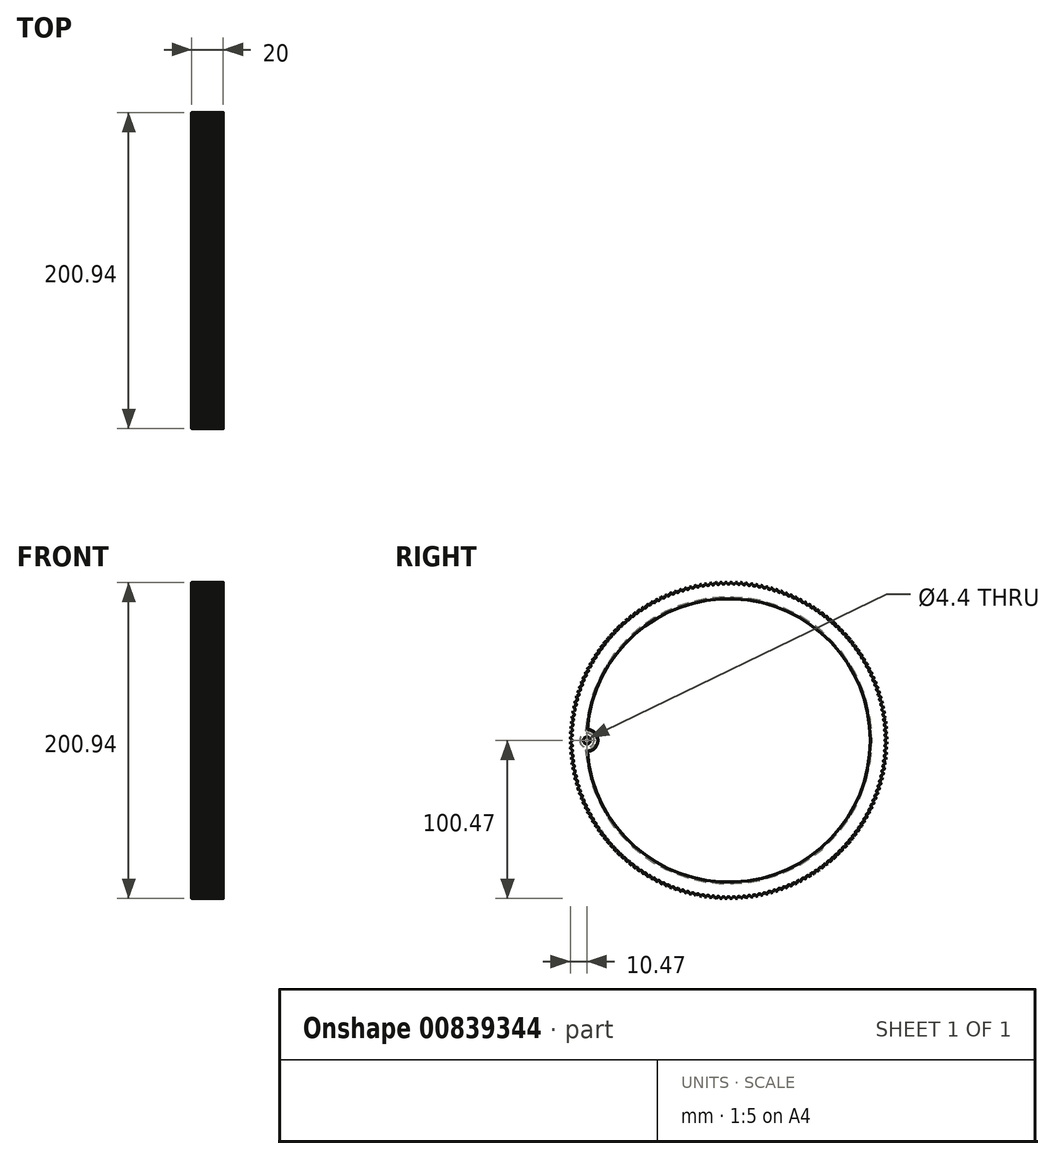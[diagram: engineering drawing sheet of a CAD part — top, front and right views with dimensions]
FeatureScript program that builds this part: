
annotation { "Feature Type Name" : "Feature", "Feature Type Description" : "" }
export const myFeature = defineFeature(function(context is Context, id is Id, definition is map)
    precondition{}
    {
        {
            var Q0;
            Q0=qCreatedBy(makeId("Right.planeOp"),FACE);
            var sketch = newSketch(context, id + "F0", { "sketchPlane" : qUnion([Q0])});
            skCircle(sketch, "E0", {"center": v(0, 0) * mm, "radius": 90 * mm});
            skLineSegment(sketch, "E1", {"start": v(0, 0) * mm, "end": v(0, 100.53) * mm, "construction": true});
            skPoint(sketch, "E2.center", {"position": v(0, 61.04) * mm});
            skLineSegment(sketch, "E2.anchor1", {"start": v(0, 61.04) * mm, "end": v(0, 81.8) * mm, "construction": true});
            skLineSegment(sketch, "E3.trimOffspring", {"start": v(0, 10.5) * mm, "end": v(0, 81.8) * mm, "construction": true});
            skLineSegment(sketch, "E4", {"start": v(-1.05, 100.47) * mm, "end": v(-1, 100.18) * mm});
            skArc(sketch, "E5", {"start": v(0.01, 99.33) * mm, "mid": v(0, 99.33) * mm, "end": v(-0.01, 99.33) * mm});
            skArc(sketch, "E6.filletArc", {"start": v(-1, 100.18) * mm, "mid": v(-0.67, 99.57) * mm, "end": v(-0.01, 99.33) * mm});
            skLineSegment(sketch, "E7.MirrorCS", {"start": v(1.05, 100.47) * mm, "end": v(1, 100.18) * mm});
            skArc(sketch, "E8.MirrorCS", {"start": v(1, 100.18) * mm, "mid": v(0.67, 99.57) * mm, "end": v(0.01, 99.33) * mm});
            skPoint(sketch, "E9.orphan", {"position": v(-12.8, 89.08) * mm});
            skPoint(sketch, "E10.orphan", {"position": v(12.8, 89.08) * mm});
            skLineSegment(sketch, "E11", {"start": v(0.02, 100.33) * mm, "end": v(1, 100.18) * mm, "construction": true});
            skLineSegment(sketch, "E12", {"start": v(-0.02, 100.33) * mm, "end": v(-1, 100.18) * mm, "construction": true});
            skLineSegment(sketch, "E13", {"start": v(-1.05, 100.47) * mm, "end": v(0, 100.53) * mm, "construction": true});
            skLineSegment(sketch, "E14", {"start": v(1.05, 100.47) * mm, "end": v(0, 100.53) * mm, "construction": true});
            skCircle(sketch, "E15", {"center": v(0, 0) * mm, "radius": 100.48 * mm});
            skArc(sketch, "E16.1.0", {"start": v(-4.28, 100.1) * mm, "mid": v(-3.93, 99.5) * mm, "end": v(-3.26, 99.27) * mm});
            skArc(sketch, "E16.1.1", {"start": v(-3.24, 99.27) * mm, "mid": v(-3.25, 99.27) * mm, "end": v(-3.26, 99.27) * mm});
            skArc(sketch, "E16.1.2", {"start": v(-2.27, 100.16) * mm, "mid": v(-2.59, 99.54) * mm, "end": v(-3.24, 99.27) * mm});
            skLineSegment(sketch, "E16.1.3", {"start": v(-2.24, 100.46) * mm, "end": v(-2.27, 100.16) * mm});
            skLineSegment(sketch, "E16.1.4", {"start": v(-4.33, 100.39) * mm, "end": v(-4.28, 100.1) * mm});
            skArc(sketch, "E16.2.0", {"start": v(-7.56, 99.9) * mm, "mid": v(-7.18, 99.31) * mm, "end": v(-6.51, 99.11) * mm});
            skArc(sketch, "E16.2.1", {"start": v(-6.48, 99.12) * mm, "mid": v(-6.5, 99.11) * mm, "end": v(-6.51, 99.11) * mm});
            skArc(sketch, "E16.2.2", {"start": v(-5.55, 100.04) * mm, "mid": v(-5.84, 99.4) * mm, "end": v(-6.48, 99.12) * mm});
            skLineSegment(sketch, "E16.2.3", {"start": v(-5.53, 100.33) * mm, "end": v(-5.55, 100.04) * mm});
            skLineSegment(sketch, "E16.2.4", {"start": v(-7.62, 100.2) * mm, "end": v(-7.56, 99.9) * mm});
            skArc(sketch, "E16.3.0", {"start": v(-10.82, 99.6) * mm, "mid": v(-10.43, 99.03) * mm, "end": v(-9.75, 98.85) * mm});
            skArc(sketch, "E16.3.1", {"start": v(-9.72, 98.85) * mm, "mid": v(-9.74, 98.85) * mm, "end": v(-9.75, 98.85) * mm});
            skArc(sketch, "E16.3.2", {"start": v(-8.82, 99.8) * mm, "mid": v(-9.1, 99.16) * mm, "end": v(-9.72, 98.85) * mm});
            skLineSegment(sketch, "E16.3.3", {"start": v(-8.8, 100.1) * mm, "end": v(-8.82, 99.8) * mm});
            skLineSegment(sketch, "E16.3.4", {"start": v(-10.9, 99.89) * mm, "end": v(-10.82, 99.6) * mm});
            skArc(sketch, "E16.4.0", {"start": v(-14.07, 99.2) * mm, "mid": v(-13.66, 98.63) * mm, "end": v(-12.98, 98.48) * mm});
            skArc(sketch, "E16.4.1", {"start": v(-12.95, 98.48) * mm, "mid": v(-12.96, 98.48) * mm, "end": v(-12.98, 98.48) * mm});
            skArc(sketch, "E16.4.2", {"start": v(-12.08, 99.46) * mm, "mid": v(-12.33, 98.8) * mm, "end": v(-12.95, 98.48) * mm});
            skLineSegment(sketch, "E16.4.3", {"start": v(-12.08, 99.75) * mm, "end": v(-12.08, 99.46) * mm});
            skLineSegment(sketch, "E16.4.4", {"start": v(-14.15, 99.48) * mm, "end": v(-14.07, 99.2) * mm});
            skArc(sketch, "E16.5.0", {"start": v(-17.31, 98.68) * mm, "mid": v(-16.88, 98.13) * mm, "end": v(-16.2, 98) * mm});
            skArc(sketch, "E16.5.1", {"start": v(-16.17, 98) * mm, "mid": v(-16.18, 98) * mm, "end": v(-16.2, 98) * mm});
            skArc(sketch, "E16.5.2", {"start": v(-15.33, 99.01) * mm, "mid": v(-15.56, 98.35) * mm, "end": v(-16.17, 98) * mm});
            skLineSegment(sketch, "E16.5.3", {"start": v(-15.33, 99.3) * mm, "end": v(-15.33, 99.01) * mm});
            skLineSegment(sketch, "E16.5.4", {"start": v(-17.4, 98.96) * mm, "end": v(-17.31, 98.68) * mm});
            skArc(sketch, "E16.6.0", {"start": v(-20.53, 98.06) * mm, "mid": v(-20.08, 97.53) * mm, "end": v(-19.4, 97.42) * mm});
            skArc(sketch, "E16.6.1", {"start": v(-19.36, 97.42) * mm, "mid": v(-19.38, 97.42) * mm, "end": v(-19.4, 97.42) * mm});
            skArc(sketch, "E16.6.2", {"start": v(-18.56, 98.46) * mm, "mid": v(-18.77, 97.79) * mm, "end": v(-19.36, 97.42) * mm});
            skLineSegment(sketch, "E16.6.3", {"start": v(-18.57, 98.75) * mm, "end": v(-18.56, 98.46) * mm});
            skLineSegment(sketch, "E16.6.4", {"start": v(-20.63, 98.34) * mm, "end": v(-20.53, 98.06) * mm});
            skArc(sketch, "E16.7.0", {"start": v(-23.73, 97.34) * mm, "mid": v(-23.26, 96.82) * mm, "end": v(-22.57, 96.73) * mm});
            skArc(sketch, "E16.7.1", {"start": v(-22.54, 96.74) * mm, "mid": v(-22.55, 96.73) * mm, "end": v(-22.57, 96.73) * mm});
            skArc(sketch, "E16.7.2", {"start": v(-21.77, 97.8) * mm, "mid": v(-21.96, 97.12) * mm, "end": v(-22.54, 96.74) * mm});
            skLineSegment(sketch, "E16.7.3", {"start": v(-21.8, 98.09) * mm, "end": v(-21.77, 97.8) * mm});
            skLineSegment(sketch, "E16.7.4", {"start": v(-23.84, 97.61) * mm, "end": v(-23.73, 97.34) * mm});
            skArc(sketch, "E16.8.0", {"start": v(-26.9, 96.51) * mm, "mid": v(-26.42, 96) * mm, "end": v(-25.72, 95.94) * mm});
            skArc(sketch, "E16.8.1", {"start": v(-25.7, 95.95) * mm, "mid": v(-25.7, 95.94) * mm, "end": v(-25.72, 95.94) * mm});
            skArc(sketch, "E16.8.2", {"start": v(-24.96, 97.03) * mm, "mid": v(-25.12, 96.35) * mm, "end": v(-25.7, 95.95) * mm});
            skLineSegment(sketch, "E16.8.3", {"start": v(-25, 97.32) * mm, "end": v(-24.96, 97.03) * mm});
            skLineSegment(sketch, "E16.8.4", {"start": v(-27.02, 96.78) * mm, "end": v(-26.9, 96.51) * mm});
            skArc(sketch, "E16.9.0", {"start": v(-30.04, 95.58) * mm, "mid": v(-29.55, 95.09) * mm, "end": v(-28.85, 95.05) * mm});
            skArc(sketch, "E16.9.1", {"start": v(-28.82, 95.05) * mm, "mid": v(-28.83, 95.05) * mm, "end": v(-28.85, 95.05) * mm});
            skArc(sketch, "E16.9.2", {"start": v(-28.12, 96.16) * mm, "mid": v(-28.26, 95.48) * mm, "end": v(-28.82, 95.05) * mm});
            skLineSegment(sketch, "E16.9.3", {"start": v(-28.16, 96.45) * mm, "end": v(-28.12, 96.16) * mm});
            skLineSegment(sketch, "E16.9.4", {"start": v(-30.17, 95.84) * mm, "end": v(-30.04, 95.58) * mm});
            skArc(sketch, "E16.10.0", {"start": v(-33.16, 94.54) * mm, "mid": v(-32.64, 94.07) * mm, "end": v(-31.94, 94.05) * mm});
            skArc(sketch, "E16.10.1", {"start": v(-31.91, 94.06) * mm, "mid": v(-31.93, 94.06) * mm, "end": v(-31.94, 94.05) * mm});
            skArc(sketch, "E16.10.2", {"start": v(-31.25, 95.2) * mm, "mid": v(-31.37, 94.5) * mm, "end": v(-31.91, 94.06) * mm});
            skLineSegment(sketch, "E16.10.3", {"start": v(-31.3, 95.48) * mm, "end": v(-31.25, 95.2) * mm});
            skLineSegment(sketch, "E16.10.4", {"start": v(-33.29, 94.8) * mm, "end": v(-33.16, 94.54) * mm});
            skArc(sketch, "E16.11.0", {"start": v(-36.23, 93.4) * mm, "mid": v(-35.7, 92.95) * mm, "end": v(-35, 92.96) * mm});
            skArc(sketch, "E16.11.1", {"start": v(-34.97, 92.97) * mm, "mid": v(-34.99, 92.96) * mm, "end": v(-35, 92.96) * mm});
            skArc(sketch, "E16.11.2", {"start": v(-34.35, 94.12) * mm, "mid": v(-34.45, 93.42) * mm, "end": v(-34.97, 92.97) * mm});
            skLineSegment(sketch, "E16.11.3", {"start": v(-34.41, 94.4) * mm, "end": v(-34.35, 94.12) * mm});
            skLineSegment(sketch, "E16.11.4", {"start": v(-36.37, 93.67) * mm, "end": v(-36.23, 93.4) * mm});
            skArc(sketch, "E16.12.0", {"start": v(-39.27, 92.17) * mm, "mid": v(-38.72, 91.73) * mm, "end": v(-38.02, 91.76) * mm});
            skArc(sketch, "E16.12.1", {"start": v(-38, 91.77) * mm, "mid": v(-38.01, 91.77) * mm, "end": v(-38.02, 91.76) * mm});
            skArc(sketch, "E16.12.2", {"start": v(-37.4, 92.94) * mm, "mid": v(-37.48, 92.25) * mm, "end": v(-38, 91.77) * mm});
            skLineSegment(sketch, "E16.12.3", {"start": v(-37.48, 93.23) * mm, "end": v(-37.4, 92.94) * mm});
            skLineSegment(sketch, "E16.12.4", {"start": v(-39.42, 92.43) * mm, "end": v(-39.27, 92.17) * mm});
            skArc(sketch, "E16.13.0", {"start": v(-42.26, 90.84) * mm, "mid": v(-41.7, 90.42) * mm, "end": v(-41, 90.47) * mm});
            skArc(sketch, "E16.13.1", {"start": v(-40.98, 90.48) * mm, "mid": v(-41, 90.47) * mm, "end": v(-41, 90.47) * mm});
            skArc(sketch, "E16.13.2", {"start": v(-40.43, 91.67) * mm, "mid": v(-40.48, 90.97) * mm, "end": v(-40.98, 90.48) * mm});
            skLineSegment(sketch, "E16.13.3", {"start": v(-40.51, 91.95) * mm, "end": v(-40.43, 91.67) * mm});
            skLineSegment(sketch, "E16.13.4", {"start": v(-42.42, 91.09) * mm, "end": v(-42.26, 90.84) * mm});
            skArc(sketch, "E16.14.0", {"start": v(-45.21, 89.4) * mm, "mid": v(-44.64, 89) * mm, "end": v(-43.94, 89.08) * mm});
            skArc(sketch, "E16.14.1", {"start": v(-43.92, 89.09) * mm, "mid": v(-43.93, 89.08) * mm, "end": v(-43.94, 89.08) * mm});
            skArc(sketch, "E16.14.2", {"start": v(-43.4, 90.3) * mm, "mid": v(-43.44, 89.6) * mm, "end": v(-43.92, 89.09) * mm});
            skLineSegment(sketch, "E16.14.3", {"start": v(-43.5, 90.58) * mm, "end": v(-43.4, 90.3) * mm});
            skLineSegment(sketch, "E16.14.4", {"start": v(-45.38, 89.65) * mm, "end": v(-45.21, 89.4) * mm});
            skArc(sketch, "E16.15.0", {"start": v(-48.11, 87.88) * mm, "mid": v(-47.53, 87.5) * mm, "end": v(-46.84, 87.6) * mm});
            skArc(sketch, "E16.15.1", {"start": v(-46.8, 87.6) * mm, "mid": v(-46.82, 87.6) * mm, "end": v(-46.84, 87.6) * mm});
            skArc(sketch, "E16.15.2", {"start": v(-46.34, 88.83) * mm, "mid": v(-46.35, 88.13) * mm, "end": v(-46.8, 87.6) * mm});
            skLineSegment(sketch, "E16.15.3", {"start": v(-46.44, 89.1) * mm, "end": v(-46.34, 88.83) * mm});
            skLineSegment(sketch, "E16.15.4", {"start": v(-48.29, 88.12) * mm, "end": v(-48.11, 87.88) * mm});
            skArc(sketch, "E16.16.0", {"start": v(-50.96, 86.26) * mm, "mid": v(-50.37, 85.9) * mm, "end": v(-49.68, 86.01) * mm});
            skArc(sketch, "E16.16.1", {"start": v(-49.65, 86.03) * mm, "mid": v(-49.66, 86.02) * mm, "end": v(-49.68, 86.01) * mm});
            skArc(sketch, "E16.16.2", {"start": v(-49.22, 87.27) * mm, "mid": v(-49.2, 86.57) * mm, "end": v(-49.65, 86.03) * mm});
            skLineSegment(sketch, "E16.16.3", {"start": v(-49.33, 87.54) * mm, "end": v(-49.22, 87.27) * mm});
            skLineSegment(sketch, "E16.16.4", {"start": v(-51.14, 86.49) * mm, "end": v(-50.96, 86.26) * mm});
            skArc(sketch, "E16.17.0", {"start": v(-53.76, 84.55) * mm, "mid": v(-53.15, 84.2) * mm, "end": v(-52.46, 84.34) * mm});
            skArc(sketch, "E16.17.1", {"start": v(-52.44, 84.36) * mm, "mid": v(-52.45, 84.35) * mm, "end": v(-52.46, 84.34) * mm});
            skArc(sketch, "E16.17.2", {"start": v(-52.05, 85.6) * mm, "mid": v(-52.01, 84.9) * mm, "end": v(-52.44, 84.36) * mm});
            skLineSegment(sketch, "E16.17.3", {"start": v(-52.17, 85.88) * mm, "end": v(-52.05, 85.6) * mm});
            skLineSegment(sketch, "E16.17.4", {"start": v(-53.95, 84.77) * mm, "end": v(-53.76, 84.55) * mm});
            skArc(sketch, "E16.18.0", {"start": v(-56.5, 82.74) * mm, "mid": v(-55.88, 82.42) * mm, "end": v(-55.2, 82.58) * mm});
            skArc(sketch, "E16.18.1", {"start": v(-55.17, 82.6) * mm, "mid": v(-55.18, 82.59) * mm, "end": v(-55.2, 82.58) * mm});
            skArc(sketch, "E16.18.2", {"start": v(-54.82, 83.86) * mm, "mid": v(-54.76, 83.16) * mm, "end": v(-55.17, 82.6) * mm});
            skLineSegment(sketch, "E16.18.3", {"start": v(-54.95, 84.12) * mm, "end": v(-54.82, 83.86) * mm});
            skLineSegment(sketch, "E16.18.4", {"start": v(-56.7, 82.96) * mm, "end": v(-56.5, 82.74) * mm});
            skArc(sketch, "E16.19.0", {"start": v(-59.17, 80.85) * mm, "mid": v(-58.54, 80.55) * mm, "end": v(-57.87, 80.73) * mm});
            skArc(sketch, "E16.19.1", {"start": v(-57.84, 80.75) * mm, "mid": v(-57.86, 80.74) * mm, "end": v(-57.87, 80.73) * mm});
            skArc(sketch, "E16.19.2", {"start": v(-57.54, 82.02) * mm, "mid": v(-57.45, 81.33) * mm, "end": v(-57.84, 80.75) * mm});
            skLineSegment(sketch, "E16.19.3", {"start": v(-57.67, 82.28) * mm, "end": v(-57.54, 82.02) * mm});
            skLineSegment(sketch, "E16.19.4", {"start": v(-59.38, 81.06) * mm, "end": v(-59.17, 80.85) * mm});
            skArc(sketch, "E16.20.0", {"start": v(-61.79, 78.87) * mm, "mid": v(-61.15, 78.59) * mm, "end": v(-60.48, 78.8) * mm});
            skArc(sketch, "E16.20.1", {"start": v(-60.45, 78.81) * mm, "mid": v(-60.47, 78.8) * mm, "end": v(-60.48, 78.8) * mm});
            skArc(sketch, "E16.20.2", {"start": v(-60.2, 80.1) * mm, "mid": v(-60.08, 79.4) * mm, "end": v(-60.45, 78.81) * mm});
            skLineSegment(sketch, "E16.20.3", {"start": v(-60.33, 80.35) * mm, "end": v(-60.2, 80.1) * mm});
            skLineSegment(sketch, "E16.20.4", {"start": v(-62, 79.07) * mm, "end": v(-61.79, 78.87) * mm});
            skArc(sketch, "E16.21.0", {"start": v(-64.33, 76.8) * mm, "mid": v(-63.69, 76.54) * mm, "end": v(-63.02, 76.77) * mm});
            skArc(sketch, "E16.21.1", {"start": v(-63, 76.79) * mm, "mid": v(-63.01, 76.78) * mm, "end": v(-63.02, 76.77) * mm});
            skArc(sketch, "E16.21.2", {"start": v(-62.78, 78.08) * mm, "mid": v(-62.65, 77.4) * mm, "end": v(-63, 76.79) * mm});
            skLineSegment(sketch, "E16.21.3", {"start": v(-62.93, 78.33) * mm, "end": v(-62.78, 78.08) * mm});
            skLineSegment(sketch, "E16.21.4", {"start": v(-64.55, 77) * mm, "end": v(-64.33, 76.8) * mm});
            skArc(sketch, "E16.22.0", {"start": v(-66.81, 74.66) * mm, "mid": v(-66.16, 74.42) * mm, "end": v(-65.5, 74.67) * mm});
            skArc(sketch, "E16.22.1", {"start": v(-65.48, 74.69) * mm, "mid": v(-65.5, 74.68) * mm, "end": v(-65.5, 74.67) * mm});
            skArc(sketch, "E16.22.2", {"start": v(-65.3, 75.99) * mm, "mid": v(-65.15, 75.3) * mm, "end": v(-65.48, 74.69) * mm});
            skLineSegment(sketch, "E16.22.3", {"start": v(-65.46, 76.23) * mm, "end": v(-65.3, 75.99) * mm});
            skLineSegment(sketch, "E16.22.4", {"start": v(-67.04, 74.85) * mm, "end": v(-66.81, 74.66) * mm});
            skArc(sketch, "E16.23.0", {"start": v(-69.22, 72.43) * mm, "mid": v(-68.55, 72.21) * mm, "end": v(-67.9, 72.49) * mm});
            skArc(sketch, "E16.23.1", {"start": v(-67.89, 72.5) * mm, "mid": v(-67.9, 72.5) * mm, "end": v(-67.9, 72.49) * mm});
            skArc(sketch, "E16.23.2", {"start": v(-67.75, 73.8) * mm, "mid": v(-67.58, 73.13) * mm, "end": v(-67.89, 72.5) * mm});
            skLineSegment(sketch, "E16.23.3", {"start": v(-67.92, 74.05) * mm, "end": v(-67.75, 73.8) * mm});
            skLineSegment(sketch, "E16.23.4", {"start": v(-69.45, 72.62) * mm, "end": v(-69.22, 72.43) * mm});
            skArc(sketch, "E16.24.0", {"start": v(-71.55, 70.13) * mm, "mid": v(-70.88, 69.93) * mm, "end": v(-70.24, 70.22) * mm});
            skArc(sketch, "E16.24.1", {"start": v(-70.22, 70.24) * mm, "mid": v(-70.23, 70.23) * mm, "end": v(-70.24, 70.22) * mm});
            skArc(sketch, "E16.24.2", {"start": v(-70.13, 71.55) * mm, "mid": v(-69.93, 70.88) * mm, "end": v(-70.22, 70.24) * mm});
            skLineSegment(sketch, "E16.24.3", {"start": v(-70.3, 71.79) * mm, "end": v(-70.13, 71.55) * mm});
            skLineSegment(sketch, "E16.24.4", {"start": v(-71.79, 70.3) * mm, "end": v(-71.55, 70.13) * mm});
            skArc(sketch, "E16.25.0", {"start": v(-73.8, 67.75) * mm, "mid": v(-73.13, 67.58) * mm, "end": v(-72.5, 67.89) * mm});
            skArc(sketch, "E16.25.1", {"start": v(-72.49, 67.9) * mm, "mid": v(-72.5, 67.9) * mm, "end": v(-72.5, 67.89) * mm});
            skArc(sketch, "E16.25.2", {"start": v(-72.43, 69.22) * mm, "mid": v(-72.21, 68.55) * mm, "end": v(-72.49, 67.9) * mm});
            skLineSegment(sketch, "E16.25.3", {"start": v(-72.62, 69.45) * mm, "end": v(-72.43, 69.22) * mm});
            skLineSegment(sketch, "E16.25.4", {"start": v(-74.05, 67.92) * mm, "end": v(-73.8, 67.75) * mm});
            skArc(sketch, "E16.26.0", {"start": v(-75.99, 65.3) * mm, "mid": v(-75.3, 65.15) * mm, "end": v(-74.69, 65.48) * mm});
            skArc(sketch, "E16.26.1", {"start": v(-74.67, 65.5) * mm, "mid": v(-74.68, 65.5) * mm, "end": v(-74.69, 65.48) * mm});
            skArc(sketch, "E16.26.2", {"start": v(-74.66, 66.81) * mm, "mid": v(-74.42, 66.16) * mm, "end": v(-74.67, 65.5) * mm});
            skLineSegment(sketch, "E16.26.3", {"start": v(-74.85, 67.04) * mm, "end": v(-74.66, 66.81) * mm});
            skLineSegment(sketch, "E16.26.4", {"start": v(-76.23, 65.46) * mm, "end": v(-75.99, 65.3) * mm});
            skArc(sketch, "E16.27.0", {"start": v(-78.08, 62.78) * mm, "mid": v(-77.4, 62.65) * mm, "end": v(-76.79, 63) * mm});
            skArc(sketch, "E16.27.1", {"start": v(-76.77, 63.02) * mm, "mid": v(-76.78, 63.01) * mm, "end": v(-76.79, 63) * mm});
            skArc(sketch, "E16.27.2", {"start": v(-76.8, 64.33) * mm, "mid": v(-76.54, 63.69) * mm, "end": v(-76.77, 63.02) * mm});
            skLineSegment(sketch, "E16.27.3", {"start": v(-77, 64.55) * mm, "end": v(-76.8, 64.33) * mm});
            skLineSegment(sketch, "E16.27.4", {"start": v(-78.33, 62.93) * mm, "end": v(-78.08, 62.78) * mm});
            skArc(sketch, "E16.28.0", {"start": v(-80.1, 60.2) * mm, "mid": v(-79.4, 60.08) * mm, "end": v(-78.81, 60.45) * mm});
            skArc(sketch, "E16.28.1", {"start": v(-78.8, 60.48) * mm, "mid": v(-78.8, 60.47) * mm, "end": v(-78.81, 60.45) * mm});
            skArc(sketch, "E16.28.2", {"start": v(-78.87, 61.79) * mm, "mid": v(-78.59, 61.15) * mm, "end": v(-78.8, 60.48) * mm});
            skLineSegment(sketch, "E16.28.3", {"start": v(-79.07, 62) * mm, "end": v(-78.87, 61.79) * mm});
            skLineSegment(sketch, "E16.28.4", {"start": v(-80.35, 60.33) * mm, "end": v(-80.1, 60.2) * mm});
            skArc(sketch, "E16.29.0", {"start": v(-82.02, 57.54) * mm, "mid": v(-81.33, 57.45) * mm, "end": v(-80.75, 57.84) * mm});
            skArc(sketch, "E16.29.1", {"start": v(-80.73, 57.87) * mm, "mid": v(-80.74, 57.86) * mm, "end": v(-80.75, 57.84) * mm});
            skArc(sketch, "E16.29.2", {"start": v(-80.85, 59.17) * mm, "mid": v(-80.55, 58.54) * mm, "end": v(-80.73, 57.87) * mm});
            skLineSegment(sketch, "E16.29.3", {"start": v(-81.06, 59.38) * mm, "end": v(-80.85, 59.17) * mm});
            skLineSegment(sketch, "E16.29.4", {"start": v(-82.28, 57.67) * mm, "end": v(-82.02, 57.54) * mm});
            skArc(sketch, "E16.30.0", {"start": v(-83.86, 54.82) * mm, "mid": v(-83.16, 54.76) * mm, "end": v(-82.6, 55.17) * mm});
            skArc(sketch, "E16.30.1", {"start": v(-82.58, 55.2) * mm, "mid": v(-82.59, 55.18) * mm, "end": v(-82.6, 55.17) * mm});
            skArc(sketch, "E16.30.2", {"start": v(-82.74, 56.5) * mm, "mid": v(-82.42, 55.88) * mm, "end": v(-82.58, 55.2) * mm});
            skLineSegment(sketch, "E16.30.3", {"start": v(-82.96, 56.7) * mm, "end": v(-82.74, 56.5) * mm});
            skLineSegment(sketch, "E16.30.4", {"start": v(-84.12, 54.95) * mm, "end": v(-83.86, 54.82) * mm});
            skArc(sketch, "E16.31.0", {"start": v(-85.6, 52.05) * mm, "mid": v(-84.9, 52.01) * mm, "end": v(-84.36, 52.44) * mm});
            skArc(sketch, "E16.31.1", {"start": v(-84.34, 52.46) * mm, "mid": v(-84.35, 52.45) * mm, "end": v(-84.36, 52.44) * mm});
            skArc(sketch, "E16.31.2", {"start": v(-84.55, 53.76) * mm, "mid": v(-84.2, 53.15) * mm, "end": v(-84.34, 52.46) * mm});
            skLineSegment(sketch, "E16.31.3", {"start": v(-84.77, 53.95) * mm, "end": v(-84.55, 53.76) * mm});
            skLineSegment(sketch, "E16.31.4", {"start": v(-85.88, 52.17) * mm, "end": v(-85.6, 52.05) * mm});
            skArc(sketch, "E16.32.0", {"start": v(-87.27, 49.22) * mm, "mid": v(-86.57, 49.2) * mm, "end": v(-86.03, 49.65) * mm});
            skArc(sketch, "E16.32.1", {"start": v(-86.01, 49.68) * mm, "mid": v(-86.02, 49.66) * mm, "end": v(-86.03, 49.65) * mm});
            skArc(sketch, "E16.32.2", {"start": v(-86.26, 50.96) * mm, "mid": v(-85.9, 50.37) * mm, "end": v(-86.01, 49.68) * mm});
            skLineSegment(sketch, "E16.32.3", {"start": v(-86.49, 51.14) * mm, "end": v(-86.26, 50.96) * mm});
            skLineSegment(sketch, "E16.32.4", {"start": v(-87.54, 49.33) * mm, "end": v(-87.27, 49.22) * mm});
            skArc(sketch, "E16.33.0", {"start": v(-88.83, 46.34) * mm, "mid": v(-88.13, 46.35) * mm, "end": v(-87.6, 46.8) * mm});
            skArc(sketch, "E16.33.1", {"start": v(-87.6, 46.84) * mm, "mid": v(-87.6, 46.82) * mm, "end": v(-87.6, 46.8) * mm});
            skArc(sketch, "E16.33.2", {"start": v(-87.88, 48.11) * mm, "mid": v(-87.5, 47.53) * mm, "end": v(-87.6, 46.84) * mm});
            skLineSegment(sketch, "E16.33.3", {"start": v(-88.12, 48.29) * mm, "end": v(-87.88, 48.11) * mm});
            skLineSegment(sketch, "E16.33.4", {"start": v(-89.1, 46.44) * mm, "end": v(-88.83, 46.34) * mm});
            skArc(sketch, "E16.34.0", {"start": v(-90.3, 43.4) * mm, "mid": v(-89.6, 43.44) * mm, "end": v(-89.09, 43.92) * mm});
            skArc(sketch, "E16.34.1", {"start": v(-89.08, 43.94) * mm, "mid": v(-89.08, 43.93) * mm, "end": v(-89.09, 43.92) * mm});
            skArc(sketch, "E16.34.2", {"start": v(-89.4, 45.21) * mm, "mid": v(-89, 44.64) * mm, "end": v(-89.08, 43.94) * mm});
            skLineSegment(sketch, "E16.34.3", {"start": v(-89.65, 45.38) * mm, "end": v(-89.4, 45.21) * mm});
            skLineSegment(sketch, "E16.34.4", {"start": v(-90.58, 43.5) * mm, "end": v(-90.3, 43.4) * mm});
            skArc(sketch, "E16.35.0", {"start": v(-91.67, 40.43) * mm, "mid": v(-90.97, 40.48) * mm, "end": v(-90.48, 40.98) * mm});
            skArc(sketch, "E16.35.1", {"start": v(-90.47, 41) * mm, "mid": v(-90.47, 41) * mm, "end": v(-90.48, 40.98) * mm});
            skArc(sketch, "E16.35.2", {"start": v(-90.84, 42.26) * mm, "mid": v(-90.42, 41.7) * mm, "end": v(-90.47, 41) * mm});
            skLineSegment(sketch, "E16.35.3", {"start": v(-91.09, 42.42) * mm, "end": v(-90.84, 42.26) * mm});
            skLineSegment(sketch, "E16.35.4", {"start": v(-91.95, 40.51) * mm, "end": v(-91.67, 40.43) * mm});
            skArc(sketch, "E16.36.0", {"start": v(-92.94, 37.4) * mm, "mid": v(-92.25, 37.48) * mm, "end": v(-91.77, 38) * mm});
            skArc(sketch, "E16.36.1", {"start": v(-91.76, 38.02) * mm, "mid": v(-91.77, 38.01) * mm, "end": v(-91.77, 38) * mm});
            skArc(sketch, "E16.36.2", {"start": v(-92.17, 39.27) * mm, "mid": v(-91.73, 38.72) * mm, "end": v(-91.76, 38.02) * mm});
            skLineSegment(sketch, "E16.36.3", {"start": v(-92.43, 39.42) * mm, "end": v(-92.17, 39.27) * mm});
            skLineSegment(sketch, "E16.36.4", {"start": v(-93.23, 37.48) * mm, "end": v(-92.94, 37.4) * mm});
            skArc(sketch, "E16.37.0", {"start": v(-94.12, 34.35) * mm, "mid": v(-93.42, 34.45) * mm, "end": v(-92.97, 34.97) * mm});
            skArc(sketch, "E16.37.1", {"start": v(-92.96, 35) * mm, "mid": v(-92.96, 34.99) * mm, "end": v(-92.97, 34.97) * mm});
            skArc(sketch, "E16.37.2", {"start": v(-93.4, 36.23) * mm, "mid": v(-92.95, 35.7) * mm, "end": v(-92.96, 35) * mm});
            skLineSegment(sketch, "E16.37.3", {"start": v(-93.67, 36.37) * mm, "end": v(-93.4, 36.23) * mm});
            skLineSegment(sketch, "E16.37.4", {"start": v(-94.4, 34.41) * mm, "end": v(-94.12, 34.35) * mm});
            skArc(sketch, "E16.38.0", {"start": v(-95.2, 31.25) * mm, "mid": v(-94.5, 31.37) * mm, "end": v(-94.06, 31.91) * mm});
            skArc(sketch, "E16.38.1", {"start": v(-94.05, 31.94) * mm, "mid": v(-94.06, 31.93) * mm, "end": v(-94.06, 31.91) * mm});
            skArc(sketch, "E16.38.2", {"start": v(-94.54, 33.16) * mm, "mid": v(-94.07, 32.64) * mm, "end": v(-94.05, 31.94) * mm});
            skLineSegment(sketch, "E16.38.3", {"start": v(-94.8, 33.29) * mm, "end": v(-94.54, 33.16) * mm});
            skLineSegment(sketch, "E16.38.4", {"start": v(-95.48, 31.3) * mm, "end": v(-95.2, 31.25) * mm});
            skArc(sketch, "E16.39.0", {"start": v(-96.16, 28.12) * mm, "mid": v(-95.48, 28.26) * mm, "end": v(-95.05, 28.82) * mm});
            skArc(sketch, "E16.39.1", {"start": v(-95.05, 28.85) * mm, "mid": v(-95.05, 28.83) * mm, "end": v(-95.05, 28.82) * mm});
            skArc(sketch, "E16.39.2", {"start": v(-95.58, 30.04) * mm, "mid": v(-95.09, 29.55) * mm, "end": v(-95.05, 28.85) * mm});
            skLineSegment(sketch, "E16.39.3", {"start": v(-95.84, 30.17) * mm, "end": v(-95.58, 30.04) * mm});
            skLineSegment(sketch, "E16.39.4", {"start": v(-96.45, 28.16) * mm, "end": v(-96.16, 28.12) * mm});
            skArc(sketch, "E16.40.0", {"start": v(-97.03, 24.96) * mm, "mid": v(-96.35, 25.12) * mm, "end": v(-95.95, 25.7) * mm});
            skArc(sketch, "E16.40.1", {"start": v(-95.94, 25.72) * mm, "mid": v(-95.94, 25.7) * mm, "end": v(-95.95, 25.7) * mm});
            skArc(sketch, "E16.40.2", {"start": v(-96.51, 26.9) * mm, "mid": v(-96, 26.42) * mm, "end": v(-95.94, 25.72) * mm});
            skLineSegment(sketch, "E16.40.3", {"start": v(-96.78, 27.02) * mm, "end": v(-96.51, 26.9) * mm});
            skLineSegment(sketch, "E16.40.4", {"start": v(-97.32, 25) * mm, "end": v(-97.03, 24.96) * mm});
            skArc(sketch, "E16.41.0", {"start": v(-97.8, 21.77) * mm, "mid": v(-97.12, 21.96) * mm, "end": v(-96.74, 22.54) * mm});
            skArc(sketch, "E16.41.1", {"start": v(-96.73, 22.57) * mm, "mid": v(-96.73, 22.55) * mm, "end": v(-96.74, 22.54) * mm});
            skArc(sketch, "E16.41.2", {"start": v(-97.34, 23.73) * mm, "mid": v(-96.82, 23.26) * mm, "end": v(-96.73, 22.57) * mm});
            skLineSegment(sketch, "E16.41.3", {"start": v(-97.61, 23.84) * mm, "end": v(-97.34, 23.73) * mm});
            skLineSegment(sketch, "E16.41.4", {"start": v(-98.09, 21.8) * mm, "end": v(-97.8, 21.77) * mm});
            skArc(sketch, "E16.42.0", {"start": v(-98.46, 18.56) * mm, "mid": v(-97.79, 18.77) * mm, "end": v(-97.42, 19.36) * mm});
            skArc(sketch, "E16.42.1", {"start": v(-97.42, 19.4) * mm, "mid": v(-97.42, 19.38) * mm, "end": v(-97.42, 19.36) * mm});
            skArc(sketch, "E16.42.2", {"start": v(-98.06, 20.53) * mm, "mid": v(-97.53, 20.08) * mm, "end": v(-97.42, 19.4) * mm});
            skLineSegment(sketch, "E16.42.3", {"start": v(-98.34, 20.63) * mm, "end": v(-98.06, 20.53) * mm});
            skLineSegment(sketch, "E16.42.4", {"start": v(-98.75, 18.57) * mm, "end": v(-98.46, 18.56) * mm});
            skArc(sketch, "E16.43.0", {"start": v(-99.01, 15.33) * mm, "mid": v(-98.35, 15.56) * mm, "end": v(-98, 16.17) * mm});
            skArc(sketch, "E16.43.1", {"start": v(-98, 16.2) * mm, "mid": v(-98, 16.18) * mm, "end": v(-98, 16.17) * mm});
            skArc(sketch, "E16.43.2", {"start": v(-98.68, 17.31) * mm, "mid": v(-98.13, 16.88) * mm, "end": v(-98, 16.2) * mm});
            skLineSegment(sketch, "E16.43.3", {"start": v(-98.96, 17.4) * mm, "end": v(-98.68, 17.31) * mm});
            skLineSegment(sketch, "E16.43.4", {"start": v(-99.3, 15.33) * mm, "end": v(-99.01, 15.33) * mm});
            skArc(sketch, "E16.44.0", {"start": v(-99.46, 12.08) * mm, "mid": v(-98.8, 12.33) * mm, "end": v(-98.48, 12.95) * mm});
            skArc(sketch, "E16.44.1", {"start": v(-98.48, 12.98) * mm, "mid": v(-98.48, 12.96) * mm, "end": v(-98.48, 12.95) * mm});
            skArc(sketch, "E16.44.2", {"start": v(-99.2, 14.07) * mm, "mid": v(-98.63, 13.66) * mm, "end": v(-98.48, 12.98) * mm});
            skLineSegment(sketch, "E16.44.3", {"start": v(-99.48, 14.15) * mm, "end": v(-99.2, 14.07) * mm});
            skLineSegment(sketch, "E16.44.4", {"start": v(-99.75, 12.08) * mm, "end": v(-99.46, 12.08) * mm});
            skArc(sketch, "E16.45.0", {"start": v(-99.8, 8.82) * mm, "mid": v(-99.16, 9.1) * mm, "end": v(-98.85, 9.72) * mm});
            skArc(sketch, "E16.45.1", {"start": v(-98.85, 9.75) * mm, "mid": v(-98.85, 9.74) * mm, "end": v(-98.85, 9.72) * mm});
            skArc(sketch, "E16.45.2", {"start": v(-99.6, 10.82) * mm, "mid": v(-99.03, 10.43) * mm, "end": v(-98.85, 9.75) * mm});
            skLineSegment(sketch, "E16.45.3", {"start": v(-99.89, 10.9) * mm, "end": v(-99.6, 10.82) * mm});
            skLineSegment(sketch, "E16.45.4", {"start": v(-100.1, 8.8) * mm, "end": v(-99.8, 8.82) * mm});
            skArc(sketch, "E16.46.0", {"start": v(-100.04, 5.55) * mm, "mid": v(-99.4, 5.84) * mm, "end": v(-99.12, 6.48) * mm});
            skArc(sketch, "E16.46.1", {"start": v(-99.11, 6.51) * mm, "mid": v(-99.11, 6.5) * mm, "end": v(-99.12, 6.48) * mm});
            skArc(sketch, "E16.46.2", {"start": v(-99.9, 7.56) * mm, "mid": v(-99.31, 7.18) * mm, "end": v(-99.11, 6.51) * mm});
            skLineSegment(sketch, "E16.46.3", {"start": v(-100.2, 7.62) * mm, "end": v(-99.9, 7.56) * mm});
            skLineSegment(sketch, "E16.46.4", {"start": v(-100.33, 5.53) * mm, "end": v(-100.04, 5.55) * mm});
            skArc(sketch, "E16.47.0", {"start": v(-100.16, 2.27) * mm, "mid": v(-99.54, 2.59) * mm, "end": v(-99.27, 3.24) * mm});
            skArc(sketch, "E16.47.1", {"start": v(-99.27, 3.26) * mm, "mid": v(-99.27, 3.25) * mm, "end": v(-99.27, 3.24) * mm});
            skArc(sketch, "E16.47.2", {"start": v(-100.1, 4.28) * mm, "mid": v(-99.5, 3.93) * mm, "end": v(-99.27, 3.26) * mm});
            skLineSegment(sketch, "E16.47.3", {"start": v(-100.39, 4.33) * mm, "end": v(-100.1, 4.28) * mm});
            skLineSegment(sketch, "E16.47.4", {"start": v(-100.46, 2.24) * mm, "end": v(-100.16, 2.27) * mm});
            skArc(sketch, "E16.48.0", {"start": v(-100.18, -1) * mm, "mid": v(-99.57, -0.67) * mm, "end": v(-99.33, -0.01) * mm});
            skArc(sketch, "E16.48.1", {"start": v(-99.33, 0.01) * mm, "mid": v(-99.33, 0) * mm, "end": v(-99.33, -0.01) * mm});
            skArc(sketch, "E16.48.2", {"start": v(-100.18, 1) * mm, "mid": v(-99.57, 0.67) * mm, "end": v(-99.33, 0.01) * mm});
            skLineSegment(sketch, "E16.48.3", {"start": v(-100.47, 1.05) * mm, "end": v(-100.18, 1) * mm});
            skLineSegment(sketch, "E16.48.4", {"start": v(-100.47, -1.05) * mm, "end": v(-100.18, -1) * mm});
            skArc(sketch, "E16.49.0", {"start": v(-100.1, -4.28) * mm, "mid": v(-99.5, -3.93) * mm, "end": v(-99.27, -3.26) * mm});
            skArc(sketch, "E16.49.1", {"start": v(-99.27, -3.24) * mm, "mid": v(-99.27, -3.25) * mm, "end": v(-99.27, -3.26) * mm});
            skArc(sketch, "E16.49.2", {"start": v(-100.16, -2.27) * mm, "mid": v(-99.54, -2.59) * mm, "end": v(-99.27, -3.24) * mm});
            skLineSegment(sketch, "E16.49.3", {"start": v(-100.46, -2.24) * mm, "end": v(-100.16, -2.27) * mm});
            skLineSegment(sketch, "E16.49.4", {"start": v(-100.39, -4.33) * mm, "end": v(-100.1, -4.28) * mm});
            skArc(sketch, "E16.50.0", {"start": v(-99.9, -7.56) * mm, "mid": v(-99.31, -7.18) * mm, "end": v(-99.11, -6.51) * mm});
            skArc(sketch, "E16.50.1", {"start": v(-99.12, -6.48) * mm, "mid": v(-99.11, -6.5) * mm, "end": v(-99.11, -6.51) * mm});
            skArc(sketch, "E16.50.2", {"start": v(-100.04, -5.55) * mm, "mid": v(-99.4, -5.84) * mm, "end": v(-99.12, -6.48) * mm});
            skLineSegment(sketch, "E16.50.3", {"start": v(-100.33, -5.53) * mm, "end": v(-100.04, -5.55) * mm});
            skLineSegment(sketch, "E16.50.4", {"start": v(-100.2, -7.62) * mm, "end": v(-99.9, -7.56) * mm});
            skArc(sketch, "E16.51.0", {"start": v(-99.6, -10.82) * mm, "mid": v(-99.03, -10.43) * mm, "end": v(-98.85, -9.75) * mm});
            skArc(sketch, "E16.51.1", {"start": v(-98.85, -9.72) * mm, "mid": v(-98.85, -9.74) * mm, "end": v(-98.85, -9.75) * mm});
            skArc(sketch, "E16.51.2", {"start": v(-99.8, -8.82) * mm, "mid": v(-99.16, -9.1) * mm, "end": v(-98.85, -9.72) * mm});
            skLineSegment(sketch, "E16.51.3", {"start": v(-100.1, -8.8) * mm, "end": v(-99.8, -8.82) * mm});
            skLineSegment(sketch, "E16.51.4", {"start": v(-99.89, -10.9) * mm, "end": v(-99.6, -10.82) * mm});
            skArc(sketch, "E16.52.0", {"start": v(-99.2, -14.07) * mm, "mid": v(-98.63, -13.66) * mm, "end": v(-98.48, -12.98) * mm});
            skArc(sketch, "E16.52.1", {"start": v(-98.48, -12.95) * mm, "mid": v(-98.48, -12.96) * mm, "end": v(-98.48, -12.98) * mm});
            skArc(sketch, "E16.52.2", {"start": v(-99.46, -12.08) * mm, "mid": v(-98.8, -12.33) * mm, "end": v(-98.48, -12.95) * mm});
            skLineSegment(sketch, "E16.52.3", {"start": v(-99.75, -12.08) * mm, "end": v(-99.46, -12.08) * mm});
            skLineSegment(sketch, "E16.52.4", {"start": v(-99.48, -14.15) * mm, "end": v(-99.2, -14.07) * mm});
            skArc(sketch, "E16.53.0", {"start": v(-98.68, -17.31) * mm, "mid": v(-98.13, -16.88) * mm, "end": v(-98, -16.2) * mm});
            skArc(sketch, "E16.53.1", {"start": v(-98, -16.17) * mm, "mid": v(-98, -16.18) * mm, "end": v(-98, -16.2) * mm});
            skArc(sketch, "E16.53.2", {"start": v(-99.01, -15.33) * mm, "mid": v(-98.35, -15.56) * mm, "end": v(-98, -16.17) * mm});
            skLineSegment(sketch, "E16.53.3", {"start": v(-99.3, -15.33) * mm, "end": v(-99.01, -15.33) * mm});
            skLineSegment(sketch, "E16.53.4", {"start": v(-98.96, -17.4) * mm, "end": v(-98.68, -17.31) * mm});
            skArc(sketch, "E16.54.0", {"start": v(-98.06, -20.53) * mm, "mid": v(-97.53, -20.08) * mm, "end": v(-97.42, -19.4) * mm});
            skArc(sketch, "E16.54.1", {"start": v(-97.42, -19.36) * mm, "mid": v(-97.42, -19.38) * mm, "end": v(-97.42, -19.4) * mm});
            skArc(sketch, "E16.54.2", {"start": v(-98.46, -18.56) * mm, "mid": v(-97.79, -18.77) * mm, "end": v(-97.42, -19.36) * mm});
            skLineSegment(sketch, "E16.54.3", {"start": v(-98.75, -18.57) * mm, "end": v(-98.46, -18.56) * mm});
            skLineSegment(sketch, "E16.54.4", {"start": v(-98.34, -20.63) * mm, "end": v(-98.06, -20.53) * mm});
            skArc(sketch, "E16.55.0", {"start": v(-97.34, -23.73) * mm, "mid": v(-96.82, -23.26) * mm, "end": v(-96.73, -22.57) * mm});
            skArc(sketch, "E16.55.1", {"start": v(-96.74, -22.54) * mm, "mid": v(-96.73, -22.55) * mm, "end": v(-96.73, -22.57) * mm});
            skArc(sketch, "E16.55.2", {"start": v(-97.8, -21.77) * mm, "mid": v(-97.12, -21.96) * mm, "end": v(-96.74, -22.54) * mm});
            skLineSegment(sketch, "E16.55.3", {"start": v(-98.09, -21.8) * mm, "end": v(-97.8, -21.77) * mm});
            skLineSegment(sketch, "E16.55.4", {"start": v(-97.61, -23.84) * mm, "end": v(-97.34, -23.73) * mm});
            skArc(sketch, "E16.56.0", {"start": v(-96.51, -26.9) * mm, "mid": v(-96, -26.42) * mm, "end": v(-95.94, -25.72) * mm});
            skArc(sketch, "E16.56.1", {"start": v(-95.95, -25.7) * mm, "mid": v(-95.94, -25.7) * mm, "end": v(-95.94, -25.72) * mm});
            skArc(sketch, "E16.56.2", {"start": v(-97.03, -24.96) * mm, "mid": v(-96.35, -25.12) * mm, "end": v(-95.95, -25.7) * mm});
            skLineSegment(sketch, "E16.56.3", {"start": v(-97.32, -25) * mm, "end": v(-97.03, -24.96) * mm});
            skLineSegment(sketch, "E16.56.4", {"start": v(-96.78, -27.02) * mm, "end": v(-96.51, -26.9) * mm});
            skArc(sketch, "E16.57.0", {"start": v(-95.58, -30.04) * mm, "mid": v(-95.09, -29.55) * mm, "end": v(-95.05, -28.85) * mm});
            skArc(sketch, "E16.57.1", {"start": v(-95.05, -28.82) * mm, "mid": v(-95.05, -28.83) * mm, "end": v(-95.05, -28.85) * mm});
            skArc(sketch, "E16.57.2", {"start": v(-96.16, -28.12) * mm, "mid": v(-95.48, -28.26) * mm, "end": v(-95.05, -28.82) * mm});
            skLineSegment(sketch, "E16.57.3", {"start": v(-96.45, -28.16) * mm, "end": v(-96.16, -28.12) * mm});
            skLineSegment(sketch, "E16.57.4", {"start": v(-95.84, -30.17) * mm, "end": v(-95.58, -30.04) * mm});
            skArc(sketch, "E16.58.0", {"start": v(-94.54, -33.16) * mm, "mid": v(-94.07, -32.64) * mm, "end": v(-94.05, -31.94) * mm});
            skArc(sketch, "E16.58.1", {"start": v(-94.06, -31.91) * mm, "mid": v(-94.06, -31.93) * mm, "end": v(-94.05, -31.94) * mm});
            skArc(sketch, "E16.58.2", {"start": v(-95.2, -31.25) * mm, "mid": v(-94.5, -31.37) * mm, "end": v(-94.06, -31.91) * mm});
            skLineSegment(sketch, "E16.58.3", {"start": v(-95.48, -31.3) * mm, "end": v(-95.2, -31.25) * mm});
            skLineSegment(sketch, "E16.58.4", {"start": v(-94.8, -33.29) * mm, "end": v(-94.54, -33.16) * mm});
            skArc(sketch, "E16.59.0", {"start": v(-93.4, -36.23) * mm, "mid": v(-92.95, -35.7) * mm, "end": v(-92.96, -35) * mm});
            skArc(sketch, "E16.59.1", {"start": v(-92.97, -34.97) * mm, "mid": v(-92.96, -34.99) * mm, "end": v(-92.96, -35) * mm});
            skArc(sketch, "E16.59.2", {"start": v(-94.12, -34.35) * mm, "mid": v(-93.42, -34.45) * mm, "end": v(-92.97, -34.97) * mm});
            skLineSegment(sketch, "E16.59.3", {"start": v(-94.4, -34.41) * mm, "end": v(-94.12, -34.35) * mm});
            skLineSegment(sketch, "E16.59.4", {"start": v(-93.67, -36.37) * mm, "end": v(-93.4, -36.23) * mm});
            skArc(sketch, "E16.60.0", {"start": v(-92.17, -39.27) * mm, "mid": v(-91.73, -38.72) * mm, "end": v(-91.76, -38.02) * mm});
            skArc(sketch, "E16.60.1", {"start": v(-91.77, -38) * mm, "mid": v(-91.77, -38.01) * mm, "end": v(-91.76, -38.02) * mm});
            skArc(sketch, "E16.60.2", {"start": v(-92.94, -37.4) * mm, "mid": v(-92.25, -37.48) * mm, "end": v(-91.77, -38) * mm});
            skLineSegment(sketch, "E16.60.3", {"start": v(-93.23, -37.48) * mm, "end": v(-92.94, -37.4) * mm});
            skLineSegment(sketch, "E16.60.4", {"start": v(-92.43, -39.42) * mm, "end": v(-92.17, -39.27) * mm});
            skArc(sketch, "E16.61.0", {"start": v(-90.84, -42.26) * mm, "mid": v(-90.42, -41.7) * mm, "end": v(-90.47, -41) * mm});
            skArc(sketch, "E16.61.1", {"start": v(-90.48, -40.98) * mm, "mid": v(-90.47, -41) * mm, "end": v(-90.47, -41) * mm});
            skArc(sketch, "E16.61.2", {"start": v(-91.67, -40.43) * mm, "mid": v(-90.97, -40.48) * mm, "end": v(-90.48, -40.98) * mm});
            skLineSegment(sketch, "E16.61.3", {"start": v(-91.95, -40.51) * mm, "end": v(-91.67, -40.43) * mm});
            skLineSegment(sketch, "E16.61.4", {"start": v(-91.09, -42.42) * mm, "end": v(-90.84, -42.26) * mm});
            skArc(sketch, "E16.62.0", {"start": v(-89.4, -45.21) * mm, "mid": v(-89, -44.64) * mm, "end": v(-89.08, -43.94) * mm});
            skArc(sketch, "E16.62.1", {"start": v(-89.09, -43.92) * mm, "mid": v(-89.08, -43.93) * mm, "end": v(-89.08, -43.94) * mm});
            skArc(sketch, "E16.62.2", {"start": v(-90.3, -43.4) * mm, "mid": v(-89.6, -43.44) * mm, "end": v(-89.09, -43.92) * mm});
            skLineSegment(sketch, "E16.62.3", {"start": v(-90.58, -43.5) * mm, "end": v(-90.3, -43.4) * mm});
            skLineSegment(sketch, "E16.62.4", {"start": v(-89.65, -45.38) * mm, "end": v(-89.4, -45.21) * mm});
            skArc(sketch, "E16.63.0", {"start": v(-87.88, -48.11) * mm, "mid": v(-87.5, -47.53) * mm, "end": v(-87.6, -46.84) * mm});
            skArc(sketch, "E16.63.1", {"start": v(-87.6, -46.8) * mm, "mid": v(-87.6, -46.82) * mm, "end": v(-87.6, -46.84) * mm});
            skArc(sketch, "E16.63.2", {"start": v(-88.83, -46.34) * mm, "mid": v(-88.13, -46.35) * mm, "end": v(-87.6, -46.8) * mm});
            skLineSegment(sketch, "E16.63.3", {"start": v(-89.1, -46.44) * mm, "end": v(-88.83, -46.34) * mm});
            skLineSegment(sketch, "E16.63.4", {"start": v(-88.12, -48.29) * mm, "end": v(-87.88, -48.11) * mm});
            skArc(sketch, "E16.64.0", {"start": v(-86.26, -50.96) * mm, "mid": v(-85.9, -50.37) * mm, "end": v(-86.01, -49.68) * mm});
            skArc(sketch, "E16.64.1", {"start": v(-86.03, -49.65) * mm, "mid": v(-86.02, -49.66) * mm, "end": v(-86.01, -49.68) * mm});
            skArc(sketch, "E16.64.2", {"start": v(-87.27, -49.22) * mm, "mid": v(-86.57, -49.2) * mm, "end": v(-86.03, -49.65) * mm});
            skLineSegment(sketch, "E16.64.3", {"start": v(-87.54, -49.33) * mm, "end": v(-87.27, -49.22) * mm});
            skLineSegment(sketch, "E16.64.4", {"start": v(-86.49, -51.14) * mm, "end": v(-86.26, -50.96) * mm});
            skArc(sketch, "E16.65.0", {"start": v(-84.55, -53.76) * mm, "mid": v(-84.2, -53.15) * mm, "end": v(-84.34, -52.46) * mm});
            skArc(sketch, "E16.65.1", {"start": v(-84.36, -52.44) * mm, "mid": v(-84.35, -52.45) * mm, "end": v(-84.34, -52.46) * mm});
            skArc(sketch, "E16.65.2", {"start": v(-85.6, -52.05) * mm, "mid": v(-84.9, -52.01) * mm, "end": v(-84.36, -52.44) * mm});
            skLineSegment(sketch, "E16.65.3", {"start": v(-85.88, -52.17) * mm, "end": v(-85.6, -52.05) * mm});
            skLineSegment(sketch, "E16.65.4", {"start": v(-84.77, -53.95) * mm, "end": v(-84.55, -53.76) * mm});
            skArc(sketch, "E16.66.0", {"start": v(-82.74, -56.5) * mm, "mid": v(-82.42, -55.88) * mm, "end": v(-82.58, -55.2) * mm});
            skArc(sketch, "E16.66.1", {"start": v(-82.6, -55.17) * mm, "mid": v(-82.59, -55.18) * mm, "end": v(-82.58, -55.2) * mm});
            skArc(sketch, "E16.66.2", {"start": v(-83.86, -54.82) * mm, "mid": v(-83.16, -54.76) * mm, "end": v(-82.6, -55.17) * mm});
            skLineSegment(sketch, "E16.66.3", {"start": v(-84.12, -54.95) * mm, "end": v(-83.86, -54.82) * mm});
            skLineSegment(sketch, "E16.66.4", {"start": v(-82.96, -56.7) * mm, "end": v(-82.74, -56.5) * mm});
            skArc(sketch, "E16.67.0", {"start": v(-80.85, -59.17) * mm, "mid": v(-80.55, -58.54) * mm, "end": v(-80.73, -57.87) * mm});
            skArc(sketch, "E16.67.1", {"start": v(-80.75, -57.84) * mm, "mid": v(-80.74, -57.86) * mm, "end": v(-80.73, -57.87) * mm});
            skArc(sketch, "E16.67.2", {"start": v(-82.02, -57.54) * mm, "mid": v(-81.33, -57.45) * mm, "end": v(-80.75, -57.84) * mm});
            skLineSegment(sketch, "E16.67.3", {"start": v(-82.28, -57.67) * mm, "end": v(-82.02, -57.54) * mm});
            skLineSegment(sketch, "E16.67.4", {"start": v(-81.06, -59.38) * mm, "end": v(-80.85, -59.17) * mm});
            skArc(sketch, "E16.68.0", {"start": v(-78.87, -61.79) * mm, "mid": v(-78.59, -61.15) * mm, "end": v(-78.8, -60.48) * mm});
            skArc(sketch, "E16.68.1", {"start": v(-78.81, -60.45) * mm, "mid": v(-78.8, -60.47) * mm, "end": v(-78.8, -60.48) * mm});
            skArc(sketch, "E16.68.2", {"start": v(-80.1, -60.2) * mm, "mid": v(-79.4, -60.08) * mm, "end": v(-78.81, -60.45) * mm});
            skLineSegment(sketch, "E16.68.3", {"start": v(-80.35, -60.33) * mm, "end": v(-80.1, -60.2) * mm});
            skLineSegment(sketch, "E16.68.4", {"start": v(-79.07, -62) * mm, "end": v(-78.87, -61.79) * mm});
            skArc(sketch, "E16.69.0", {"start": v(-76.8, -64.33) * mm, "mid": v(-76.54, -63.69) * mm, "end": v(-76.77, -63.02) * mm});
            skArc(sketch, "E16.69.1", {"start": v(-76.79, -63) * mm, "mid": v(-76.78, -63.01) * mm, "end": v(-76.77, -63.02) * mm});
            skArc(sketch, "E16.69.2", {"start": v(-78.08, -62.78) * mm, "mid": v(-77.4, -62.65) * mm, "end": v(-76.79, -63) * mm});
            skLineSegment(sketch, "E16.69.3", {"start": v(-78.33, -62.93) * mm, "end": v(-78.08, -62.78) * mm});
            skLineSegment(sketch, "E16.69.4", {"start": v(-77, -64.55) * mm, "end": v(-76.8, -64.33) * mm});
            skArc(sketch, "E16.70.0", {"start": v(-74.66, -66.81) * mm, "mid": v(-74.42, -66.16) * mm, "end": v(-74.67, -65.5) * mm});
            skArc(sketch, "E16.70.1", {"start": v(-74.69, -65.48) * mm, "mid": v(-74.68, -65.5) * mm, "end": v(-74.67, -65.5) * mm});
            skArc(sketch, "E16.70.2", {"start": v(-75.99, -65.3) * mm, "mid": v(-75.3, -65.15) * mm, "end": v(-74.69, -65.48) * mm});
            skLineSegment(sketch, "E16.70.3", {"start": v(-76.23, -65.46) * mm, "end": v(-75.99, -65.3) * mm});
            skLineSegment(sketch, "E16.70.4", {"start": v(-74.85, -67.04) * mm, "end": v(-74.66, -66.81) * mm});
            skArc(sketch, "E16.71.0", {"start": v(-72.43, -69.22) * mm, "mid": v(-72.21, -68.55) * mm, "end": v(-72.49, -67.9) * mm});
            skArc(sketch, "E16.71.1", {"start": v(-72.5, -67.89) * mm, "mid": v(-72.5, -67.9) * mm, "end": v(-72.49, -67.9) * mm});
            skArc(sketch, "E16.71.2", {"start": v(-73.8, -67.75) * mm, "mid": v(-73.13, -67.58) * mm, "end": v(-72.5, -67.89) * mm});
            skLineSegment(sketch, "E16.71.3", {"start": v(-74.05, -67.92) * mm, "end": v(-73.8, -67.75) * mm});
            skLineSegment(sketch, "E16.71.4", {"start": v(-72.62, -69.45) * mm, "end": v(-72.43, -69.22) * mm});
            skArc(sketch, "E16.72.0", {"start": v(-70.13, -71.55) * mm, "mid": v(-69.93, -70.88) * mm, "end": v(-70.22, -70.24) * mm});
            skArc(sketch, "E16.72.1", {"start": v(-70.24, -70.22) * mm, "mid": v(-70.23, -70.23) * mm, "end": v(-70.22, -70.24) * mm});
            skArc(sketch, "E16.72.2", {"start": v(-71.55, -70.13) * mm, "mid": v(-70.88, -69.93) * mm, "end": v(-70.24, -70.22) * mm});
            skLineSegment(sketch, "E16.72.3", {"start": v(-71.79, -70.3) * mm, "end": v(-71.55, -70.13) * mm});
            skLineSegment(sketch, "E16.72.4", {"start": v(-70.3, -71.79) * mm, "end": v(-70.13, -71.55) * mm});
            skArc(sketch, "E16.73.0", {"start": v(-67.75, -73.8) * mm, "mid": v(-67.58, -73.13) * mm, "end": v(-67.89, -72.5) * mm});
            skArc(sketch, "E16.73.1", {"start": v(-67.9, -72.49) * mm, "mid": v(-67.9, -72.5) * mm, "end": v(-67.89, -72.5) * mm});
            skArc(sketch, "E16.73.2", {"start": v(-69.22, -72.43) * mm, "mid": v(-68.55, -72.21) * mm, "end": v(-67.9, -72.49) * mm});
            skLineSegment(sketch, "E16.73.3", {"start": v(-69.45, -72.62) * mm, "end": v(-69.22, -72.43) * mm});
            skLineSegment(sketch, "E16.73.4", {"start": v(-67.92, -74.05) * mm, "end": v(-67.75, -73.8) * mm});
            skArc(sketch, "E16.74.0", {"start": v(-65.3, -75.99) * mm, "mid": v(-65.15, -75.3) * mm, "end": v(-65.48, -74.69) * mm});
            skArc(sketch, "E16.74.1", {"start": v(-65.5, -74.67) * mm, "mid": v(-65.5, -74.68) * mm, "end": v(-65.48, -74.69) * mm});
            skArc(sketch, "E16.74.2", {"start": v(-66.81, -74.66) * mm, "mid": v(-66.16, -74.42) * mm, "end": v(-65.5, -74.67) * mm});
            skLineSegment(sketch, "E16.74.3", {"start": v(-67.04, -74.85) * mm, "end": v(-66.81, -74.66) * mm});
            skLineSegment(sketch, "E16.74.4", {"start": v(-65.46, -76.23) * mm, "end": v(-65.3, -75.99) * mm});
            skArc(sketch, "E16.75.0", {"start": v(-62.78, -78.08) * mm, "mid": v(-62.65, -77.4) * mm, "end": v(-63, -76.79) * mm});
            skArc(sketch, "E16.75.1", {"start": v(-63.02, -76.77) * mm, "mid": v(-63.01, -76.78) * mm, "end": v(-63, -76.79) * mm});
            skArc(sketch, "E16.75.2", {"start": v(-64.33, -76.8) * mm, "mid": v(-63.69, -76.54) * mm, "end": v(-63.02, -76.77) * mm});
            skLineSegment(sketch, "E16.75.3", {"start": v(-64.55, -77) * mm, "end": v(-64.33, -76.8) * mm});
            skLineSegment(sketch, "E16.75.4", {"start": v(-62.93, -78.33) * mm, "end": v(-62.78, -78.08) * mm});
            skArc(sketch, "E16.76.0", {"start": v(-60.2, -80.1) * mm, "mid": v(-60.08, -79.4) * mm, "end": v(-60.45, -78.81) * mm});
            skArc(sketch, "E16.76.1", {"start": v(-60.48, -78.8) * mm, "mid": v(-60.47, -78.8) * mm, "end": v(-60.45, -78.81) * mm});
            skArc(sketch, "E16.76.2", {"start": v(-61.79, -78.87) * mm, "mid": v(-61.15, -78.59) * mm, "end": v(-60.48, -78.8) * mm});
            skLineSegment(sketch, "E16.76.3", {"start": v(-62, -79.07) * mm, "end": v(-61.79, -78.87) * mm});
            skLineSegment(sketch, "E16.76.4", {"start": v(-60.33, -80.35) * mm, "end": v(-60.2, -80.1) * mm});
            skArc(sketch, "E16.77.0", {"start": v(-57.54, -82.02) * mm, "mid": v(-57.45, -81.33) * mm, "end": v(-57.84, -80.75) * mm});
            skArc(sketch, "E16.77.1", {"start": v(-57.87, -80.73) * mm, "mid": v(-57.86, -80.74) * mm, "end": v(-57.84, -80.75) * mm});
            skArc(sketch, "E16.77.2", {"start": v(-59.17, -80.85) * mm, "mid": v(-58.54, -80.55) * mm, "end": v(-57.87, -80.73) * mm});
            skLineSegment(sketch, "E16.77.3", {"start": v(-59.38, -81.06) * mm, "end": v(-59.17, -80.85) * mm});
            skLineSegment(sketch, "E16.77.4", {"start": v(-57.67, -82.28) * mm, "end": v(-57.54, -82.02) * mm});
            skArc(sketch, "E16.78.0", {"start": v(-54.82, -83.86) * mm, "mid": v(-54.76, -83.16) * mm, "end": v(-55.17, -82.6) * mm});
            skArc(sketch, "E16.78.1", {"start": v(-55.2, -82.58) * mm, "mid": v(-55.18, -82.59) * mm, "end": v(-55.17, -82.6) * mm});
            skArc(sketch, "E16.78.2", {"start": v(-56.5, -82.74) * mm, "mid": v(-55.88, -82.42) * mm, "end": v(-55.2, -82.58) * mm});
            skLineSegment(sketch, "E16.78.3", {"start": v(-56.7, -82.96) * mm, "end": v(-56.5, -82.74) * mm});
            skLineSegment(sketch, "E16.78.4", {"start": v(-54.95, -84.12) * mm, "end": v(-54.82, -83.86) * mm});
            skArc(sketch, "E16.79.0", {"start": v(-52.05, -85.6) * mm, "mid": v(-52.01, -84.9) * mm, "end": v(-52.44, -84.36) * mm});
            skArc(sketch, "E16.79.1", {"start": v(-52.46, -84.34) * mm, "mid": v(-52.45, -84.35) * mm, "end": v(-52.44, -84.36) * mm});
            skArc(sketch, "E16.79.2", {"start": v(-53.76, -84.55) * mm, "mid": v(-53.15, -84.2) * mm, "end": v(-52.46, -84.34) * mm});
            skLineSegment(sketch, "E16.79.3", {"start": v(-53.95, -84.77) * mm, "end": v(-53.76, -84.55) * mm});
            skLineSegment(sketch, "E16.79.4", {"start": v(-52.17, -85.88) * mm, "end": v(-52.05, -85.6) * mm});
            skArc(sketch, "E16.80.0", {"start": v(-49.22, -87.27) * mm, "mid": v(-49.2, -86.57) * mm, "end": v(-49.65, -86.03) * mm});
            skArc(sketch, "E16.80.1", {"start": v(-49.68, -86.01) * mm, "mid": v(-49.66, -86.02) * mm, "end": v(-49.65, -86.03) * mm});
            skArc(sketch, "E16.80.2", {"start": v(-50.96, -86.26) * mm, "mid": v(-50.37, -85.9) * mm, "end": v(-49.68, -86.01) * mm});
            skLineSegment(sketch, "E16.80.3", {"start": v(-51.14, -86.49) * mm, "end": v(-50.96, -86.26) * mm});
            skLineSegment(sketch, "E16.80.4", {"start": v(-49.33, -87.54) * mm, "end": v(-49.22, -87.27) * mm});
            skArc(sketch, "E16.81.0", {"start": v(-46.34, -88.83) * mm, "mid": v(-46.35, -88.13) * mm, "end": v(-46.8, -87.6) * mm});
            skArc(sketch, "E16.81.1", {"start": v(-46.84, -87.6) * mm, "mid": v(-46.82, -87.6) * mm, "end": v(-46.8, -87.6) * mm});
            skArc(sketch, "E16.81.2", {"start": v(-48.11, -87.88) * mm, "mid": v(-47.53, -87.5) * mm, "end": v(-46.84, -87.6) * mm});
            skLineSegment(sketch, "E16.81.3", {"start": v(-48.29, -88.12) * mm, "end": v(-48.11, -87.88) * mm});
            skLineSegment(sketch, "E16.81.4", {"start": v(-46.44, -89.1) * mm, "end": v(-46.34, -88.83) * mm});
            skArc(sketch, "E16.82.0", {"start": v(-43.4, -90.3) * mm, "mid": v(-43.44, -89.6) * mm, "end": v(-43.92, -89.09) * mm});
            skArc(sketch, "E16.82.1", {"start": v(-43.94, -89.08) * mm, "mid": v(-43.93, -89.08) * mm, "end": v(-43.92, -89.09) * mm});
            skArc(sketch, "E16.82.2", {"start": v(-45.21, -89.4) * mm, "mid": v(-44.64, -89) * mm, "end": v(-43.94, -89.08) * mm});
            skLineSegment(sketch, "E16.82.3", {"start": v(-45.38, -89.65) * mm, "end": v(-45.21, -89.4) * mm});
            skLineSegment(sketch, "E16.82.4", {"start": v(-43.5, -90.58) * mm, "end": v(-43.4, -90.3) * mm});
            skArc(sketch, "E16.83.0", {"start": v(-40.43, -91.67) * mm, "mid": v(-40.48, -90.97) * mm, "end": v(-40.98, -90.48) * mm});
            skArc(sketch, "E16.83.1", {"start": v(-41, -90.47) * mm, "mid": v(-41, -90.47) * mm, "end": v(-40.98, -90.48) * mm});
            skArc(sketch, "E16.83.2", {"start": v(-42.26, -90.84) * mm, "mid": v(-41.7, -90.42) * mm, "end": v(-41, -90.47) * mm});
            skLineSegment(sketch, "E16.83.3", {"start": v(-42.42, -91.09) * mm, "end": v(-42.26, -90.84) * mm});
            skLineSegment(sketch, "E16.83.4", {"start": v(-40.51, -91.95) * mm, "end": v(-40.43, -91.67) * mm});
            skArc(sketch, "E16.84.0", {"start": v(-37.4, -92.94) * mm, "mid": v(-37.48, -92.25) * mm, "end": v(-38, -91.77) * mm});
            skArc(sketch, "E16.84.1", {"start": v(-38.02, -91.76) * mm, "mid": v(-38.01, -91.77) * mm, "end": v(-38, -91.77) * mm});
            skArc(sketch, "E16.84.2", {"start": v(-39.27, -92.17) * mm, "mid": v(-38.72, -91.73) * mm, "end": v(-38.02, -91.76) * mm});
            skLineSegment(sketch, "E16.84.3", {"start": v(-39.42, -92.43) * mm, "end": v(-39.27, -92.17) * mm});
            skLineSegment(sketch, "E16.84.4", {"start": v(-37.48, -93.23) * mm, "end": v(-37.4, -92.94) * mm});
            skArc(sketch, "E16.85.0", {"start": v(-34.35, -94.12) * mm, "mid": v(-34.45, -93.42) * mm, "end": v(-34.97, -92.97) * mm});
            skArc(sketch, "E16.85.1", {"start": v(-35, -92.96) * mm, "mid": v(-34.99, -92.96) * mm, "end": v(-34.97, -92.97) * mm});
            skArc(sketch, "E16.85.2", {"start": v(-36.23, -93.4) * mm, "mid": v(-35.7, -92.95) * mm, "end": v(-35, -92.96) * mm});
            skLineSegment(sketch, "E16.85.3", {"start": v(-36.37, -93.67) * mm, "end": v(-36.23, -93.4) * mm});
            skLineSegment(sketch, "E16.85.4", {"start": v(-34.41, -94.4) * mm, "end": v(-34.35, -94.12) * mm});
            skArc(sketch, "E16.86.0", {"start": v(-31.25, -95.2) * mm, "mid": v(-31.37, -94.5) * mm, "end": v(-31.91, -94.06) * mm});
            skArc(sketch, "E16.86.1", {"start": v(-31.94, -94.05) * mm, "mid": v(-31.93, -94.06) * mm, "end": v(-31.91, -94.06) * mm});
            skArc(sketch, "E16.86.2", {"start": v(-33.16, -94.54) * mm, "mid": v(-32.64, -94.07) * mm, "end": v(-31.94, -94.05) * mm});
            skLineSegment(sketch, "E16.86.3", {"start": v(-33.29, -94.8) * mm, "end": v(-33.16, -94.54) * mm});
            skLineSegment(sketch, "E16.86.4", {"start": v(-31.3, -95.48) * mm, "end": v(-31.25, -95.2) * mm});
            skArc(sketch, "E16.87.0", {"start": v(-28.12, -96.16) * mm, "mid": v(-28.26, -95.48) * mm, "end": v(-28.82, -95.05) * mm});
            skArc(sketch, "E16.87.1", {"start": v(-28.85, -95.05) * mm, "mid": v(-28.83, -95.05) * mm, "end": v(-28.82, -95.05) * mm});
            skArc(sketch, "E16.87.2", {"start": v(-30.04, -95.58) * mm, "mid": v(-29.55, -95.09) * mm, "end": v(-28.85, -95.05) * mm});
            skLineSegment(sketch, "E16.87.3", {"start": v(-30.17, -95.84) * mm, "end": v(-30.04, -95.58) * mm});
            skLineSegment(sketch, "E16.87.4", {"start": v(-28.16, -96.45) * mm, "end": v(-28.12, -96.16) * mm});
            skArc(sketch, "E16.88.0", {"start": v(-24.96, -97.03) * mm, "mid": v(-25.12, -96.35) * mm, "end": v(-25.7, -95.95) * mm});
            skArc(sketch, "E16.88.1", {"start": v(-25.72, -95.94) * mm, "mid": v(-25.7, -95.94) * mm, "end": v(-25.7, -95.95) * mm});
            skArc(sketch, "E16.88.2", {"start": v(-26.9, -96.51) * mm, "mid": v(-26.42, -96) * mm, "end": v(-25.72, -95.94) * mm});
            skLineSegment(sketch, "E16.88.3", {"start": v(-27.02, -96.78) * mm, "end": v(-26.9, -96.51) * mm});
            skLineSegment(sketch, "E16.88.4", {"start": v(-25, -97.32) * mm, "end": v(-24.96, -97.03) * mm});
            skArc(sketch, "E16.89.0", {"start": v(-21.77, -97.8) * mm, "mid": v(-21.96, -97.12) * mm, "end": v(-22.54, -96.74) * mm});
            skArc(sketch, "E16.89.1", {"start": v(-22.57, -96.73) * mm, "mid": v(-22.55, -96.73) * mm, "end": v(-22.54, -96.74) * mm});
            skArc(sketch, "E16.89.2", {"start": v(-23.73, -97.34) * mm, "mid": v(-23.26, -96.82) * mm, "end": v(-22.57, -96.73) * mm});
            skLineSegment(sketch, "E16.89.3", {"start": v(-23.84, -97.61) * mm, "end": v(-23.73, -97.34) * mm});
            skLineSegment(sketch, "E16.89.4", {"start": v(-21.8, -98.09) * mm, "end": v(-21.77, -97.8) * mm});
            skArc(sketch, "E16.90.0", {"start": v(-18.56, -98.46) * mm, "mid": v(-18.77, -97.79) * mm, "end": v(-19.36, -97.42) * mm});
            skArc(sketch, "E16.90.1", {"start": v(-19.4, -97.42) * mm, "mid": v(-19.38, -97.42) * mm, "end": v(-19.36, -97.42) * mm});
            skArc(sketch, "E16.90.2", {"start": v(-20.53, -98.06) * mm, "mid": v(-20.08, -97.53) * mm, "end": v(-19.4, -97.42) * mm});
            skLineSegment(sketch, "E16.90.3", {"start": v(-20.63, -98.34) * mm, "end": v(-20.53, -98.06) * mm});
            skLineSegment(sketch, "E16.90.4", {"start": v(-18.57, -98.75) * mm, "end": v(-18.56, -98.46) * mm});
            skArc(sketch, "E16.91.0", {"start": v(-15.33, -99.01) * mm, "mid": v(-15.56, -98.35) * mm, "end": v(-16.17, -98) * mm});
            skArc(sketch, "E16.91.1", {"start": v(-16.2, -98) * mm, "mid": v(-16.18, -98) * mm, "end": v(-16.17, -98) * mm});
            skArc(sketch, "E16.91.2", {"start": v(-17.31, -98.68) * mm, "mid": v(-16.88, -98.13) * mm, "end": v(-16.2, -98) * mm});
            skLineSegment(sketch, "E16.91.3", {"start": v(-17.4, -98.96) * mm, "end": v(-17.31, -98.68) * mm});
            skLineSegment(sketch, "E16.91.4", {"start": v(-15.33, -99.3) * mm, "end": v(-15.33, -99.01) * mm});
            skArc(sketch, "E16.92.0", {"start": v(-12.08, -99.46) * mm, "mid": v(-12.33, -98.8) * mm, "end": v(-12.95, -98.48) * mm});
            skArc(sketch, "E16.92.1", {"start": v(-12.98, -98.48) * mm, "mid": v(-12.96, -98.48) * mm, "end": v(-12.95, -98.48) * mm});
            skArc(sketch, "E16.92.2", {"start": v(-14.07, -99.2) * mm, "mid": v(-13.66, -98.63) * mm, "end": v(-12.98, -98.48) * mm});
            skLineSegment(sketch, "E16.92.3", {"start": v(-14.15, -99.48) * mm, "end": v(-14.07, -99.2) * mm});
            skLineSegment(sketch, "E16.92.4", {"start": v(-12.08, -99.75) * mm, "end": v(-12.08, -99.46) * mm});
            skArc(sketch, "E16.93.0", {"start": v(-8.82, -99.8) * mm, "mid": v(-9.1, -99.16) * mm, "end": v(-9.72, -98.85) * mm});
            skArc(sketch, "E16.93.1", {"start": v(-9.75, -98.85) * mm, "mid": v(-9.74, -98.85) * mm, "end": v(-9.72, -98.85) * mm});
            skArc(sketch, "E16.93.2", {"start": v(-10.82, -99.6) * mm, "mid": v(-10.43, -99.03) * mm, "end": v(-9.75, -98.85) * mm});
            skLineSegment(sketch, "E16.93.3", {"start": v(-10.9, -99.89) * mm, "end": v(-10.82, -99.6) * mm});
            skLineSegment(sketch, "E16.93.4", {"start": v(-8.8, -100.1) * mm, "end": v(-8.82, -99.8) * mm});
            skArc(sketch, "E16.94.0", {"start": v(-5.55, -100.04) * mm, "mid": v(-5.84, -99.4) * mm, "end": v(-6.48, -99.12) * mm});
            skArc(sketch, "E16.94.1", {"start": v(-6.51, -99.11) * mm, "mid": v(-6.5, -99.11) * mm, "end": v(-6.48, -99.12) * mm});
            skArc(sketch, "E16.94.2", {"start": v(-7.56, -99.9) * mm, "mid": v(-7.18, -99.31) * mm, "end": v(-6.51, -99.11) * mm});
            skLineSegment(sketch, "E16.94.3", {"start": v(-7.62, -100.2) * mm, "end": v(-7.56, -99.9) * mm});
            skLineSegment(sketch, "E16.94.4", {"start": v(-5.53, -100.33) * mm, "end": v(-5.55, -100.04) * mm});
            skArc(sketch, "E16.95.0", {"start": v(-2.27, -100.16) * mm, "mid": v(-2.59, -99.54) * mm, "end": v(-3.24, -99.27) * mm});
            skArc(sketch, "E16.95.1", {"start": v(-3.26, -99.27) * mm, "mid": v(-3.25, -99.27) * mm, "end": v(-3.24, -99.27) * mm});
            skArc(sketch, "E16.95.2", {"start": v(-4.28, -100.1) * mm, "mid": v(-3.93, -99.5) * mm, "end": v(-3.26, -99.27) * mm});
            skLineSegment(sketch, "E16.95.3", {"start": v(-4.33, -100.39) * mm, "end": v(-4.28, -100.1) * mm});
            skLineSegment(sketch, "E16.95.4", {"start": v(-2.24, -100.46) * mm, "end": v(-2.27, -100.16) * mm});
            skArc(sketch, "E16.96.0", {"start": v(1, -100.18) * mm, "mid": v(0.67, -99.57) * mm, "end": v(0.01, -99.33) * mm});
            skArc(sketch, "E16.96.1", {"start": v(-0.01, -99.33) * mm, "mid": v(0, -99.33) * mm, "end": v(0.01, -99.33) * mm});
            skArc(sketch, "E16.96.2", {"start": v(-1, -100.18) * mm, "mid": v(-0.67, -99.57) * mm, "end": v(-0.01, -99.33) * mm});
            skLineSegment(sketch, "E16.96.3", {"start": v(-1.05, -100.47) * mm, "end": v(-1, -100.18) * mm});
            skLineSegment(sketch, "E16.96.4", {"start": v(1.05, -100.47) * mm, "end": v(1, -100.18) * mm});
            skArc(sketch, "E16.97.0", {"start": v(4.28, -100.1) * mm, "mid": v(3.93, -99.5) * mm, "end": v(3.26, -99.27) * mm});
            skArc(sketch, "E16.97.1", {"start": v(3.24, -99.27) * mm, "mid": v(3.25, -99.27) * mm, "end": v(3.26, -99.27) * mm});
            skArc(sketch, "E16.97.2", {"start": v(2.27, -100.16) * mm, "mid": v(2.59, -99.54) * mm, "end": v(3.24, -99.27) * mm});
            skLineSegment(sketch, "E16.97.3", {"start": v(2.24, -100.46) * mm, "end": v(2.27, -100.16) * mm});
            skLineSegment(sketch, "E16.97.4", {"start": v(4.33, -100.39) * mm, "end": v(4.28, -100.1) * mm});
            skArc(sketch, "E16.98.0", {"start": v(7.56, -99.9) * mm, "mid": v(7.18, -99.31) * mm, "end": v(6.51, -99.11) * mm});
            skArc(sketch, "E16.98.1", {"start": v(6.48, -99.12) * mm, "mid": v(6.5, -99.11) * mm, "end": v(6.51, -99.11) * mm});
            skArc(sketch, "E16.98.2", {"start": v(5.55, -100.04) * mm, "mid": v(5.84, -99.4) * mm, "end": v(6.48, -99.12) * mm});
            skLineSegment(sketch, "E16.98.3", {"start": v(5.53, -100.33) * mm, "end": v(5.55, -100.04) * mm});
            skLineSegment(sketch, "E16.98.4", {"start": v(7.62, -100.2) * mm, "end": v(7.56, -99.9) * mm});
            skArc(sketch, "E16.99.0", {"start": v(10.82, -99.6) * mm, "mid": v(10.43, -99.03) * mm, "end": v(9.75, -98.85) * mm});
            skArc(sketch, "E16.99.1", {"start": v(9.72, -98.85) * mm, "mid": v(9.74, -98.85) * mm, "end": v(9.75, -98.85) * mm});
            skArc(sketch, "E16.99.2", {"start": v(8.82, -99.8) * mm, "mid": v(9.1, -99.16) * mm, "end": v(9.72, -98.85) * mm});
            skLineSegment(sketch, "E16.99.3", {"start": v(8.8, -100.1) * mm, "end": v(8.82, -99.8) * mm});
            skLineSegment(sketch, "E16.99.4", {"start": v(10.9, -99.89) * mm, "end": v(10.82, -99.6) * mm});
            skArc(sketch, "E16.100.0", {"start": v(14.07, -99.2) * mm, "mid": v(13.66, -98.63) * mm, "end": v(12.98, -98.48) * mm});
            skArc(sketch, "E16.100.1", {"start": v(12.95, -98.48) * mm, "mid": v(12.96, -98.48) * mm, "end": v(12.98, -98.48) * mm});
            skArc(sketch, "E16.100.2", {"start": v(12.08, -99.46) * mm, "mid": v(12.33, -98.8) * mm, "end": v(12.95, -98.48) * mm});
            skLineSegment(sketch, "E16.100.3", {"start": v(12.08, -99.75) * mm, "end": v(12.08, -99.46) * mm});
            skLineSegment(sketch, "E16.100.4", {"start": v(14.15, -99.48) * mm, "end": v(14.07, -99.2) * mm});
            skArc(sketch, "E16.101.0", {"start": v(17.31, -98.68) * mm, "mid": v(16.88, -98.13) * mm, "end": v(16.2, -98) * mm});
            skArc(sketch, "E16.101.1", {"start": v(16.17, -98) * mm, "mid": v(16.18, -98) * mm, "end": v(16.2, -98) * mm});
            skArc(sketch, "E16.101.2", {"start": v(15.33, -99.01) * mm, "mid": v(15.56, -98.35) * mm, "end": v(16.17, -98) * mm});
            skLineSegment(sketch, "E16.101.3", {"start": v(15.33, -99.3) * mm, "end": v(15.33, -99.01) * mm});
            skLineSegment(sketch, "E16.101.4", {"start": v(17.4, -98.96) * mm, "end": v(17.31, -98.68) * mm});
            skArc(sketch, "E16.102.0", {"start": v(20.53, -98.06) * mm, "mid": v(20.08, -97.53) * mm, "end": v(19.4, -97.42) * mm});
            skArc(sketch, "E16.102.1", {"start": v(19.36, -97.42) * mm, "mid": v(19.38, -97.42) * mm, "end": v(19.4, -97.42) * mm});
            skArc(sketch, "E16.102.2", {"start": v(18.56, -98.46) * mm, "mid": v(18.77, -97.79) * mm, "end": v(19.36, -97.42) * mm});
            skLineSegment(sketch, "E16.102.3", {"start": v(18.57, -98.75) * mm, "end": v(18.56, -98.46) * mm});
            skLineSegment(sketch, "E16.102.4", {"start": v(20.63, -98.34) * mm, "end": v(20.53, -98.06) * mm});
            skArc(sketch, "E16.103.0", {"start": v(23.73, -97.34) * mm, "mid": v(23.26, -96.82) * mm, "end": v(22.57, -96.73) * mm});
            skArc(sketch, "E16.103.1", {"start": v(22.54, -96.74) * mm, "mid": v(22.55, -96.73) * mm, "end": v(22.57, -96.73) * mm});
            skArc(sketch, "E16.103.2", {"start": v(21.77, -97.8) * mm, "mid": v(21.96, -97.12) * mm, "end": v(22.54, -96.74) * mm});
            skLineSegment(sketch, "E16.103.3", {"start": v(21.8, -98.09) * mm, "end": v(21.77, -97.8) * mm});
            skLineSegment(sketch, "E16.103.4", {"start": v(23.84, -97.61) * mm, "end": v(23.73, -97.34) * mm});
            skArc(sketch, "E16.104.0", {"start": v(26.9, -96.51) * mm, "mid": v(26.42, -96) * mm, "end": v(25.72, -95.94) * mm});
            skArc(sketch, "E16.104.1", {"start": v(25.7, -95.95) * mm, "mid": v(25.7, -95.94) * mm, "end": v(25.72, -95.94) * mm});
            skArc(sketch, "E16.104.2", {"start": v(24.96, -97.03) * mm, "mid": v(25.12, -96.35) * mm, "end": v(25.7, -95.95) * mm});
            skLineSegment(sketch, "E16.104.3", {"start": v(25, -97.32) * mm, "end": v(24.96, -97.03) * mm});
            skLineSegment(sketch, "E16.104.4", {"start": v(27.02, -96.78) * mm, "end": v(26.9, -96.51) * mm});
            skArc(sketch, "E16.105.0", {"start": v(30.04, -95.58) * mm, "mid": v(29.55, -95.09) * mm, "end": v(28.85, -95.05) * mm});
            skArc(sketch, "E16.105.1", {"start": v(28.82, -95.05) * mm, "mid": v(28.83, -95.05) * mm, "end": v(28.85, -95.05) * mm});
            skArc(sketch, "E16.105.2", {"start": v(28.12, -96.16) * mm, "mid": v(28.26, -95.48) * mm, "end": v(28.82, -95.05) * mm});
            skLineSegment(sketch, "E16.105.3", {"start": v(28.16, -96.45) * mm, "end": v(28.12, -96.16) * mm});
            skLineSegment(sketch, "E16.105.4", {"start": v(30.17, -95.84) * mm, "end": v(30.04, -95.58) * mm});
            skArc(sketch, "E16.106.0", {"start": v(33.16, -94.54) * mm, "mid": v(32.64, -94.07) * mm, "end": v(31.94, -94.05) * mm});
            skArc(sketch, "E16.106.1", {"start": v(31.91, -94.06) * mm, "mid": v(31.93, -94.06) * mm, "end": v(31.94, -94.05) * mm});
            skArc(sketch, "E16.106.2", {"start": v(31.25, -95.2) * mm, "mid": v(31.37, -94.5) * mm, "end": v(31.91, -94.06) * mm});
            skLineSegment(sketch, "E16.106.3", {"start": v(31.3, -95.48) * mm, "end": v(31.25, -95.2) * mm});
            skLineSegment(sketch, "E16.106.4", {"start": v(33.29, -94.8) * mm, "end": v(33.16, -94.54) * mm});
            skArc(sketch, "E16.107.0", {"start": v(36.23, -93.4) * mm, "mid": v(35.7, -92.95) * mm, "end": v(35, -92.96) * mm});
            skArc(sketch, "E16.107.1", {"start": v(34.97, -92.97) * mm, "mid": v(34.99, -92.96) * mm, "end": v(35, -92.96) * mm});
            skArc(sketch, "E16.107.2", {"start": v(34.35, -94.12) * mm, "mid": v(34.45, -93.42) * mm, "end": v(34.97, -92.97) * mm});
            skLineSegment(sketch, "E16.107.3", {"start": v(34.41, -94.4) * mm, "end": v(34.35, -94.12) * mm});
            skLineSegment(sketch, "E16.107.4", {"start": v(36.37, -93.67) * mm, "end": v(36.23, -93.4) * mm});
            skArc(sketch, "E16.108.0", {"start": v(39.27, -92.17) * mm, "mid": v(38.72, -91.73) * mm, "end": v(38.02, -91.76) * mm});
            skArc(sketch, "E16.108.1", {"start": v(38, -91.77) * mm, "mid": v(38.01, -91.77) * mm, "end": v(38.02, -91.76) * mm});
            skArc(sketch, "E16.108.2", {"start": v(37.4, -92.94) * mm, "mid": v(37.48, -92.25) * mm, "end": v(38, -91.77) * mm});
            skLineSegment(sketch, "E16.108.3", {"start": v(37.48, -93.23) * mm, "end": v(37.4, -92.94) * mm});
            skLineSegment(sketch, "E16.108.4", {"start": v(39.42, -92.43) * mm, "end": v(39.27, -92.17) * mm});
            skArc(sketch, "E16.109.0", {"start": v(42.26, -90.84) * mm, "mid": v(41.7, -90.42) * mm, "end": v(41, -90.47) * mm});
            skArc(sketch, "E16.109.1", {"start": v(40.98, -90.48) * mm, "mid": v(41, -90.47) * mm, "end": v(41, -90.47) * mm});
            skArc(sketch, "E16.109.2", {"start": v(40.43, -91.67) * mm, "mid": v(40.48, -90.97) * mm, "end": v(40.98, -90.48) * mm});
            skLineSegment(sketch, "E16.109.3", {"start": v(40.51, -91.95) * mm, "end": v(40.43, -91.67) * mm});
            skLineSegment(sketch, "E16.109.4", {"start": v(42.42, -91.09) * mm, "end": v(42.26, -90.84) * mm});
            skArc(sketch, "E16.110.0", {"start": v(45.21, -89.4) * mm, "mid": v(44.64, -89) * mm, "end": v(43.94, -89.08) * mm});
            skArc(sketch, "E16.110.1", {"start": v(43.92, -89.09) * mm, "mid": v(43.93, -89.08) * mm, "end": v(43.94, -89.08) * mm});
            skArc(sketch, "E16.110.2", {"start": v(43.4, -90.3) * mm, "mid": v(43.44, -89.6) * mm, "end": v(43.92, -89.09) * mm});
            skLineSegment(sketch, "E16.110.3", {"start": v(43.5, -90.58) * mm, "end": v(43.4, -90.3) * mm});
            skLineSegment(sketch, "E16.110.4", {"start": v(45.38, -89.65) * mm, "end": v(45.21, -89.4) * mm});
            skArc(sketch, "E16.111.0", {"start": v(48.11, -87.88) * mm, "mid": v(47.53, -87.5) * mm, "end": v(46.84, -87.6) * mm});
            skArc(sketch, "E16.111.1", {"start": v(46.8, -87.6) * mm, "mid": v(46.82, -87.6) * mm, "end": v(46.84, -87.6) * mm});
            skArc(sketch, "E16.111.2", {"start": v(46.34, -88.83) * mm, "mid": v(46.35, -88.13) * mm, "end": v(46.8, -87.6) * mm});
            skLineSegment(sketch, "E16.111.3", {"start": v(46.44, -89.1) * mm, "end": v(46.34, -88.83) * mm});
            skLineSegment(sketch, "E16.111.4", {"start": v(48.29, -88.12) * mm, "end": v(48.11, -87.88) * mm});
            skArc(sketch, "E16.112.0", {"start": v(50.96, -86.26) * mm, "mid": v(50.37, -85.9) * mm, "end": v(49.68, -86.01) * mm});
            skArc(sketch, "E16.112.1", {"start": v(49.65, -86.03) * mm, "mid": v(49.66, -86.02) * mm, "end": v(49.68, -86.01) * mm});
            skArc(sketch, "E16.112.2", {"start": v(49.22, -87.27) * mm, "mid": v(49.2, -86.57) * mm, "end": v(49.65, -86.03) * mm});
            skLineSegment(sketch, "E16.112.3", {"start": v(49.33, -87.54) * mm, "end": v(49.22, -87.27) * mm});
            skLineSegment(sketch, "E16.112.4", {"start": v(51.14, -86.49) * mm, "end": v(50.96, -86.26) * mm});
            skArc(sketch, "E16.113.0", {"start": v(53.76, -84.55) * mm, "mid": v(53.15, -84.2) * mm, "end": v(52.46, -84.34) * mm});
            skArc(sketch, "E16.113.1", {"start": v(52.44, -84.36) * mm, "mid": v(52.45, -84.35) * mm, "end": v(52.46, -84.34) * mm});
            skArc(sketch, "E16.113.2", {"start": v(52.05, -85.6) * mm, "mid": v(52.01, -84.9) * mm, "end": v(52.44, -84.36) * mm});
            skLineSegment(sketch, "E16.113.3", {"start": v(52.17, -85.88) * mm, "end": v(52.05, -85.6) * mm});
            skLineSegment(sketch, "E16.113.4", {"start": v(53.95, -84.77) * mm, "end": v(53.76, -84.55) * mm});
            skArc(sketch, "E16.114.0", {"start": v(56.5, -82.74) * mm, "mid": v(55.88, -82.42) * mm, "end": v(55.2, -82.58) * mm});
            skArc(sketch, "E16.114.1", {"start": v(55.17, -82.6) * mm, "mid": v(55.18, -82.59) * mm, "end": v(55.2, -82.58) * mm});
            skArc(sketch, "E16.114.2", {"start": v(54.82, -83.86) * mm, "mid": v(54.76, -83.16) * mm, "end": v(55.17, -82.6) * mm});
            skLineSegment(sketch, "E16.114.3", {"start": v(54.95, -84.12) * mm, "end": v(54.82, -83.86) * mm});
            skLineSegment(sketch, "E16.114.4", {"start": v(56.7, -82.96) * mm, "end": v(56.5, -82.74) * mm});
            skArc(sketch, "E16.115.0", {"start": v(59.17, -80.85) * mm, "mid": v(58.54, -80.55) * mm, "end": v(57.87, -80.73) * mm});
            skArc(sketch, "E16.115.1", {"start": v(57.84, -80.75) * mm, "mid": v(57.86, -80.74) * mm, "end": v(57.87, -80.73) * mm});
            skArc(sketch, "E16.115.2", {"start": v(57.54, -82.02) * mm, "mid": v(57.45, -81.33) * mm, "end": v(57.84, -80.75) * mm});
            skLineSegment(sketch, "E16.115.3", {"start": v(57.67, -82.28) * mm, "end": v(57.54, -82.02) * mm});
            skLineSegment(sketch, "E16.115.4", {"start": v(59.38, -81.06) * mm, "end": v(59.17, -80.85) * mm});
            skArc(sketch, "E16.116.0", {"start": v(61.79, -78.87) * mm, "mid": v(61.15, -78.59) * mm, "end": v(60.48, -78.8) * mm});
            skArc(sketch, "E16.116.1", {"start": v(60.45, -78.81) * mm, "mid": v(60.47, -78.8) * mm, "end": v(60.48, -78.8) * mm});
            skArc(sketch, "E16.116.2", {"start": v(60.2, -80.1) * mm, "mid": v(60.08, -79.4) * mm, "end": v(60.45, -78.81) * mm});
            skLineSegment(sketch, "E16.116.3", {"start": v(60.33, -80.35) * mm, "end": v(60.2, -80.1) * mm});
            skLineSegment(sketch, "E16.116.4", {"start": v(62, -79.07) * mm, "end": v(61.79, -78.87) * mm});
            skArc(sketch, "E16.117.0", {"start": v(64.33, -76.8) * mm, "mid": v(63.69, -76.54) * mm, "end": v(63.02, -76.77) * mm});
            skArc(sketch, "E16.117.1", {"start": v(63, -76.79) * mm, "mid": v(63.01, -76.78) * mm, "end": v(63.02, -76.77) * mm});
            skArc(sketch, "E16.117.2", {"start": v(62.78, -78.08) * mm, "mid": v(62.65, -77.4) * mm, "end": v(63, -76.79) * mm});
            skLineSegment(sketch, "E16.117.3", {"start": v(62.93, -78.33) * mm, "end": v(62.78, -78.08) * mm});
            skLineSegment(sketch, "E16.117.4", {"start": v(64.55, -77) * mm, "end": v(64.33, -76.8) * mm});
            skArc(sketch, "E16.118.0", {"start": v(66.81, -74.66) * mm, "mid": v(66.16, -74.42) * mm, "end": v(65.5, -74.67) * mm});
            skArc(sketch, "E16.118.1", {"start": v(65.48, -74.69) * mm, "mid": v(65.5, -74.68) * mm, "end": v(65.5, -74.67) * mm});
            skArc(sketch, "E16.118.2", {"start": v(65.3, -75.99) * mm, "mid": v(65.15, -75.3) * mm, "end": v(65.48, -74.69) * mm});
            skLineSegment(sketch, "E16.118.3", {"start": v(65.46, -76.23) * mm, "end": v(65.3, -75.99) * mm});
            skLineSegment(sketch, "E16.118.4", {"start": v(67.04, -74.85) * mm, "end": v(66.81, -74.66) * mm});
            skArc(sketch, "E16.119.0", {"start": v(69.22, -72.43) * mm, "mid": v(68.55, -72.21) * mm, "end": v(67.9, -72.49) * mm});
            skArc(sketch, "E16.119.1", {"start": v(67.89, -72.5) * mm, "mid": v(67.9, -72.5) * mm, "end": v(67.9, -72.49) * mm});
            skArc(sketch, "E16.119.2", {"start": v(67.75, -73.8) * mm, "mid": v(67.58, -73.13) * mm, "end": v(67.89, -72.5) * mm});
            skLineSegment(sketch, "E16.119.3", {"start": v(67.92, -74.05) * mm, "end": v(67.75, -73.8) * mm});
            skLineSegment(sketch, "E16.119.4", {"start": v(69.45, -72.62) * mm, "end": v(69.22, -72.43) * mm});
            skArc(sketch, "E16.120.0", {"start": v(71.55, -70.13) * mm, "mid": v(70.88, -69.93) * mm, "end": v(70.24, -70.22) * mm});
            skArc(sketch, "E16.120.1", {"start": v(70.22, -70.24) * mm, "mid": v(70.23, -70.23) * mm, "end": v(70.24, -70.22) * mm});
            skArc(sketch, "E16.120.2", {"start": v(70.13, -71.55) * mm, "mid": v(69.93, -70.88) * mm, "end": v(70.22, -70.24) * mm});
            skLineSegment(sketch, "E16.120.3", {"start": v(70.3, -71.79) * mm, "end": v(70.13, -71.55) * mm});
            skLineSegment(sketch, "E16.120.4", {"start": v(71.79, -70.3) * mm, "end": v(71.55, -70.13) * mm});
            skArc(sketch, "E16.121.0", {"start": v(73.8, -67.75) * mm, "mid": v(73.13, -67.58) * mm, "end": v(72.5, -67.89) * mm});
            skArc(sketch, "E16.121.1", {"start": v(72.49, -67.9) * mm, "mid": v(72.5, -67.9) * mm, "end": v(72.5, -67.89) * mm});
            skArc(sketch, "E16.121.2", {"start": v(72.43, -69.22) * mm, "mid": v(72.21, -68.55) * mm, "end": v(72.49, -67.9) * mm});
            skLineSegment(sketch, "E16.121.3", {"start": v(72.62, -69.45) * mm, "end": v(72.43, -69.22) * mm});
            skLineSegment(sketch, "E16.121.4", {"start": v(74.05, -67.92) * mm, "end": v(73.8, -67.75) * mm});
            skArc(sketch, "E16.122.0", {"start": v(75.99, -65.3) * mm, "mid": v(75.3, -65.15) * mm, "end": v(74.69, -65.48) * mm});
            skArc(sketch, "E16.122.1", {"start": v(74.67, -65.5) * mm, "mid": v(74.68, -65.5) * mm, "end": v(74.69, -65.48) * mm});
            skArc(sketch, "E16.122.2", {"start": v(74.66, -66.81) * mm, "mid": v(74.42, -66.16) * mm, "end": v(74.67, -65.5) * mm});
            skLineSegment(sketch, "E16.122.3", {"start": v(74.85, -67.04) * mm, "end": v(74.66, -66.81) * mm});
            skLineSegment(sketch, "E16.122.4", {"start": v(76.23, -65.46) * mm, "end": v(75.99, -65.3) * mm});
            skArc(sketch, "E16.123.0", {"start": v(78.08, -62.78) * mm, "mid": v(77.4, -62.65) * mm, "end": v(76.79, -63) * mm});
            skArc(sketch, "E16.123.1", {"start": v(76.77, -63.02) * mm, "mid": v(76.78, -63.01) * mm, "end": v(76.79, -63) * mm});
            skArc(sketch, "E16.123.2", {"start": v(76.8, -64.33) * mm, "mid": v(76.54, -63.69) * mm, "end": v(76.77, -63.02) * mm});
            skLineSegment(sketch, "E16.123.3", {"start": v(77, -64.55) * mm, "end": v(76.8, -64.33) * mm});
            skLineSegment(sketch, "E16.123.4", {"start": v(78.33, -62.93) * mm, "end": v(78.08, -62.78) * mm});
            skArc(sketch, "E16.124.0", {"start": v(80.1, -60.2) * mm, "mid": v(79.4, -60.08) * mm, "end": v(78.81, -60.45) * mm});
            skArc(sketch, "E16.124.1", {"start": v(78.8, -60.48) * mm, "mid": v(78.8, -60.47) * mm, "end": v(78.81, -60.45) * mm});
            skArc(sketch, "E16.124.2", {"start": v(78.87, -61.79) * mm, "mid": v(78.59, -61.15) * mm, "end": v(78.8, -60.48) * mm});
            skLineSegment(sketch, "E16.124.3", {"start": v(79.07, -62) * mm, "end": v(78.87, -61.79) * mm});
            skLineSegment(sketch, "E16.124.4", {"start": v(80.35, -60.33) * mm, "end": v(80.1, -60.2) * mm});
            skArc(sketch, "E16.125.0", {"start": v(82.02, -57.54) * mm, "mid": v(81.33, -57.45) * mm, "end": v(80.75, -57.84) * mm});
            skArc(sketch, "E16.125.1", {"start": v(80.73, -57.87) * mm, "mid": v(80.74, -57.86) * mm, "end": v(80.75, -57.84) * mm});
            skArc(sketch, "E16.125.2", {"start": v(80.85, -59.17) * mm, "mid": v(80.55, -58.54) * mm, "end": v(80.73, -57.87) * mm});
            skLineSegment(sketch, "E16.125.3", {"start": v(81.06, -59.38) * mm, "end": v(80.85, -59.17) * mm});
            skLineSegment(sketch, "E16.125.4", {"start": v(82.28, -57.67) * mm, "end": v(82.02, -57.54) * mm});
            skArc(sketch, "E16.126.0", {"start": v(83.86, -54.82) * mm, "mid": v(83.16, -54.76) * mm, "end": v(82.6, -55.17) * mm});
            skArc(sketch, "E16.126.1", {"start": v(82.58, -55.2) * mm, "mid": v(82.59, -55.18) * mm, "end": v(82.6, -55.17) * mm});
            skArc(sketch, "E16.126.2", {"start": v(82.74, -56.5) * mm, "mid": v(82.42, -55.88) * mm, "end": v(82.58, -55.2) * mm});
            skLineSegment(sketch, "E16.126.3", {"start": v(82.96, -56.7) * mm, "end": v(82.74, -56.5) * mm});
            skLineSegment(sketch, "E16.126.4", {"start": v(84.12, -54.95) * mm, "end": v(83.86, -54.82) * mm});
            skArc(sketch, "E16.127.0", {"start": v(85.6, -52.05) * mm, "mid": v(84.9, -52.01) * mm, "end": v(84.36, -52.44) * mm});
            skArc(sketch, "E16.127.1", {"start": v(84.34, -52.46) * mm, "mid": v(84.35, -52.45) * mm, "end": v(84.36, -52.44) * mm});
            skArc(sketch, "E16.127.2", {"start": v(84.55, -53.76) * mm, "mid": v(84.2, -53.15) * mm, "end": v(84.34, -52.46) * mm});
            skLineSegment(sketch, "E16.127.3", {"start": v(84.77, -53.95) * mm, "end": v(84.55, -53.76) * mm});
            skLineSegment(sketch, "E16.127.4", {"start": v(85.88, -52.17) * mm, "end": v(85.6, -52.05) * mm});
            skArc(sketch, "E16.128.0", {"start": v(87.27, -49.22) * mm, "mid": v(86.57, -49.2) * mm, "end": v(86.03, -49.65) * mm});
            skArc(sketch, "E16.128.1", {"start": v(86.01, -49.68) * mm, "mid": v(86.02, -49.66) * mm, "end": v(86.03, -49.65) * mm});
            skArc(sketch, "E16.128.2", {"start": v(86.26, -50.96) * mm, "mid": v(85.9, -50.37) * mm, "end": v(86.01, -49.68) * mm});
            skLineSegment(sketch, "E16.128.3", {"start": v(86.49, -51.14) * mm, "end": v(86.26, -50.96) * mm});
            skLineSegment(sketch, "E16.128.4", {"start": v(87.54, -49.33) * mm, "end": v(87.27, -49.22) * mm});
            skArc(sketch, "E16.129.0", {"start": v(88.83, -46.34) * mm, "mid": v(88.13, -46.35) * mm, "end": v(87.6, -46.8) * mm});
            skArc(sketch, "E16.129.1", {"start": v(87.6, -46.84) * mm, "mid": v(87.6, -46.82) * mm, "end": v(87.6, -46.8) * mm});
            skArc(sketch, "E16.129.2", {"start": v(87.88, -48.11) * mm, "mid": v(87.5, -47.53) * mm, "end": v(87.6, -46.84) * mm});
            skLineSegment(sketch, "E16.129.3", {"start": v(88.12, -48.29) * mm, "end": v(87.88, -48.11) * mm});
            skLineSegment(sketch, "E16.129.4", {"start": v(89.1, -46.44) * mm, "end": v(88.83, -46.34) * mm});
            skArc(sketch, "E16.130.0", {"start": v(90.3, -43.4) * mm, "mid": v(89.6, -43.44) * mm, "end": v(89.09, -43.92) * mm});
            skArc(sketch, "E16.130.1", {"start": v(89.08, -43.94) * mm, "mid": v(89.08, -43.93) * mm, "end": v(89.09, -43.92) * mm});
            skArc(sketch, "E16.130.2", {"start": v(89.4, -45.21) * mm, "mid": v(89, -44.64) * mm, "end": v(89.08, -43.94) * mm});
            skLineSegment(sketch, "E16.130.3", {"start": v(89.65, -45.38) * mm, "end": v(89.4, -45.21) * mm});
            skLineSegment(sketch, "E16.130.4", {"start": v(90.58, -43.5) * mm, "end": v(90.3, -43.4) * mm});
            skArc(sketch, "E16.131.0", {"start": v(91.67, -40.43) * mm, "mid": v(90.97, -40.48) * mm, "end": v(90.48, -40.98) * mm});
            skArc(sketch, "E16.131.1", {"start": v(90.47, -41) * mm, "mid": v(90.47, -41) * mm, "end": v(90.48, -40.98) * mm});
            skArc(sketch, "E16.131.2", {"start": v(90.84, -42.26) * mm, "mid": v(90.42, -41.7) * mm, "end": v(90.47, -41) * mm});
            skLineSegment(sketch, "E16.131.3", {"start": v(91.09, -42.42) * mm, "end": v(90.84, -42.26) * mm});
            skLineSegment(sketch, "E16.131.4", {"start": v(91.95, -40.51) * mm, "end": v(91.67, -40.43) * mm});
            skArc(sketch, "E16.132.0", {"start": v(92.94, -37.4) * mm, "mid": v(92.25, -37.48) * mm, "end": v(91.77, -38) * mm});
            skArc(sketch, "E16.132.1", {"start": v(91.76, -38.02) * mm, "mid": v(91.77, -38.01) * mm, "end": v(91.77, -38) * mm});
            skArc(sketch, "E16.132.2", {"start": v(92.17, -39.27) * mm, "mid": v(91.73, -38.72) * mm, "end": v(91.76, -38.02) * mm});
            skLineSegment(sketch, "E16.132.3", {"start": v(92.43, -39.42) * mm, "end": v(92.17, -39.27) * mm});
            skLineSegment(sketch, "E16.132.4", {"start": v(93.23, -37.48) * mm, "end": v(92.94, -37.4) * mm});
            skArc(sketch, "E16.133.0", {"start": v(94.12, -34.35) * mm, "mid": v(93.42, -34.45) * mm, "end": v(92.97, -34.97) * mm});
            skArc(sketch, "E16.133.1", {"start": v(92.96, -35) * mm, "mid": v(92.96, -34.99) * mm, "end": v(92.97, -34.97) * mm});
            skArc(sketch, "E16.133.2", {"start": v(93.4, -36.23) * mm, "mid": v(92.95, -35.7) * mm, "end": v(92.96, -35) * mm});
            skLineSegment(sketch, "E16.133.3", {"start": v(93.67, -36.37) * mm, "end": v(93.4, -36.23) * mm});
            skLineSegment(sketch, "E16.133.4", {"start": v(94.4, -34.41) * mm, "end": v(94.12, -34.35) * mm});
            skArc(sketch, "E16.134.0", {"start": v(95.2, -31.25) * mm, "mid": v(94.5, -31.37) * mm, "end": v(94.06, -31.91) * mm});
            skArc(sketch, "E16.134.1", {"start": v(94.05, -31.94) * mm, "mid": v(94.06, -31.93) * mm, "end": v(94.06, -31.91) * mm});
            skArc(sketch, "E16.134.2", {"start": v(94.54, -33.16) * mm, "mid": v(94.07, -32.64) * mm, "end": v(94.05, -31.94) * mm});
            skLineSegment(sketch, "E16.134.3", {"start": v(94.8, -33.29) * mm, "end": v(94.54, -33.16) * mm});
            skLineSegment(sketch, "E16.134.4", {"start": v(95.48, -31.3) * mm, "end": v(95.2, -31.25) * mm});
            skArc(sketch, "E16.135.0", {"start": v(96.16, -28.12) * mm, "mid": v(95.48, -28.26) * mm, "end": v(95.05, -28.82) * mm});
            skArc(sketch, "E16.135.1", {"start": v(95.05, -28.85) * mm, "mid": v(95.05, -28.83) * mm, "end": v(95.05, -28.82) * mm});
            skArc(sketch, "E16.135.2", {"start": v(95.58, -30.04) * mm, "mid": v(95.09, -29.55) * mm, "end": v(95.05, -28.85) * mm});
            skLineSegment(sketch, "E16.135.3", {"start": v(95.84, -30.17) * mm, "end": v(95.58, -30.04) * mm});
            skLineSegment(sketch, "E16.135.4", {"start": v(96.45, -28.16) * mm, "end": v(96.16, -28.12) * mm});
            skArc(sketch, "E16.136.0", {"start": v(97.03, -24.96) * mm, "mid": v(96.35, -25.12) * mm, "end": v(95.95, -25.7) * mm});
            skArc(sketch, "E16.136.1", {"start": v(95.94, -25.72) * mm, "mid": v(95.94, -25.7) * mm, "end": v(95.95, -25.7) * mm});
            skArc(sketch, "E16.136.2", {"start": v(96.51, -26.9) * mm, "mid": v(96, -26.42) * mm, "end": v(95.94, -25.72) * mm});
            skLineSegment(sketch, "E16.136.3", {"start": v(96.78, -27.02) * mm, "end": v(96.51, -26.9) * mm});
            skLineSegment(sketch, "E16.136.4", {"start": v(97.32, -25) * mm, "end": v(97.03, -24.96) * mm});
            skArc(sketch, "E16.137.0", {"start": v(97.8, -21.77) * mm, "mid": v(97.12, -21.96) * mm, "end": v(96.74, -22.54) * mm});
            skArc(sketch, "E16.137.1", {"start": v(96.73, -22.57) * mm, "mid": v(96.73, -22.55) * mm, "end": v(96.74, -22.54) * mm});
            skArc(sketch, "E16.137.2", {"start": v(97.34, -23.73) * mm, "mid": v(96.82, -23.26) * mm, "end": v(96.73, -22.57) * mm});
            skLineSegment(sketch, "E16.137.3", {"start": v(97.61, -23.84) * mm, "end": v(97.34, -23.73) * mm});
            skLineSegment(sketch, "E16.137.4", {"start": v(98.09, -21.8) * mm, "end": v(97.8, -21.77) * mm});
            skArc(sketch, "E16.138.0", {"start": v(98.46, -18.56) * mm, "mid": v(97.79, -18.77) * mm, "end": v(97.42, -19.36) * mm});
            skArc(sketch, "E16.138.1", {"start": v(97.42, -19.4) * mm, "mid": v(97.42, -19.38) * mm, "end": v(97.42, -19.36) * mm});
            skArc(sketch, "E16.138.2", {"start": v(98.06, -20.53) * mm, "mid": v(97.53, -20.08) * mm, "end": v(97.42, -19.4) * mm});
            skLineSegment(sketch, "E16.138.3", {"start": v(98.34, -20.63) * mm, "end": v(98.06, -20.53) * mm});
            skLineSegment(sketch, "E16.138.4", {"start": v(98.75, -18.57) * mm, "end": v(98.46, -18.56) * mm});
            skArc(sketch, "E16.139.0", {"start": v(99.01, -15.33) * mm, "mid": v(98.35, -15.56) * mm, "end": v(98, -16.17) * mm});
            skArc(sketch, "E16.139.1", {"start": v(98, -16.2) * mm, "mid": v(98, -16.18) * mm, "end": v(98, -16.17) * mm});
            skArc(sketch, "E16.139.2", {"start": v(98.68, -17.31) * mm, "mid": v(98.13, -16.88) * mm, "end": v(98, -16.2) * mm});
            skLineSegment(sketch, "E16.139.3", {"start": v(98.96, -17.4) * mm, "end": v(98.68, -17.31) * mm});
            skLineSegment(sketch, "E16.139.4", {"start": v(99.3, -15.33) * mm, "end": v(99.01, -15.33) * mm});
            skArc(sketch, "E16.140.0", {"start": v(99.46, -12.08) * mm, "mid": v(98.8, -12.33) * mm, "end": v(98.48, -12.95) * mm});
            skArc(sketch, "E16.140.1", {"start": v(98.48, -12.98) * mm, "mid": v(98.48, -12.96) * mm, "end": v(98.48, -12.95) * mm});
            skArc(sketch, "E16.140.2", {"start": v(99.2, -14.07) * mm, "mid": v(98.63, -13.66) * mm, "end": v(98.48, -12.98) * mm});
            skLineSegment(sketch, "E16.140.3", {"start": v(99.48, -14.15) * mm, "end": v(99.2, -14.07) * mm});
            skLineSegment(sketch, "E16.140.4", {"start": v(99.75, -12.08) * mm, "end": v(99.46, -12.08) * mm});
            skArc(sketch, "E16.141.0", {"start": v(99.8, -8.82) * mm, "mid": v(99.16, -9.1) * mm, "end": v(98.85, -9.72) * mm});
            skArc(sketch, "E16.141.1", {"start": v(98.85, -9.75) * mm, "mid": v(98.85, -9.74) * mm, "end": v(98.85, -9.72) * mm});
            skArc(sketch, "E16.141.2", {"start": v(99.6, -10.82) * mm, "mid": v(99.03, -10.43) * mm, "end": v(98.85, -9.75) * mm});
            skLineSegment(sketch, "E16.141.3", {"start": v(99.89, -10.9) * mm, "end": v(99.6, -10.82) * mm});
            skLineSegment(sketch, "E16.141.4", {"start": v(100.1, -8.8) * mm, "end": v(99.8, -8.82) * mm});
            skArc(sketch, "E16.142.0", {"start": v(100.04, -5.55) * mm, "mid": v(99.4, -5.84) * mm, "end": v(99.12, -6.48) * mm});
            skArc(sketch, "E16.142.1", {"start": v(99.11, -6.51) * mm, "mid": v(99.11, -6.5) * mm, "end": v(99.12, -6.48) * mm});
            skArc(sketch, "E16.142.2", {"start": v(99.9, -7.56) * mm, "mid": v(99.31, -7.18) * mm, "end": v(99.11, -6.51) * mm});
            skLineSegment(sketch, "E16.142.3", {"start": v(100.2, -7.62) * mm, "end": v(99.9, -7.56) * mm});
            skLineSegment(sketch, "E16.142.4", {"start": v(100.33, -5.53) * mm, "end": v(100.04, -5.55) * mm});
            skArc(sketch, "E16.143.0", {"start": v(100.16, -2.27) * mm, "mid": v(99.54, -2.59) * mm, "end": v(99.27, -3.24) * mm});
            skArc(sketch, "E16.143.1", {"start": v(99.27, -3.26) * mm, "mid": v(99.27, -3.25) * mm, "end": v(99.27, -3.24) * mm});
            skArc(sketch, "E16.143.2", {"start": v(100.1, -4.28) * mm, "mid": v(99.5, -3.93) * mm, "end": v(99.27, -3.26) * mm});
            skLineSegment(sketch, "E16.143.3", {"start": v(100.39, -4.33) * mm, "end": v(100.1, -4.28) * mm});
            skLineSegment(sketch, "E16.143.4", {"start": v(100.46, -2.24) * mm, "end": v(100.16, -2.27) * mm});
            skArc(sketch, "E16.144.0", {"start": v(100.18, 1) * mm, "mid": v(99.57, 0.67) * mm, "end": v(99.33, 0.01) * mm});
            skArc(sketch, "E16.144.1", {"start": v(99.33, -0.01) * mm, "mid": v(99.33, 0) * mm, "end": v(99.33, 0.01) * mm});
            skArc(sketch, "E16.144.2", {"start": v(100.18, -1) * mm, "mid": v(99.57, -0.67) * mm, "end": v(99.33, -0.01) * mm});
            skLineSegment(sketch, "E16.144.3", {"start": v(100.47, -1.05) * mm, "end": v(100.18, -1) * mm});
            skLineSegment(sketch, "E16.144.4", {"start": v(100.47, 1.05) * mm, "end": v(100.18, 1) * mm});
            skArc(sketch, "E16.145.0", {"start": v(100.1, 4.28) * mm, "mid": v(99.5, 3.93) * mm, "end": v(99.27, 3.26) * mm});
            skArc(sketch, "E16.145.1", {"start": v(99.27, 3.24) * mm, "mid": v(99.27, 3.25) * mm, "end": v(99.27, 3.26) * mm});
            skArc(sketch, "E16.145.2", {"start": v(100.16, 2.27) * mm, "mid": v(99.54, 2.59) * mm, "end": v(99.27, 3.24) * mm});
            skLineSegment(sketch, "E16.145.3", {"start": v(100.46, 2.24) * mm, "end": v(100.16, 2.27) * mm});
            skLineSegment(sketch, "E16.145.4", {"start": v(100.39, 4.33) * mm, "end": v(100.1, 4.28) * mm});
            skArc(sketch, "E16.146.0", {"start": v(99.9, 7.56) * mm, "mid": v(99.31, 7.18) * mm, "end": v(99.11, 6.51) * mm});
            skArc(sketch, "E16.146.1", {"start": v(99.12, 6.48) * mm, "mid": v(99.11, 6.5) * mm, "end": v(99.11, 6.51) * mm});
            skArc(sketch, "E16.146.2", {"start": v(100.04, 5.55) * mm, "mid": v(99.4, 5.84) * mm, "end": v(99.12, 6.48) * mm});
            skLineSegment(sketch, "E16.146.3", {"start": v(100.33, 5.53) * mm, "end": v(100.04, 5.55) * mm});
            skLineSegment(sketch, "E16.146.4", {"start": v(100.2, 7.62) * mm, "end": v(99.9, 7.56) * mm});
            skArc(sketch, "E16.147.0", {"start": v(99.6, 10.82) * mm, "mid": v(99.03, 10.43) * mm, "end": v(98.85, 9.75) * mm});
            skArc(sketch, "E16.147.1", {"start": v(98.85, 9.72) * mm, "mid": v(98.85, 9.74) * mm, "end": v(98.85, 9.75) * mm});
            skArc(sketch, "E16.147.2", {"start": v(99.8, 8.82) * mm, "mid": v(99.16, 9.1) * mm, "end": v(98.85, 9.72) * mm});
            skLineSegment(sketch, "E16.147.3", {"start": v(100.1, 8.8) * mm, "end": v(99.8, 8.82) * mm});
            skLineSegment(sketch, "E16.147.4", {"start": v(99.89, 10.9) * mm, "end": v(99.6, 10.82) * mm});
            skArc(sketch, "E16.148.0", {"start": v(99.2, 14.07) * mm, "mid": v(98.63, 13.66) * mm, "end": v(98.48, 12.98) * mm});
            skArc(sketch, "E16.148.1", {"start": v(98.48, 12.95) * mm, "mid": v(98.48, 12.96) * mm, "end": v(98.48, 12.98) * mm});
            skArc(sketch, "E16.148.2", {"start": v(99.46, 12.08) * mm, "mid": v(98.8, 12.33) * mm, "end": v(98.48, 12.95) * mm});
            skLineSegment(sketch, "E16.148.3", {"start": v(99.75, 12.08) * mm, "end": v(99.46, 12.08) * mm});
            skLineSegment(sketch, "E16.148.4", {"start": v(99.48, 14.15) * mm, "end": v(99.2, 14.07) * mm});
            skArc(sketch, "E16.149.0", {"start": v(98.68, 17.31) * mm, "mid": v(98.13, 16.88) * mm, "end": v(98, 16.2) * mm});
            skArc(sketch, "E16.149.1", {"start": v(98, 16.17) * mm, "mid": v(98, 16.18) * mm, "end": v(98, 16.2) * mm});
            skArc(sketch, "E16.149.2", {"start": v(99.01, 15.33) * mm, "mid": v(98.35, 15.56) * mm, "end": v(98, 16.17) * mm});
            skLineSegment(sketch, "E16.149.3", {"start": v(99.3, 15.33) * mm, "end": v(99.01, 15.33) * mm});
            skLineSegment(sketch, "E16.149.4", {"start": v(98.96, 17.4) * mm, "end": v(98.68, 17.31) * mm});
            skArc(sketch, "E16.150.0", {"start": v(98.06, 20.53) * mm, "mid": v(97.53, 20.08) * mm, "end": v(97.42, 19.4) * mm});
            skArc(sketch, "E16.150.1", {"start": v(97.42, 19.36) * mm, "mid": v(97.42, 19.38) * mm, "end": v(97.42, 19.4) * mm});
            skArc(sketch, "E16.150.2", {"start": v(98.46, 18.56) * mm, "mid": v(97.79, 18.77) * mm, "end": v(97.42, 19.36) * mm});
            skLineSegment(sketch, "E16.150.3", {"start": v(98.75, 18.57) * mm, "end": v(98.46, 18.56) * mm});
            skLineSegment(sketch, "E16.150.4", {"start": v(98.34, 20.63) * mm, "end": v(98.06, 20.53) * mm});
            skArc(sketch, "E16.151.0", {"start": v(97.34, 23.73) * mm, "mid": v(96.82, 23.26) * mm, "end": v(96.73, 22.57) * mm});
            skArc(sketch, "E16.151.1", {"start": v(96.74, 22.54) * mm, "mid": v(96.73, 22.55) * mm, "end": v(96.73, 22.57) * mm});
            skArc(sketch, "E16.151.2", {"start": v(97.8, 21.77) * mm, "mid": v(97.12, 21.96) * mm, "end": v(96.74, 22.54) * mm});
            skLineSegment(sketch, "E16.151.3", {"start": v(98.09, 21.8) * mm, "end": v(97.8, 21.77) * mm});
            skLineSegment(sketch, "E16.151.4", {"start": v(97.61, 23.84) * mm, "end": v(97.34, 23.73) * mm});
            skArc(sketch, "E16.152.0", {"start": v(96.51, 26.9) * mm, "mid": v(96, 26.42) * mm, "end": v(95.94, 25.72) * mm});
            skArc(sketch, "E16.152.1", {"start": v(95.95, 25.7) * mm, "mid": v(95.94, 25.7) * mm, "end": v(95.94, 25.72) * mm});
            skArc(sketch, "E16.152.2", {"start": v(97.03, 24.96) * mm, "mid": v(96.35, 25.12) * mm, "end": v(95.95, 25.7) * mm});
            skLineSegment(sketch, "E16.152.3", {"start": v(97.32, 25) * mm, "end": v(97.03, 24.96) * mm});
            skLineSegment(sketch, "E16.152.4", {"start": v(96.78, 27.02) * mm, "end": v(96.51, 26.9) * mm});
            skArc(sketch, "E16.153.0", {"start": v(95.58, 30.04) * mm, "mid": v(95.09, 29.55) * mm, "end": v(95.05, 28.85) * mm});
            skArc(sketch, "E16.153.1", {"start": v(95.05, 28.82) * mm, "mid": v(95.05, 28.83) * mm, "end": v(95.05, 28.85) * mm});
            skArc(sketch, "E16.153.2", {"start": v(96.16, 28.12) * mm, "mid": v(95.48, 28.26) * mm, "end": v(95.05, 28.82) * mm});
            skLineSegment(sketch, "E16.153.3", {"start": v(96.45, 28.16) * mm, "end": v(96.16, 28.12) * mm});
            skLineSegment(sketch, "E16.153.4", {"start": v(95.84, 30.17) * mm, "end": v(95.58, 30.04) * mm});
            skArc(sketch, "E16.154.0", {"start": v(94.54, 33.16) * mm, "mid": v(94.07, 32.64) * mm, "end": v(94.05, 31.94) * mm});
            skArc(sketch, "E16.154.1", {"start": v(94.06, 31.91) * mm, "mid": v(94.06, 31.93) * mm, "end": v(94.05, 31.94) * mm});
            skArc(sketch, "E16.154.2", {"start": v(95.2, 31.25) * mm, "mid": v(94.5, 31.37) * mm, "end": v(94.06, 31.91) * mm});
            skLineSegment(sketch, "E16.154.3", {"start": v(95.48, 31.3) * mm, "end": v(95.2, 31.25) * mm});
            skLineSegment(sketch, "E16.154.4", {"start": v(94.8, 33.29) * mm, "end": v(94.54, 33.16) * mm});
            skArc(sketch, "E16.155.0", {"start": v(93.4, 36.23) * mm, "mid": v(92.95, 35.7) * mm, "end": v(92.96, 35) * mm});
            skArc(sketch, "E16.155.1", {"start": v(92.97, 34.97) * mm, "mid": v(92.96, 34.99) * mm, "end": v(92.96, 35) * mm});
            skArc(sketch, "E16.155.2", {"start": v(94.12, 34.35) * mm, "mid": v(93.42, 34.45) * mm, "end": v(92.97, 34.97) * mm});
            skLineSegment(sketch, "E16.155.3", {"start": v(94.4, 34.41) * mm, "end": v(94.12, 34.35) * mm});
            skLineSegment(sketch, "E16.155.4", {"start": v(93.67, 36.37) * mm, "end": v(93.4, 36.23) * mm});
            skArc(sketch, "E16.156.0", {"start": v(92.17, 39.27) * mm, "mid": v(91.73, 38.72) * mm, "end": v(91.76, 38.02) * mm});
            skArc(sketch, "E16.156.1", {"start": v(91.77, 38) * mm, "mid": v(91.77, 38.01) * mm, "end": v(91.76, 38.02) * mm});
            skArc(sketch, "E16.156.2", {"start": v(92.94, 37.4) * mm, "mid": v(92.25, 37.48) * mm, "end": v(91.77, 38) * mm});
            skLineSegment(sketch, "E16.156.3", {"start": v(93.23, 37.48) * mm, "end": v(92.94, 37.4) * mm});
            skLineSegment(sketch, "E16.156.4", {"start": v(92.43, 39.42) * mm, "end": v(92.17, 39.27) * mm});
            skArc(sketch, "E16.157.0", {"start": v(90.84, 42.26) * mm, "mid": v(90.42, 41.7) * mm, "end": v(90.47, 41) * mm});
            skArc(sketch, "E16.157.1", {"start": v(90.48, 40.98) * mm, "mid": v(90.47, 41) * mm, "end": v(90.47, 41) * mm});
            skArc(sketch, "E16.157.2", {"start": v(91.67, 40.43) * mm, "mid": v(90.97, 40.48) * mm, "end": v(90.48, 40.98) * mm});
            skLineSegment(sketch, "E16.157.3", {"start": v(91.95, 40.51) * mm, "end": v(91.67, 40.43) * mm});
            skLineSegment(sketch, "E16.157.4", {"start": v(91.09, 42.42) * mm, "end": v(90.84, 42.26) * mm});
            skArc(sketch, "E16.158.0", {"start": v(89.4, 45.21) * mm, "mid": v(89, 44.64) * mm, "end": v(89.08, 43.94) * mm});
            skArc(sketch, "E16.158.1", {"start": v(89.09, 43.92) * mm, "mid": v(89.08, 43.93) * mm, "end": v(89.08, 43.94) * mm});
            skArc(sketch, "E16.158.2", {"start": v(90.3, 43.4) * mm, "mid": v(89.6, 43.44) * mm, "end": v(89.09, 43.92) * mm});
            skLineSegment(sketch, "E16.158.3", {"start": v(90.58, 43.5) * mm, "end": v(90.3, 43.4) * mm});
            skLineSegment(sketch, "E16.158.4", {"start": v(89.65, 45.38) * mm, "end": v(89.4, 45.21) * mm});
            skArc(sketch, "E16.159.0", {"start": v(87.88, 48.11) * mm, "mid": v(87.5, 47.53) * mm, "end": v(87.6, 46.84) * mm});
            skArc(sketch, "E16.159.1", {"start": v(87.6, 46.8) * mm, "mid": v(87.6, 46.82) * mm, "end": v(87.6, 46.84) * mm});
            skArc(sketch, "E16.159.2", {"start": v(88.83, 46.34) * mm, "mid": v(88.13, 46.35) * mm, "end": v(87.6, 46.8) * mm});
            skLineSegment(sketch, "E16.159.3", {"start": v(89.1, 46.44) * mm, "end": v(88.83, 46.34) * mm});
            skLineSegment(sketch, "E16.159.4", {"start": v(88.12, 48.29) * mm, "end": v(87.88, 48.11) * mm});
            skArc(sketch, "E16.160.0", {"start": v(86.26, 50.96) * mm, "mid": v(85.9, 50.37) * mm, "end": v(86.01, 49.68) * mm});
            skArc(sketch, "E16.160.1", {"start": v(86.03, 49.65) * mm, "mid": v(86.02, 49.66) * mm, "end": v(86.01, 49.68) * mm});
            skArc(sketch, "E16.160.2", {"start": v(87.27, 49.22) * mm, "mid": v(86.57, 49.2) * mm, "end": v(86.03, 49.65) * mm});
            skLineSegment(sketch, "E16.160.3", {"start": v(87.54, 49.33) * mm, "end": v(87.27, 49.22) * mm});
            skLineSegment(sketch, "E16.160.4", {"start": v(86.49, 51.14) * mm, "end": v(86.26, 50.96) * mm});
            skArc(sketch, "E16.161.0", {"start": v(84.55, 53.76) * mm, "mid": v(84.2, 53.15) * mm, "end": v(84.34, 52.46) * mm});
            skArc(sketch, "E16.161.1", {"start": v(84.36, 52.44) * mm, "mid": v(84.35, 52.45) * mm, "end": v(84.34, 52.46) * mm});
            skArc(sketch, "E16.161.2", {"start": v(85.6, 52.05) * mm, "mid": v(84.9, 52.01) * mm, "end": v(84.36, 52.44) * mm});
            skLineSegment(sketch, "E16.161.3", {"start": v(85.88, 52.17) * mm, "end": v(85.6, 52.05) * mm});
            skLineSegment(sketch, "E16.161.4", {"start": v(84.77, 53.95) * mm, "end": v(84.55, 53.76) * mm});
            skArc(sketch, "E16.162.0", {"start": v(82.74, 56.5) * mm, "mid": v(82.42, 55.88) * mm, "end": v(82.58, 55.2) * mm});
            skArc(sketch, "E16.162.1", {"start": v(82.6, 55.17) * mm, "mid": v(82.59, 55.18) * mm, "end": v(82.58, 55.2) * mm});
            skArc(sketch, "E16.162.2", {"start": v(83.86, 54.82) * mm, "mid": v(83.16, 54.76) * mm, "end": v(82.6, 55.17) * mm});
            skLineSegment(sketch, "E16.162.3", {"start": v(84.12, 54.95) * mm, "end": v(83.86, 54.82) * mm});
            skLineSegment(sketch, "E16.162.4", {"start": v(82.96, 56.7) * mm, "end": v(82.74, 56.5) * mm});
            skArc(sketch, "E16.163.0", {"start": v(80.85, 59.17) * mm, "mid": v(80.55, 58.54) * mm, "end": v(80.73, 57.87) * mm});
            skArc(sketch, "E16.163.1", {"start": v(80.75, 57.84) * mm, "mid": v(80.74, 57.86) * mm, "end": v(80.73, 57.87) * mm});
            skArc(sketch, "E16.163.2", {"start": v(82.02, 57.54) * mm, "mid": v(81.33, 57.45) * mm, "end": v(80.75, 57.84) * mm});
            skLineSegment(sketch, "E16.163.3", {"start": v(82.28, 57.67) * mm, "end": v(82.02, 57.54) * mm});
            skLineSegment(sketch, "E16.163.4", {"start": v(81.06, 59.38) * mm, "end": v(80.85, 59.17) * mm});
            skArc(sketch, "E16.164.0", {"start": v(78.87, 61.79) * mm, "mid": v(78.59, 61.15) * mm, "end": v(78.8, 60.48) * mm});
            skArc(sketch, "E16.164.1", {"start": v(78.81, 60.45) * mm, "mid": v(78.8, 60.47) * mm, "end": v(78.8, 60.48) * mm});
            skArc(sketch, "E16.164.2", {"start": v(80.1, 60.2) * mm, "mid": v(79.4, 60.08) * mm, "end": v(78.81, 60.45) * mm});
            skLineSegment(sketch, "E16.164.3", {"start": v(80.35, 60.33) * mm, "end": v(80.1, 60.2) * mm});
            skLineSegment(sketch, "E16.164.4", {"start": v(79.07, 62) * mm, "end": v(78.87, 61.79) * mm});
            skArc(sketch, "E16.165.0", {"start": v(76.8, 64.33) * mm, "mid": v(76.54, 63.69) * mm, "end": v(76.77, 63.02) * mm});
            skArc(sketch, "E16.165.1", {"start": v(76.79, 63) * mm, "mid": v(76.78, 63.01) * mm, "end": v(76.77, 63.02) * mm});
            skArc(sketch, "E16.165.2", {"start": v(78.08, 62.78) * mm, "mid": v(77.4, 62.65) * mm, "end": v(76.79, 63) * mm});
            skLineSegment(sketch, "E16.165.3", {"start": v(78.33, 62.93) * mm, "end": v(78.08, 62.78) * mm});
            skLineSegment(sketch, "E16.165.4", {"start": v(77, 64.55) * mm, "end": v(76.8, 64.33) * mm});
            skArc(sketch, "E16.166.0", {"start": v(74.66, 66.81) * mm, "mid": v(74.42, 66.16) * mm, "end": v(74.67, 65.5) * mm});
            skArc(sketch, "E16.166.1", {"start": v(74.69, 65.48) * mm, "mid": v(74.68, 65.5) * mm, "end": v(74.67, 65.5) * mm});
            skArc(sketch, "E16.166.2", {"start": v(75.99, 65.3) * mm, "mid": v(75.3, 65.15) * mm, "end": v(74.69, 65.48) * mm});
            skLineSegment(sketch, "E16.166.3", {"start": v(76.23, 65.46) * mm, "end": v(75.99, 65.3) * mm});
            skLineSegment(sketch, "E16.166.4", {"start": v(74.85, 67.04) * mm, "end": v(74.66, 66.81) * mm});
            skArc(sketch, "E16.167.0", {"start": v(72.43, 69.22) * mm, "mid": v(72.21, 68.55) * mm, "end": v(72.49, 67.9) * mm});
            skArc(sketch, "E16.167.1", {"start": v(72.5, 67.89) * mm, "mid": v(72.5, 67.9) * mm, "end": v(72.49, 67.9) * mm});
            skArc(sketch, "E16.167.2", {"start": v(73.8, 67.75) * mm, "mid": v(73.13, 67.58) * mm, "end": v(72.5, 67.89) * mm});
            skLineSegment(sketch, "E16.167.3", {"start": v(74.05, 67.92) * mm, "end": v(73.8, 67.75) * mm});
            skLineSegment(sketch, "E16.167.4", {"start": v(72.62, 69.45) * mm, "end": v(72.43, 69.22) * mm});
            skArc(sketch, "E16.168.0", {"start": v(70.13, 71.55) * mm, "mid": v(69.93, 70.88) * mm, "end": v(70.22, 70.24) * mm});
            skArc(sketch, "E16.168.1", {"start": v(70.24, 70.22) * mm, "mid": v(70.23, 70.23) * mm, "end": v(70.22, 70.24) * mm});
            skArc(sketch, "E16.168.2", {"start": v(71.55, 70.13) * mm, "mid": v(70.88, 69.93) * mm, "end": v(70.24, 70.22) * mm});
            skLineSegment(sketch, "E16.168.3", {"start": v(71.79, 70.3) * mm, "end": v(71.55, 70.13) * mm});
            skLineSegment(sketch, "E16.168.4", {"start": v(70.3, 71.79) * mm, "end": v(70.13, 71.55) * mm});
            skArc(sketch, "E16.169.0", {"start": v(67.75, 73.8) * mm, "mid": v(67.58, 73.13) * mm, "end": v(67.89, 72.5) * mm});
            skArc(sketch, "E16.169.1", {"start": v(67.9, 72.49) * mm, "mid": v(67.9, 72.5) * mm, "end": v(67.89, 72.5) * mm});
            skArc(sketch, "E16.169.2", {"start": v(69.22, 72.43) * mm, "mid": v(68.55, 72.21) * mm, "end": v(67.9, 72.49) * mm});
            skLineSegment(sketch, "E16.169.3", {"start": v(69.45, 72.62) * mm, "end": v(69.22, 72.43) * mm});
            skLineSegment(sketch, "E16.169.4", {"start": v(67.92, 74.05) * mm, "end": v(67.75, 73.8) * mm});
            skArc(sketch, "E16.170.0", {"start": v(65.3, 75.99) * mm, "mid": v(65.15, 75.3) * mm, "end": v(65.48, 74.69) * mm});
            skArc(sketch, "E16.170.1", {"start": v(65.5, 74.67) * mm, "mid": v(65.5, 74.68) * mm, "end": v(65.48, 74.69) * mm});
            skArc(sketch, "E16.170.2", {"start": v(66.81, 74.66) * mm, "mid": v(66.16, 74.42) * mm, "end": v(65.5, 74.67) * mm});
            skLineSegment(sketch, "E16.170.3", {"start": v(67.04, 74.85) * mm, "end": v(66.81, 74.66) * mm});
            skLineSegment(sketch, "E16.170.4", {"start": v(65.46, 76.23) * mm, "end": v(65.3, 75.99) * mm});
            skArc(sketch, "E16.171.0", {"start": v(62.78, 78.08) * mm, "mid": v(62.65, 77.4) * mm, "end": v(63, 76.79) * mm});
            skArc(sketch, "E16.171.1", {"start": v(63.02, 76.77) * mm, "mid": v(63.01, 76.78) * mm, "end": v(63, 76.79) * mm});
            skArc(sketch, "E16.171.2", {"start": v(64.33, 76.8) * mm, "mid": v(63.69, 76.54) * mm, "end": v(63.02, 76.77) * mm});
            skLineSegment(sketch, "E16.171.3", {"start": v(64.55, 77) * mm, "end": v(64.33, 76.8) * mm});
            skLineSegment(sketch, "E16.171.4", {"start": v(62.93, 78.33) * mm, "end": v(62.78, 78.08) * mm});
            skArc(sketch, "E16.172.0", {"start": v(60.2, 80.1) * mm, "mid": v(60.08, 79.4) * mm, "end": v(60.45, 78.81) * mm});
            skArc(sketch, "E16.172.1", {"start": v(60.48, 78.8) * mm, "mid": v(60.47, 78.8) * mm, "end": v(60.45, 78.81) * mm});
            skArc(sketch, "E16.172.2", {"start": v(61.79, 78.87) * mm, "mid": v(61.15, 78.59) * mm, "end": v(60.48, 78.8) * mm});
            skLineSegment(sketch, "E16.172.3", {"start": v(62, 79.07) * mm, "end": v(61.79, 78.87) * mm});
            skLineSegment(sketch, "E16.172.4", {"start": v(60.33, 80.35) * mm, "end": v(60.2, 80.1) * mm});
            skArc(sketch, "E16.173.0", {"start": v(57.54, 82.02) * mm, "mid": v(57.45, 81.33) * mm, "end": v(57.84, 80.75) * mm});
            skArc(sketch, "E16.173.1", {"start": v(57.87, 80.73) * mm, "mid": v(57.86, 80.74) * mm, "end": v(57.84, 80.75) * mm});
            skArc(sketch, "E16.173.2", {"start": v(59.17, 80.85) * mm, "mid": v(58.54, 80.55) * mm, "end": v(57.87, 80.73) * mm});
            skLineSegment(sketch, "E16.173.3", {"start": v(59.38, 81.06) * mm, "end": v(59.17, 80.85) * mm});
            skLineSegment(sketch, "E16.173.4", {"start": v(57.67, 82.28) * mm, "end": v(57.54, 82.02) * mm});
            skArc(sketch, "E16.174.0", {"start": v(54.82, 83.86) * mm, "mid": v(54.76, 83.16) * mm, "end": v(55.17, 82.6) * mm});
            skArc(sketch, "E16.174.1", {"start": v(55.2, 82.58) * mm, "mid": v(55.18, 82.59) * mm, "end": v(55.17, 82.6) * mm});
            skArc(sketch, "E16.174.2", {"start": v(56.5, 82.74) * mm, "mid": v(55.88, 82.42) * mm, "end": v(55.2, 82.58) * mm});
            skLineSegment(sketch, "E16.174.3", {"start": v(56.7, 82.96) * mm, "end": v(56.5, 82.74) * mm});
            skLineSegment(sketch, "E16.174.4", {"start": v(54.95, 84.12) * mm, "end": v(54.82, 83.86) * mm});
            skArc(sketch, "E16.175.0", {"start": v(52.05, 85.6) * mm, "mid": v(52.01, 84.9) * mm, "end": v(52.44, 84.36) * mm});
            skArc(sketch, "E16.175.1", {"start": v(52.46, 84.34) * mm, "mid": v(52.45, 84.35) * mm, "end": v(52.44, 84.36) * mm});
            skArc(sketch, "E16.175.2", {"start": v(53.76, 84.55) * mm, "mid": v(53.15, 84.2) * mm, "end": v(52.46, 84.34) * mm});
            skLineSegment(sketch, "E16.175.3", {"start": v(53.95, 84.77) * mm, "end": v(53.76, 84.55) * mm});
            skLineSegment(sketch, "E16.175.4", {"start": v(52.17, 85.88) * mm, "end": v(52.05, 85.6) * mm});
            skArc(sketch, "E16.176.0", {"start": v(49.22, 87.27) * mm, "mid": v(49.2, 86.57) * mm, "end": v(49.65, 86.03) * mm});
            skArc(sketch, "E16.176.1", {"start": v(49.68, 86.01) * mm, "mid": v(49.66, 86.02) * mm, "end": v(49.65, 86.03) * mm});
            skArc(sketch, "E16.176.2", {"start": v(50.96, 86.26) * mm, "mid": v(50.37, 85.9) * mm, "end": v(49.68, 86.01) * mm});
            skLineSegment(sketch, "E16.176.3", {"start": v(51.14, 86.49) * mm, "end": v(50.96, 86.26) * mm});
            skLineSegment(sketch, "E16.176.4", {"start": v(49.33, 87.54) * mm, "end": v(49.22, 87.27) * mm});
            skArc(sketch, "E16.177.0", {"start": v(46.34, 88.83) * mm, "mid": v(46.35, 88.13) * mm, "end": v(46.8, 87.6) * mm});
            skArc(sketch, "E16.177.1", {"start": v(46.84, 87.6) * mm, "mid": v(46.82, 87.6) * mm, "end": v(46.8, 87.6) * mm});
            skArc(sketch, "E16.177.2", {"start": v(48.11, 87.88) * mm, "mid": v(47.53, 87.5) * mm, "end": v(46.84, 87.6) * mm});
            skLineSegment(sketch, "E16.177.3", {"start": v(48.29, 88.12) * mm, "end": v(48.11, 87.88) * mm});
            skLineSegment(sketch, "E16.177.4", {"start": v(46.44, 89.1) * mm, "end": v(46.34, 88.83) * mm});
            skArc(sketch, "E16.178.0", {"start": v(43.4, 90.3) * mm, "mid": v(43.44, 89.6) * mm, "end": v(43.92, 89.09) * mm});
            skArc(sketch, "E16.178.1", {"start": v(43.94, 89.08) * mm, "mid": v(43.93, 89.08) * mm, "end": v(43.92, 89.09) * mm});
            skArc(sketch, "E16.178.2", {"start": v(45.21, 89.4) * mm, "mid": v(44.64, 89) * mm, "end": v(43.94, 89.08) * mm});
            skLineSegment(sketch, "E16.178.3", {"start": v(45.38, 89.65) * mm, "end": v(45.21, 89.4) * mm});
            skLineSegment(sketch, "E16.178.4", {"start": v(43.5, 90.58) * mm, "end": v(43.4, 90.3) * mm});
            skArc(sketch, "E16.179.0", {"start": v(40.43, 91.67) * mm, "mid": v(40.48, 90.97) * mm, "end": v(40.98, 90.48) * mm});
            skArc(sketch, "E16.179.1", {"start": v(41, 90.47) * mm, "mid": v(41, 90.47) * mm, "end": v(40.98, 90.48) * mm});
            skArc(sketch, "E16.179.2", {"start": v(42.26, 90.84) * mm, "mid": v(41.7, 90.42) * mm, "end": v(41, 90.47) * mm});
            skLineSegment(sketch, "E16.179.3", {"start": v(42.42, 91.09) * mm, "end": v(42.26, 90.84) * mm});
            skLineSegment(sketch, "E16.179.4", {"start": v(40.51, 91.95) * mm, "end": v(40.43, 91.67) * mm});
            skArc(sketch, "E16.180.0", {"start": v(37.4, 92.94) * mm, "mid": v(37.48, 92.25) * mm, "end": v(38, 91.77) * mm});
            skArc(sketch, "E16.180.1", {"start": v(38.02, 91.76) * mm, "mid": v(38.01, 91.77) * mm, "end": v(38, 91.77) * mm});
            skArc(sketch, "E16.180.2", {"start": v(39.27, 92.17) * mm, "mid": v(38.72, 91.73) * mm, "end": v(38.02, 91.76) * mm});
            skLineSegment(sketch, "E16.180.3", {"start": v(39.42, 92.43) * mm, "end": v(39.27, 92.17) * mm});
            skLineSegment(sketch, "E16.180.4", {"start": v(37.48, 93.23) * mm, "end": v(37.4, 92.94) * mm});
            skArc(sketch, "E16.181.0", {"start": v(34.35, 94.12) * mm, "mid": v(34.45, 93.42) * mm, "end": v(34.97, 92.97) * mm});
            skArc(sketch, "E16.181.1", {"start": v(35, 92.96) * mm, "mid": v(34.99, 92.96) * mm, "end": v(34.97, 92.97) * mm});
            skArc(sketch, "E16.181.2", {"start": v(36.23, 93.4) * mm, "mid": v(35.7, 92.95) * mm, "end": v(35, 92.96) * mm});
            skLineSegment(sketch, "E16.181.3", {"start": v(36.37, 93.67) * mm, "end": v(36.23, 93.4) * mm});
            skLineSegment(sketch, "E16.181.4", {"start": v(34.41, 94.4) * mm, "end": v(34.35, 94.12) * mm});
            skArc(sketch, "E16.182.0", {"start": v(31.25, 95.2) * mm, "mid": v(31.37, 94.5) * mm, "end": v(31.91, 94.06) * mm});
            skArc(sketch, "E16.182.1", {"start": v(31.94, 94.05) * mm, "mid": v(31.93, 94.06) * mm, "end": v(31.91, 94.06) * mm});
            skArc(sketch, "E16.182.2", {"start": v(33.16, 94.54) * mm, "mid": v(32.64, 94.07) * mm, "end": v(31.94, 94.05) * mm});
            skLineSegment(sketch, "E16.182.3", {"start": v(33.29, 94.8) * mm, "end": v(33.16, 94.54) * mm});
            skLineSegment(sketch, "E16.182.4", {"start": v(31.3, 95.48) * mm, "end": v(31.25, 95.2) * mm});
            skArc(sketch, "E16.183.0", {"start": v(28.12, 96.16) * mm, "mid": v(28.26, 95.48) * mm, "end": v(28.82, 95.05) * mm});
            skArc(sketch, "E16.183.1", {"start": v(28.85, 95.05) * mm, "mid": v(28.83, 95.05) * mm, "end": v(28.82, 95.05) * mm});
            skArc(sketch, "E16.183.2", {"start": v(30.04, 95.58) * mm, "mid": v(29.55, 95.09) * mm, "end": v(28.85, 95.05) * mm});
            skLineSegment(sketch, "E16.183.3", {"start": v(30.17, 95.84) * mm, "end": v(30.04, 95.58) * mm});
            skLineSegment(sketch, "E16.183.4", {"start": v(28.16, 96.45) * mm, "end": v(28.12, 96.16) * mm});
            skArc(sketch, "E16.184.0", {"start": v(24.96, 97.03) * mm, "mid": v(25.12, 96.35) * mm, "end": v(25.7, 95.95) * mm});
            skArc(sketch, "E16.184.1", {"start": v(25.72, 95.94) * mm, "mid": v(25.7, 95.94) * mm, "end": v(25.7, 95.95) * mm});
            skArc(sketch, "E16.184.2", {"start": v(26.9, 96.51) * mm, "mid": v(26.42, 96) * mm, "end": v(25.72, 95.94) * mm});
            skLineSegment(sketch, "E16.184.3", {"start": v(27.02, 96.78) * mm, "end": v(26.9, 96.51) * mm});
            skLineSegment(sketch, "E16.184.4", {"start": v(25, 97.32) * mm, "end": v(24.96, 97.03) * mm});
            skArc(sketch, "E16.185.0", {"start": v(21.77, 97.8) * mm, "mid": v(21.96, 97.12) * mm, "end": v(22.54, 96.74) * mm});
            skArc(sketch, "E16.185.1", {"start": v(22.57, 96.73) * mm, "mid": v(22.55, 96.73) * mm, "end": v(22.54, 96.74) * mm});
            skArc(sketch, "E16.185.2", {"start": v(23.73, 97.34) * mm, "mid": v(23.26, 96.82) * mm, "end": v(22.57, 96.73) * mm});
            skLineSegment(sketch, "E16.185.3", {"start": v(23.84, 97.61) * mm, "end": v(23.73, 97.34) * mm});
            skLineSegment(sketch, "E16.185.4", {"start": v(21.8, 98.09) * mm, "end": v(21.77, 97.8) * mm});
            skArc(sketch, "E16.186.0", {"start": v(18.56, 98.46) * mm, "mid": v(18.77, 97.79) * mm, "end": v(19.36, 97.42) * mm});
            skArc(sketch, "E16.186.1", {"start": v(19.4, 97.42) * mm, "mid": v(19.38, 97.42) * mm, "end": v(19.36, 97.42) * mm});
            skArc(sketch, "E16.186.2", {"start": v(20.53, 98.06) * mm, "mid": v(20.08, 97.53) * mm, "end": v(19.4, 97.42) * mm});
            skLineSegment(sketch, "E16.186.3", {"start": v(20.63, 98.34) * mm, "end": v(20.53, 98.06) * mm});
            skLineSegment(sketch, "E16.186.4", {"start": v(18.57, 98.75) * mm, "end": v(18.56, 98.46) * mm});
            skArc(sketch, "E16.187.0", {"start": v(15.33, 99.01) * mm, "mid": v(15.56, 98.35) * mm, "end": v(16.17, 98) * mm});
            skArc(sketch, "E16.187.1", {"start": v(16.2, 98) * mm, "mid": v(16.18, 98) * mm, "end": v(16.17, 98) * mm});
            skArc(sketch, "E16.187.2", {"start": v(17.31, 98.68) * mm, "mid": v(16.88, 98.13) * mm, "end": v(16.2, 98) * mm});
            skLineSegment(sketch, "E16.187.3", {"start": v(17.4, 98.96) * mm, "end": v(17.31, 98.68) * mm});
            skLineSegment(sketch, "E16.187.4", {"start": v(15.33, 99.3) * mm, "end": v(15.33, 99.01) * mm});
            skArc(sketch, "E16.188.0", {"start": v(12.08, 99.46) * mm, "mid": v(12.33, 98.8) * mm, "end": v(12.95, 98.48) * mm});
            skArc(sketch, "E16.188.1", {"start": v(12.98, 98.48) * mm, "mid": v(12.96, 98.48) * mm, "end": v(12.95, 98.48) * mm});
            skArc(sketch, "E16.188.2", {"start": v(14.07, 99.2) * mm, "mid": v(13.66, 98.63) * mm, "end": v(12.98, 98.48) * mm});
            skLineSegment(sketch, "E16.188.3", {"start": v(14.15, 99.48) * mm, "end": v(14.07, 99.2) * mm});
            skLineSegment(sketch, "E16.188.4", {"start": v(12.08, 99.75) * mm, "end": v(12.08, 99.46) * mm});
            skArc(sketch, "E16.189.0", {"start": v(8.82, 99.8) * mm, "mid": v(9.1, 99.16) * mm, "end": v(9.72, 98.85) * mm});
            skArc(sketch, "E16.189.1", {"start": v(9.75, 98.85) * mm, "mid": v(9.74, 98.85) * mm, "end": v(9.72, 98.85) * mm});
            skArc(sketch, "E16.189.2", {"start": v(10.82, 99.6) * mm, "mid": v(10.43, 99.03) * mm, "end": v(9.75, 98.85) * mm});
            skLineSegment(sketch, "E16.189.3", {"start": v(10.9, 99.89) * mm, "end": v(10.82, 99.6) * mm});
            skLineSegment(sketch, "E16.189.4", {"start": v(8.8, 100.1) * mm, "end": v(8.82, 99.8) * mm});
            skArc(sketch, "E16.190.0", {"start": v(5.55, 100.04) * mm, "mid": v(5.84, 99.4) * mm, "end": v(6.48, 99.12) * mm});
            skArc(sketch, "E16.190.1", {"start": v(6.51, 99.11) * mm, "mid": v(6.5, 99.11) * mm, "end": v(6.48, 99.12) * mm});
            skArc(sketch, "E16.190.2", {"start": v(7.56, 99.9) * mm, "mid": v(7.18, 99.31) * mm, "end": v(6.51, 99.11) * mm});
            skLineSegment(sketch, "E16.190.3", {"start": v(7.62, 100.2) * mm, "end": v(7.56, 99.9) * mm});
            skLineSegment(sketch, "E16.190.4", {"start": v(5.53, 100.33) * mm, "end": v(5.55, 100.04) * mm});
            skArc(sketch, "E16.191.0", {"start": v(2.27, 100.16) * mm, "mid": v(2.59, 99.54) * mm, "end": v(3.24, 99.27) * mm});
            skArc(sketch, "E16.191.1", {"start": v(3.26, 99.27) * mm, "mid": v(3.25, 99.27) * mm, "end": v(3.24, 99.27) * mm});
            skArc(sketch, "E16.191.2", {"start": v(4.28, 100.1) * mm, "mid": v(3.93, 99.5) * mm, "end": v(3.26, 99.27) * mm});
            skLineSegment(sketch, "E16.191.3", {"start": v(4.33, 100.39) * mm, "end": v(4.28, 100.1) * mm});
            skLineSegment(sketch, "E16.191.4", {"start": v(2.24, 100.46) * mm, "end": v(2.27, 100.16) * mm});
            skSolve(sketch);
        }
        {
            var Q0;
            Q0=makeQuery(id+"F0.imprint","IMPRINT",FACE,{"disambiguationData":[TD([[makeQuery(id+"F0.imprint","IMPRINT",EDGE,{"derivedFrom":sQuery(id+"F0.wireOp",EDGE,"0MEXwoFq-VW0W-JoZZ-MDqj-tHZCOfQ7mCeB")}),1.0]])]});
            var Q1;
            Q1=makeQuery(id+"F0.imprint","IMPRINT",FACE,{"disambiguationData":[TD([[makeQuery(id+"F0.imprint","IMPRINT",EDGE,{"derivedFrom":sQuery(id+"F0.wireOp",EDGE,"E0")}),-1.0]])]});
            extrude(context, id + "F1", {"entities" : qUnion([Q0, Q1]), "depth" : 20 * mm, "offsetDistance" : 25 * mm});
        }
        {
            var Q0;
            Q0=makeQuery(id+"F1.opExtrude","CAP_FACE",FACE,{"disambiguationData":[OSD([sQuery(id+"F0.wireOp",EDGE,"E0"),sQuery(id+"F0.wireOp",EDGE,"E4"),sQuery(id+"F0.wireOp",EDGE,"E5"),sQuery(id+"F0.wireOp",EDGE,"E6.filletArc"),sQuery(id+"F0.wireOp",EDGE,"E7.MirrorCS"),sQuery(id+"F0.wireOp",EDGE,"E8.MirrorCS"),sQuery(id+"F0.wireOp",EDGE,"E15"),sQuery(id+"F0.wireOp",EDGE,"E16.1.0"),sQuery(id+"F0.wireOp",EDGE,"E16.1.1"),sQuery(id+"F0.wireOp",EDGE,"E16.1.2"),sQuery(id+"F0.wireOp",EDGE,"E16.1.3"),sQuery(id+"F0.wireOp",EDGE,"E16.1.4"),sQuery(id+"F0.wireOp",EDGE,"E16.2.0"),sQuery(id+"F0.wireOp",EDGE,"E16.2.1"),sQuery(id+"F0.wireOp",EDGE,"E16.2.2"),sQuery(id+"F0.wireOp",EDGE,"E16.2.3"),sQuery(id+"F0.wireOp",EDGE,"E16.2.4"),sQuery(id+"F0.wireOp",EDGE,"E16.3.0"),sQuery(id+"F0.wireOp",EDGE,"E16.3.1"),sQuery(id+"F0.wireOp",EDGE,"E16.3.2"),sQuery(id+"F0.wireOp",EDGE,"E16.3.3"),sQuery(id+"F0.wireOp",EDGE,"E16.3.4"),sQuery(id+"F0.wireOp",EDGE,"E16.4.0"),sQuery(id+"F0.wireOp",EDGE,"E16.4.1"),sQuery(id+"F0.wireOp",EDGE,"E16.4.2"),sQuery(id+"F0.wireOp",EDGE,"E16.4.3"),sQuery(id+"F0.wireOp",EDGE,"E16.4.4"),sQuery(id+"F0.wireOp",EDGE,"E16.5.0"),sQuery(id+"F0.wireOp",EDGE,"E16.5.1"),sQuery(id+"F0.wireOp",EDGE,"E16.5.2"),sQuery(id+"F0.wireOp",EDGE,"E16.5.3"),sQuery(id+"F0.wireOp",EDGE,"E16.5.4"),sQuery(id+"F0.wireOp",EDGE,"E16.6.0"),sQuery(id+"F0.wireOp",EDGE,"E16.6.1"),sQuery(id+"F0.wireOp",EDGE,"E16.6.2"),sQuery(id+"F0.wireOp",EDGE,"E16.6.3"),sQuery(id+"F0.wireOp",EDGE,"E16.6.4"),sQuery(id+"F0.wireOp",EDGE,"E16.7.0"),sQuery(id+"F0.wireOp",EDGE,"E16.7.1"),sQuery(id+"F0.wireOp",EDGE,"E16.7.2"),sQuery(id+"F0.wireOp",EDGE,"E16.7.3"),sQuery(id+"F0.wireOp",EDGE,"E16.7.4"),sQuery(id+"F0.wireOp",EDGE,"E16.8.0"),sQuery(id+"F0.wireOp",EDGE,"E16.8.1"),sQuery(id+"F0.wireOp",EDGE,"E16.8.2"),sQuery(id+"F0.wireOp",EDGE,"E16.8.3"),sQuery(id+"F0.wireOp",EDGE,"E16.8.4"),sQuery(id+"F0.wireOp",EDGE,"E16.9.0"),sQuery(id+"F0.wireOp",EDGE,"E16.9.1"),sQuery(id+"F0.wireOp",EDGE,"E16.9.2"),sQuery(id+"F0.wireOp",EDGE,"E16.9.3"),sQuery(id+"F0.wireOp",EDGE,"E16.9.4"),sQuery(id+"F0.wireOp",EDGE,"E16.10.0"),sQuery(id+"F0.wireOp",EDGE,"E16.10.1"),sQuery(id+"F0.wireOp",EDGE,"E16.10.2"),sQuery(id+"F0.wireOp",EDGE,"E16.10.3"),sQuery(id+"F0.wireOp",EDGE,"E16.10.4"),sQuery(id+"F0.wireOp",EDGE,"E16.11.0"),sQuery(id+"F0.wireOp",EDGE,"E16.11.1"),sQuery(id+"F0.wireOp",EDGE,"E16.11.2"),sQuery(id+"F0.wireOp",EDGE,"E16.11.3"),sQuery(id+"F0.wireOp",EDGE,"E16.11.4"),sQuery(id+"F0.wireOp",EDGE,"E16.12.0"),sQuery(id+"F0.wireOp",EDGE,"E16.12.1"),sQuery(id+"F0.wireOp",EDGE,"E16.12.2"),sQuery(id+"F0.wireOp",EDGE,"E16.12.3"),sQuery(id+"F0.wireOp",EDGE,"E16.12.4"),sQuery(id+"F0.wireOp",EDGE,"E16.13.0"),sQuery(id+"F0.wireOp",EDGE,"E16.13.1"),sQuery(id+"F0.wireOp",EDGE,"E16.13.2"),sQuery(id+"F0.wireOp",EDGE,"E16.13.3"),sQuery(id+"F0.wireOp",EDGE,"E16.13.4"),sQuery(id+"F0.wireOp",EDGE,"E16.14.0"),sQuery(id+"F0.wireOp",EDGE,"E16.14.1"),sQuery(id+"F0.wireOp",EDGE,"E16.14.2"),sQuery(id+"F0.wireOp",EDGE,"E16.14.3"),sQuery(id+"F0.wireOp",EDGE,"E16.14.4"),sQuery(id+"F0.wireOp",EDGE,"E16.15.0"),sQuery(id+"F0.wireOp",EDGE,"E16.15.1"),sQuery(id+"F0.wireOp",EDGE,"E16.15.2"),sQuery(id+"F0.wireOp",EDGE,"E16.15.3"),sQuery(id+"F0.wireOp",EDGE,"E16.15.4"),sQuery(id+"F0.wireOp",EDGE,"E16.16.0"),sQuery(id+"F0.wireOp",EDGE,"E16.16.1"),sQuery(id+"F0.wireOp",EDGE,"E16.16.2"),sQuery(id+"F0.wireOp",EDGE,"E16.16.3"),sQuery(id+"F0.wireOp",EDGE,"E16.16.4"),sQuery(id+"F0.wireOp",EDGE,"E16.17.0"),sQuery(id+"F0.wireOp",EDGE,"E16.17.1"),sQuery(id+"F0.wireOp",EDGE,"E16.17.2"),sQuery(id+"F0.wireOp",EDGE,"E16.17.3"),sQuery(id+"F0.wireOp",EDGE,"E16.17.4"),sQuery(id+"F0.wireOp",EDGE,"E16.18.0"),sQuery(id+"F0.wireOp",EDGE,"E16.18.1"),sQuery(id+"F0.wireOp",EDGE,"E16.18.2"),sQuery(id+"F0.wireOp",EDGE,"E16.18.3"),sQuery(id+"F0.wireOp",EDGE,"E16.18.4"),sQuery(id+"F0.wireOp",EDGE,"E16.19.0"),sQuery(id+"F0.wireOp",EDGE,"E16.19.1"),sQuery(id+"F0.wireOp",EDGE,"E16.19.2"),sQuery(id+"F0.wireOp",EDGE,"E16.19.3"),sQuery(id+"F0.wireOp",EDGE,"E16.19.4"),sQuery(id+"F0.wireOp",EDGE,"E16.20.0"),sQuery(id+"F0.wireOp",EDGE,"E16.20.1"),sQuery(id+"F0.wireOp",EDGE,"E16.20.2"),sQuery(id+"F0.wireOp",EDGE,"E16.20.3"),sQuery(id+"F0.wireOp",EDGE,"E16.20.4"),sQuery(id+"F0.wireOp",EDGE,"E16.21.0"),sQuery(id+"F0.wireOp",EDGE,"E16.21.1"),sQuery(id+"F0.wireOp",EDGE,"E16.21.2"),sQuery(id+"F0.wireOp",EDGE,"E16.21.3"),sQuery(id+"F0.wireOp",EDGE,"E16.21.4"),sQuery(id+"F0.wireOp",EDGE,"E16.22.0"),sQuery(id+"F0.wireOp",EDGE,"E16.22.1"),sQuery(id+"F0.wireOp",EDGE,"E16.22.2"),sQuery(id+"F0.wireOp",EDGE,"E16.22.3"),sQuery(id+"F0.wireOp",EDGE,"E16.22.4"),sQuery(id+"F0.wireOp",EDGE,"E16.23.0"),sQuery(id+"F0.wireOp",EDGE,"E16.23.1"),sQuery(id+"F0.wireOp",EDGE,"E16.23.2"),sQuery(id+"F0.wireOp",EDGE,"E16.23.3"),sQuery(id+"F0.wireOp",EDGE,"E16.23.4"),sQuery(id+"F0.wireOp",EDGE,"E16.24.0"),sQuery(id+"F0.wireOp",EDGE,"E16.24.1"),sQuery(id+"F0.wireOp",EDGE,"E16.24.2"),sQuery(id+"F0.wireOp",EDGE,"E16.24.3"),sQuery(id+"F0.wireOp",EDGE,"E16.24.4"),sQuery(id+"F0.wireOp",EDGE,"E16.25.0"),sQuery(id+"F0.wireOp",EDGE,"E16.25.1"),sQuery(id+"F0.wireOp",EDGE,"E16.25.2"),sQuery(id+"F0.wireOp",EDGE,"E16.25.3"),sQuery(id+"F0.wireOp",EDGE,"E16.25.4"),sQuery(id+"F0.wireOp",EDGE,"E16.26.0"),sQuery(id+"F0.wireOp",EDGE,"E16.26.1"),sQuery(id+"F0.wireOp",EDGE,"E16.26.2"),sQuery(id+"F0.wireOp",EDGE,"E16.26.3"),sQuery(id+"F0.wireOp",EDGE,"E16.26.4"),sQuery(id+"F0.wireOp",EDGE,"E16.27.0"),sQuery(id+"F0.wireOp",EDGE,"E16.27.1"),sQuery(id+"F0.wireOp",EDGE,"E16.27.2"),sQuery(id+"F0.wireOp",EDGE,"E16.27.3"),sQuery(id+"F0.wireOp",EDGE,"E16.27.4"),sQuery(id+"F0.wireOp",EDGE,"E16.28.0"),sQuery(id+"F0.wireOp",EDGE,"E16.28.1"),sQuery(id+"F0.wireOp",EDGE,"E16.28.2"),sQuery(id+"F0.wireOp",EDGE,"E16.28.3"),sQuery(id+"F0.wireOp",EDGE,"E16.28.4"),sQuery(id+"F0.wireOp",EDGE,"E16.29.0"),sQuery(id+"F0.wireOp",EDGE,"E16.29.1"),sQuery(id+"F0.wireOp",EDGE,"E16.29.2"),sQuery(id+"F0.wireOp",EDGE,"E16.29.3"),sQuery(id+"F0.wireOp",EDGE,"E16.29.4"),sQuery(id+"F0.wireOp",EDGE,"E16.30.0"),sQuery(id+"F0.wireOp",EDGE,"E16.30.1"),sQuery(id+"F0.wireOp",EDGE,"E16.30.2"),sQuery(id+"F0.wireOp",EDGE,"E16.30.3"),sQuery(id+"F0.wireOp",EDGE,"E16.30.4"),sQuery(id+"F0.wireOp",EDGE,"E16.31.0"),sQuery(id+"F0.wireOp",EDGE,"E16.31.1"),sQuery(id+"F0.wireOp",EDGE,"E16.31.2"),sQuery(id+"F0.wireOp",EDGE,"E16.31.3"),sQuery(id+"F0.wireOp",EDGE,"E16.31.4"),sQuery(id+"F0.wireOp",EDGE,"E16.32.0"),sQuery(id+"F0.wireOp",EDGE,"E16.32.1"),sQuery(id+"F0.wireOp",EDGE,"E16.32.2"),sQuery(id+"F0.wireOp",EDGE,"E16.32.3"),sQuery(id+"F0.wireOp",EDGE,"E16.32.4"),sQuery(id+"F0.wireOp",EDGE,"E16.33.0"),sQuery(id+"F0.wireOp",EDGE,"E16.33.1"),sQuery(id+"F0.wireOp",EDGE,"E16.33.2"),sQuery(id+"F0.wireOp",EDGE,"E16.33.3"),sQuery(id+"F0.wireOp",EDGE,"E16.33.4"),sQuery(id+"F0.wireOp",EDGE,"E16.34.0"),sQuery(id+"F0.wireOp",EDGE,"E16.34.1"),sQuery(id+"F0.wireOp",EDGE,"E16.34.2"),sQuery(id+"F0.wireOp",EDGE,"E16.34.3"),sQuery(id+"F0.wireOp",EDGE,"E16.34.4"),sQuery(id+"F0.wireOp",EDGE,"E16.35.0"),sQuery(id+"F0.wireOp",EDGE,"E16.35.1"),sQuery(id+"F0.wireOp",EDGE,"E16.35.2"),sQuery(id+"F0.wireOp",EDGE,"E16.35.3"),sQuery(id+"F0.wireOp",EDGE,"E16.35.4"),sQuery(id+"F0.wireOp",EDGE,"E16.36.0"),sQuery(id+"F0.wireOp",EDGE,"E16.36.1"),sQuery(id+"F0.wireOp",EDGE,"E16.36.2"),sQuery(id+"F0.wireOp",EDGE,"E16.36.3"),sQuery(id+"F0.wireOp",EDGE,"E16.36.4"),sQuery(id+"F0.wireOp",EDGE,"E16.37.0"),sQuery(id+"F0.wireOp",EDGE,"E16.37.1"),sQuery(id+"F0.wireOp",EDGE,"E16.37.2"),sQuery(id+"F0.wireOp",EDGE,"E16.37.3"),sQuery(id+"F0.wireOp",EDGE,"E16.37.4"),sQuery(id+"F0.wireOp",EDGE,"E16.38.0"),sQuery(id+"F0.wireOp",EDGE,"E16.38.1"),sQuery(id+"F0.wireOp",EDGE,"E16.38.2"),sQuery(id+"F0.wireOp",EDGE,"E16.38.3"),sQuery(id+"F0.wireOp",EDGE,"E16.38.4"),sQuery(id+"F0.wireOp",EDGE,"E16.39.0"),sQuery(id+"F0.wireOp",EDGE,"E16.39.1"),sQuery(id+"F0.wireOp",EDGE,"E16.39.2"),sQuery(id+"F0.wireOp",EDGE,"E16.39.3"),sQuery(id+"F0.wireOp",EDGE,"E16.39.4"),sQuery(id+"F0.wireOp",EDGE,"E16.40.0"),sQuery(id+"F0.wireOp",EDGE,"E16.40.1"),sQuery(id+"F0.wireOp",EDGE,"E16.40.2"),sQuery(id+"F0.wireOp",EDGE,"E16.40.3"),sQuery(id+"F0.wireOp",EDGE,"E16.40.4"),sQuery(id+"F0.wireOp",EDGE,"E16.41.0"),sQuery(id+"F0.wireOp",EDGE,"E16.41.1"),sQuery(id+"F0.wireOp",EDGE,"E16.41.2"),sQuery(id+"F0.wireOp",EDGE,"E16.41.3"),sQuery(id+"F0.wireOp",EDGE,"E16.41.4"),sQuery(id+"F0.wireOp",EDGE,"E16.42.0"),sQuery(id+"F0.wireOp",EDGE,"E16.42.1"),sQuery(id+"F0.wireOp",EDGE,"E16.42.2"),sQuery(id+"F0.wireOp",EDGE,"E16.42.3"),sQuery(id+"F0.wireOp",EDGE,"E16.42.4"),sQuery(id+"F0.wireOp",EDGE,"E16.43.0"),sQuery(id+"F0.wireOp",EDGE,"E16.43.1"),sQuery(id+"F0.wireOp",EDGE,"E16.43.2"),sQuery(id+"F0.wireOp",EDGE,"E16.43.3"),sQuery(id+"F0.wireOp",EDGE,"E16.43.4"),sQuery(id+"F0.wireOp",EDGE,"E16.44.0"),sQuery(id+"F0.wireOp",EDGE,"E16.44.1"),sQuery(id+"F0.wireOp",EDGE,"E16.44.2"),sQuery(id+"F0.wireOp",EDGE,"E16.44.3"),sQuery(id+"F0.wireOp",EDGE,"E16.44.4"),sQuery(id+"F0.wireOp",EDGE,"E16.45.0"),sQuery(id+"F0.wireOp",EDGE,"E16.45.1"),sQuery(id+"F0.wireOp",EDGE,"E16.45.2"),sQuery(id+"F0.wireOp",EDGE,"E16.45.3"),sQuery(id+"F0.wireOp",EDGE,"E16.45.4"),sQuery(id+"F0.wireOp",EDGE,"E16.46.0"),sQuery(id+"F0.wireOp",EDGE,"E16.46.1"),sQuery(id+"F0.wireOp",EDGE,"E16.46.2"),sQuery(id+"F0.wireOp",EDGE,"E16.46.3"),sQuery(id+"F0.wireOp",EDGE,"E16.46.4"),sQuery(id+"F0.wireOp",EDGE,"E16.47.0"),sQuery(id+"F0.wireOp",EDGE,"E16.47.1"),sQuery(id+"F0.wireOp",EDGE,"E16.47.2"),sQuery(id+"F0.wireOp",EDGE,"E16.47.3"),sQuery(id+"F0.wireOp",EDGE,"E16.47.4"),sQuery(id+"F0.wireOp",EDGE,"E16.48.0"),sQuery(id+"F0.wireOp",EDGE,"E16.48.1"),sQuery(id+"F0.wireOp",EDGE,"E16.48.2"),sQuery(id+"F0.wireOp",EDGE,"E16.48.3"),sQuery(id+"F0.wireOp",EDGE,"E16.48.4"),sQuery(id+"F0.wireOp",EDGE,"E16.49.0"),sQuery(id+"F0.wireOp",EDGE,"E16.49.1"),sQuery(id+"F0.wireOp",EDGE,"E16.49.2"),sQuery(id+"F0.wireOp",EDGE,"E16.49.3"),sQuery(id+"F0.wireOp",EDGE,"E16.49.4"),sQuery(id+"F0.wireOp",EDGE,"E16.50.0"),sQuery(id+"F0.wireOp",EDGE,"E16.50.1"),sQuery(id+"F0.wireOp",EDGE,"E16.50.2"),sQuery(id+"F0.wireOp",EDGE,"E16.50.3"),sQuery(id+"F0.wireOp",EDGE,"E16.50.4"),sQuery(id+"F0.wireOp",EDGE,"E16.51.0"),sQuery(id+"F0.wireOp",EDGE,"E16.51.1"),sQuery(id+"F0.wireOp",EDGE,"E16.51.2"),sQuery(id+"F0.wireOp",EDGE,"E16.51.3"),sQuery(id+"F0.wireOp",EDGE,"E16.51.4"),sQuery(id+"F0.wireOp",EDGE,"E16.52.0"),sQuery(id+"F0.wireOp",EDGE,"E16.52.1"),sQuery(id+"F0.wireOp",EDGE,"E16.52.2"),sQuery(id+"F0.wireOp",EDGE,"E16.52.3"),sQuery(id+"F0.wireOp",EDGE,"E16.52.4"),sQuery(id+"F0.wireOp",EDGE,"E16.53.0"),sQuery(id+"F0.wireOp",EDGE,"E16.53.1"),sQuery(id+"F0.wireOp",EDGE,"E16.53.2"),sQuery(id+"F0.wireOp",EDGE,"E16.53.3"),sQuery(id+"F0.wireOp",EDGE,"E16.53.4"),sQuery(id+"F0.wireOp",EDGE,"E16.54.0"),sQuery(id+"F0.wireOp",EDGE,"E16.54.1"),sQuery(id+"F0.wireOp",EDGE,"E16.54.2"),sQuery(id+"F0.wireOp",EDGE,"E16.54.3"),sQuery(id+"F0.wireOp",EDGE,"E16.54.4"),sQuery(id+"F0.wireOp",EDGE,"E16.55.0"),sQuery(id+"F0.wireOp",EDGE,"E16.55.1"),sQuery(id+"F0.wireOp",EDGE,"E16.55.2"),sQuery(id+"F0.wireOp",EDGE,"E16.55.3"),sQuery(id+"F0.wireOp",EDGE,"E16.55.4"),sQuery(id+"F0.wireOp",EDGE,"E16.56.0"),sQuery(id+"F0.wireOp",EDGE,"E16.56.1"),sQuery(id+"F0.wireOp",EDGE,"E16.56.2"),sQuery(id+"F0.wireOp",EDGE,"E16.56.3"),sQuery(id+"F0.wireOp",EDGE,"E16.56.4"),sQuery(id+"F0.wireOp",EDGE,"E16.57.0"),sQuery(id+"F0.wireOp",EDGE,"E16.57.1"),sQuery(id+"F0.wireOp",EDGE,"E16.57.2"),sQuery(id+"F0.wireOp",EDGE,"E16.57.3"),sQuery(id+"F0.wireOp",EDGE,"E16.57.4"),sQuery(id+"F0.wireOp",EDGE,"E16.58.0"),sQuery(id+"F0.wireOp",EDGE,"E16.58.1"),sQuery(id+"F0.wireOp",EDGE,"E16.58.2"),sQuery(id+"F0.wireOp",EDGE,"E16.58.3"),sQuery(id+"F0.wireOp",EDGE,"E16.58.4"),sQuery(id+"F0.wireOp",EDGE,"E16.59.0"),sQuery(id+"F0.wireOp",EDGE,"E16.59.1"),sQuery(id+"F0.wireOp",EDGE,"E16.59.2"),sQuery(id+"F0.wireOp",EDGE,"E16.59.3"),sQuery(id+"F0.wireOp",EDGE,"E16.59.4"),sQuery(id+"F0.wireOp",EDGE,"E16.60.0"),sQuery(id+"F0.wireOp",EDGE,"E16.60.1"),sQuery(id+"F0.wireOp",EDGE,"E16.60.2"),sQuery(id+"F0.wireOp",EDGE,"E16.60.3"),sQuery(id+"F0.wireOp",EDGE,"E16.60.4"),sQuery(id+"F0.wireOp",EDGE,"E16.61.0"),sQuery(id+"F0.wireOp",EDGE,"E16.61.1"),sQuery(id+"F0.wireOp",EDGE,"E16.61.2"),sQuery(id+"F0.wireOp",EDGE,"E16.61.3"),sQuery(id+"F0.wireOp",EDGE,"E16.61.4"),sQuery(id+"F0.wireOp",EDGE,"E16.62.0"),sQuery(id+"F0.wireOp",EDGE,"E16.62.1"),sQuery(id+"F0.wireOp",EDGE,"E16.62.2"),sQuery(id+"F0.wireOp",EDGE,"E16.62.3"),sQuery(id+"F0.wireOp",EDGE,"E16.62.4"),sQuery(id+"F0.wireOp",EDGE,"E16.63.0"),sQuery(id+"F0.wireOp",EDGE,"E16.63.1"),sQuery(id+"F0.wireOp",EDGE,"E16.63.2"),sQuery(id+"F0.wireOp",EDGE,"E16.63.3"),sQuery(id+"F0.wireOp",EDGE,"E16.63.4"),sQuery(id+"F0.wireOp",EDGE,"E16.64.0"),sQuery(id+"F0.wireOp",EDGE,"E16.64.1"),sQuery(id+"F0.wireOp",EDGE,"E16.64.2"),sQuery(id+"F0.wireOp",EDGE,"E16.64.3"),sQuery(id+"F0.wireOp",EDGE,"E16.64.4"),sQuery(id+"F0.wireOp",EDGE,"E16.65.0"),sQuery(id+"F0.wireOp",EDGE,"E16.65.1"),sQuery(id+"F0.wireOp",EDGE,"E16.65.2"),sQuery(id+"F0.wireOp",EDGE,"E16.65.3"),sQuery(id+"F0.wireOp",EDGE,"E16.65.4"),sQuery(id+"F0.wireOp",EDGE,"E16.66.0"),sQuery(id+"F0.wireOp",EDGE,"E16.66.1"),sQuery(id+"F0.wireOp",EDGE,"E16.66.2"),sQuery(id+"F0.wireOp",EDGE,"E16.66.3"),sQuery(id+"F0.wireOp",EDGE,"E16.66.4"),sQuery(id+"F0.wireOp",EDGE,"E16.67.0"),sQuery(id+"F0.wireOp",EDGE,"E16.67.1"),sQuery(id+"F0.wireOp",EDGE,"E16.67.2"),sQuery(id+"F0.wireOp",EDGE,"E16.67.3"),sQuery(id+"F0.wireOp",EDGE,"E16.67.4"),sQuery(id+"F0.wireOp",EDGE,"E16.68.0"),sQuery(id+"F0.wireOp",EDGE,"E16.68.1"),sQuery(id+"F0.wireOp",EDGE,"E16.68.2"),sQuery(id+"F0.wireOp",EDGE,"E16.68.3"),sQuery(id+"F0.wireOp",EDGE,"E16.68.4"),sQuery(id+"F0.wireOp",EDGE,"E16.69.0"),sQuery(id+"F0.wireOp",EDGE,"E16.69.1"),sQuery(id+"F0.wireOp",EDGE,"E16.69.2"),sQuery(id+"F0.wireOp",EDGE,"E16.69.3"),sQuery(id+"F0.wireOp",EDGE,"E16.69.4"),sQuery(id+"F0.wireOp",EDGE,"E16.70.0"),sQuery(id+"F0.wireOp",EDGE,"E16.70.1"),sQuery(id+"F0.wireOp",EDGE,"E16.70.2"),sQuery(id+"F0.wireOp",EDGE,"E16.70.3"),sQuery(id+"F0.wireOp",EDGE,"E16.70.4"),sQuery(id+"F0.wireOp",EDGE,"E16.71.0"),sQuery(id+"F0.wireOp",EDGE,"E16.71.1"),sQuery(id+"F0.wireOp",EDGE,"E16.71.2"),sQuery(id+"F0.wireOp",EDGE,"E16.71.3"),sQuery(id+"F0.wireOp",EDGE,"E16.71.4"),sQuery(id+"F0.wireOp",EDGE,"E16.72.0"),sQuery(id+"F0.wireOp",EDGE,"E16.72.1"),sQuery(id+"F0.wireOp",EDGE,"E16.72.2"),sQuery(id+"F0.wireOp",EDGE,"E16.72.3"),sQuery(id+"F0.wireOp",EDGE,"E16.72.4"),sQuery(id+"F0.wireOp",EDGE,"E16.73.0"),sQuery(id+"F0.wireOp",EDGE,"E16.73.1"),sQuery(id+"F0.wireOp",EDGE,"E16.73.2"),sQuery(id+"F0.wireOp",EDGE,"E16.73.3"),sQuery(id+"F0.wireOp",EDGE,"E16.73.4"),sQuery(id+"F0.wireOp",EDGE,"E16.74.0"),sQuery(id+"F0.wireOp",EDGE,"E16.74.1"),sQuery(id+"F0.wireOp",EDGE,"E16.74.2"),sQuery(id+"F0.wireOp",EDGE,"E16.74.3"),sQuery(id+"F0.wireOp",EDGE,"E16.74.4"),sQuery(id+"F0.wireOp",EDGE,"E16.75.0"),sQuery(id+"F0.wireOp",EDGE,"E16.75.1"),sQuery(id+"F0.wireOp",EDGE,"E16.75.2"),sQuery(id+"F0.wireOp",EDGE,"E16.75.3"),sQuery(id+"F0.wireOp",EDGE,"E16.75.4"),sQuery(id+"F0.wireOp",EDGE,"E16.76.0"),sQuery(id+"F0.wireOp",EDGE,"E16.76.1"),sQuery(id+"F0.wireOp",EDGE,"E16.76.2"),sQuery(id+"F0.wireOp",EDGE,"E16.76.3"),sQuery(id+"F0.wireOp",EDGE,"E16.76.4"),sQuery(id+"F0.wireOp",EDGE,"E16.77.0"),sQuery(id+"F0.wireOp",EDGE,"E16.77.1"),sQuery(id+"F0.wireOp",EDGE,"E16.77.2"),sQuery(id+"F0.wireOp",EDGE,"E16.77.3"),sQuery(id+"F0.wireOp",EDGE,"E16.77.4"),sQuery(id+"F0.wireOp",EDGE,"E16.78.0"),sQuery(id+"F0.wireOp",EDGE,"E16.78.1"),sQuery(id+"F0.wireOp",EDGE,"E16.78.2"),sQuery(id+"F0.wireOp",EDGE,"E16.78.3"),sQuery(id+"F0.wireOp",EDGE,"E16.78.4"),sQuery(id+"F0.wireOp",EDGE,"E16.79.0"),sQuery(id+"F0.wireOp",EDGE,"E16.79.1"),sQuery(id+"F0.wireOp",EDGE,"E16.79.2"),sQuery(id+"F0.wireOp",EDGE,"E16.79.3"),sQuery(id+"F0.wireOp",EDGE,"E16.79.4"),sQuery(id+"F0.wireOp",EDGE,"E16.80.0"),sQuery(id+"F0.wireOp",EDGE,"E16.80.1"),sQuery(id+"F0.wireOp",EDGE,"E16.80.2"),sQuery(id+"F0.wireOp",EDGE,"E16.80.3"),sQuery(id+"F0.wireOp",EDGE,"E16.80.4"),sQuery(id+"F0.wireOp",EDGE,"E16.81.0"),sQuery(id+"F0.wireOp",EDGE,"E16.81.1"),sQuery(id+"F0.wireOp",EDGE,"E16.81.2"),sQuery(id+"F0.wireOp",EDGE,"E16.81.3"),sQuery(id+"F0.wireOp",EDGE,"E16.81.4"),sQuery(id+"F0.wireOp",EDGE,"E16.82.0"),sQuery(id+"F0.wireOp",EDGE,"E16.82.1"),sQuery(id+"F0.wireOp",EDGE,"E16.82.2"),sQuery(id+"F0.wireOp",EDGE,"E16.82.3"),sQuery(id+"F0.wireOp",EDGE,"E16.82.4"),sQuery(id+"F0.wireOp",EDGE,"E16.83.0"),sQuery(id+"F0.wireOp",EDGE,"E16.83.1"),sQuery(id+"F0.wireOp",EDGE,"E16.83.2"),sQuery(id+"F0.wireOp",EDGE,"E16.83.3"),sQuery(id+"F0.wireOp",EDGE,"E16.83.4"),sQuery(id+"F0.wireOp",EDGE,"E16.84.0"),sQuery(id+"F0.wireOp",EDGE,"E16.84.1"),sQuery(id+"F0.wireOp",EDGE,"E16.84.2"),sQuery(id+"F0.wireOp",EDGE,"E16.84.3"),sQuery(id+"F0.wireOp",EDGE,"E16.84.4"),sQuery(id+"F0.wireOp",EDGE,"E16.85.0"),sQuery(id+"F0.wireOp",EDGE,"E16.85.1"),sQuery(id+"F0.wireOp",EDGE,"E16.85.2"),sQuery(id+"F0.wireOp",EDGE,"E16.85.3"),sQuery(id+"F0.wireOp",EDGE,"E16.85.4"),sQuery(id+"F0.wireOp",EDGE,"E16.86.0"),sQuery(id+"F0.wireOp",EDGE,"E16.86.1"),sQuery(id+"F0.wireOp",EDGE,"E16.86.2"),sQuery(id+"F0.wireOp",EDGE,"E16.86.3"),sQuery(id+"F0.wireOp",EDGE,"E16.86.4"),sQuery(id+"F0.wireOp",EDGE,"E16.87.0"),sQuery(id+"F0.wireOp",EDGE,"E16.87.1"),sQuery(id+"F0.wireOp",EDGE,"E16.87.2"),sQuery(id+"F0.wireOp",EDGE,"E16.87.3"),sQuery(id+"F0.wireOp",EDGE,"E16.87.4"),sQuery(id+"F0.wireOp",EDGE,"E16.88.0"),sQuery(id+"F0.wireOp",EDGE,"E16.88.1"),sQuery(id+"F0.wireOp",EDGE,"E16.88.2"),sQuery(id+"F0.wireOp",EDGE,"E16.88.3"),sQuery(id+"F0.wireOp",EDGE,"E16.88.4"),sQuery(id+"F0.wireOp",EDGE,"E16.89.0"),sQuery(id+"F0.wireOp",EDGE,"E16.89.1"),sQuery(id+"F0.wireOp",EDGE,"E16.89.2"),sQuery(id+"F0.wireOp",EDGE,"E16.89.3"),sQuery(id+"F0.wireOp",EDGE,"E16.89.4"),sQuery(id+"F0.wireOp",EDGE,"E16.90.0"),sQuery(id+"F0.wireOp",EDGE,"E16.90.1"),sQuery(id+"F0.wireOp",EDGE,"E16.90.2"),sQuery(id+"F0.wireOp",EDGE,"E16.90.3"),sQuery(id+"F0.wireOp",EDGE,"E16.90.4"),sQuery(id+"F0.wireOp",EDGE,"E16.91.0"),sQuery(id+"F0.wireOp",EDGE,"E16.91.1"),sQuery(id+"F0.wireOp",EDGE,"E16.91.2"),sQuery(id+"F0.wireOp",EDGE,"E16.91.3"),sQuery(id+"F0.wireOp",EDGE,"E16.91.4"),sQuery(id+"F0.wireOp",EDGE,"E16.92.0"),sQuery(id+"F0.wireOp",EDGE,"E16.92.1"),sQuery(id+"F0.wireOp",EDGE,"E16.92.2"),sQuery(id+"F0.wireOp",EDGE,"E16.92.3"),sQuery(id+"F0.wireOp",EDGE,"E16.92.4"),sQuery(id+"F0.wireOp",EDGE,"E16.93.0"),sQuery(id+"F0.wireOp",EDGE,"E16.93.1"),sQuery(id+"F0.wireOp",EDGE,"E16.93.2"),sQuery(id+"F0.wireOp",EDGE,"E16.93.3"),sQuery(id+"F0.wireOp",EDGE,"E16.93.4"),sQuery(id+"F0.wireOp",EDGE,"E16.94.0"),sQuery(id+"F0.wireOp",EDGE,"E16.94.1"),sQuery(id+"F0.wireOp",EDGE,"E16.94.2"),sQuery(id+"F0.wireOp",EDGE,"E16.94.3"),sQuery(id+"F0.wireOp",EDGE,"E16.94.4"),sQuery(id+"F0.wireOp",EDGE,"E16.95.0"),sQuery(id+"F0.wireOp",EDGE,"E16.95.1"),sQuery(id+"F0.wireOp",EDGE,"E16.95.2"),sQuery(id+"F0.wireOp",EDGE,"E16.95.3"),sQuery(id+"F0.wireOp",EDGE,"E16.95.4"),sQuery(id+"F0.wireOp",EDGE,"E16.96.0"),sQuery(id+"F0.wireOp",EDGE,"E16.96.1"),sQuery(id+"F0.wireOp",EDGE,"E16.96.2"),sQuery(id+"F0.wireOp",EDGE,"E16.96.3"),sQuery(id+"F0.wireOp",EDGE,"E16.96.4"),sQuery(id+"F0.wireOp",EDGE,"E16.97.0"),sQuery(id+"F0.wireOp",EDGE,"E16.97.1"),sQuery(id+"F0.wireOp",EDGE,"E16.97.2"),sQuery(id+"F0.wireOp",EDGE,"E16.97.3"),sQuery(id+"F0.wireOp",EDGE,"E16.97.4"),sQuery(id+"F0.wireOp",EDGE,"E16.98.0"),sQuery(id+"F0.wireOp",EDGE,"E16.98.1"),sQuery(id+"F0.wireOp",EDGE,"E16.98.2"),sQuery(id+"F0.wireOp",EDGE,"E16.98.3"),sQuery(id+"F0.wireOp",EDGE,"E16.98.4"),sQuery(id+"F0.wireOp",EDGE,"E16.99.0"),sQuery(id+"F0.wireOp",EDGE,"E16.99.1"),sQuery(id+"F0.wireOp",EDGE,"E16.99.2"),sQuery(id+"F0.wireOp",EDGE,"E16.99.3"),sQuery(id+"F0.wireOp",EDGE,"E16.99.4"),sQuery(id+"F0.wireOp",EDGE,"E16.100.0"),sQuery(id+"F0.wireOp",EDGE,"E16.100.1"),sQuery(id+"F0.wireOp",EDGE,"E16.100.2"),sQuery(id+"F0.wireOp",EDGE,"E16.100.3"),sQuery(id+"F0.wireOp",EDGE,"E16.100.4"),sQuery(id+"F0.wireOp",EDGE,"E16.101.0"),sQuery(id+"F0.wireOp",EDGE,"E16.101.1"),sQuery(id+"F0.wireOp",EDGE,"E16.101.2"),sQuery(id+"F0.wireOp",EDGE,"E16.101.3"),sQuery(id+"F0.wireOp",EDGE,"E16.101.4"),sQuery(id+"F0.wireOp",EDGE,"E16.102.0"),sQuery(id+"F0.wireOp",EDGE,"E16.102.1"),sQuery(id+"F0.wireOp",EDGE,"E16.102.2"),sQuery(id+"F0.wireOp",EDGE,"E16.102.3"),sQuery(id+"F0.wireOp",EDGE,"E16.102.4"),sQuery(id+"F0.wireOp",EDGE,"E16.103.0"),sQuery(id+"F0.wireOp",EDGE,"E16.103.1"),sQuery(id+"F0.wireOp",EDGE,"E16.103.2"),sQuery(id+"F0.wireOp",EDGE,"E16.103.3"),sQuery(id+"F0.wireOp",EDGE,"E16.103.4"),sQuery(id+"F0.wireOp",EDGE,"E16.104.0"),sQuery(id+"F0.wireOp",EDGE,"E16.104.1"),sQuery(id+"F0.wireOp",EDGE,"E16.104.2"),sQuery(id+"F0.wireOp",EDGE,"E16.104.3"),sQuery(id+"F0.wireOp",EDGE,"E16.104.4"),sQuery(id+"F0.wireOp",EDGE,"E16.105.0"),sQuery(id+"F0.wireOp",EDGE,"E16.105.1"),sQuery(id+"F0.wireOp",EDGE,"E16.105.2"),sQuery(id+"F0.wireOp",EDGE,"E16.105.3"),sQuery(id+"F0.wireOp",EDGE,"E16.105.4"),sQuery(id+"F0.wireOp",EDGE,"E16.106.0"),sQuery(id+"F0.wireOp",EDGE,"E16.106.1"),sQuery(id+"F0.wireOp",EDGE,"E16.106.2"),sQuery(id+"F0.wireOp",EDGE,"E16.106.3"),sQuery(id+"F0.wireOp",EDGE,"E16.106.4"),sQuery(id+"F0.wireOp",EDGE,"E16.107.0"),sQuery(id+"F0.wireOp",EDGE,"E16.107.1"),sQuery(id+"F0.wireOp",EDGE,"E16.107.2"),sQuery(id+"F0.wireOp",EDGE,"E16.107.3"),sQuery(id+"F0.wireOp",EDGE,"E16.107.4"),sQuery(id+"F0.wireOp",EDGE,"E16.108.0"),sQuery(id+"F0.wireOp",EDGE,"E16.108.1"),sQuery(id+"F0.wireOp",EDGE,"E16.108.2"),sQuery(id+"F0.wireOp",EDGE,"E16.108.3"),sQuery(id+"F0.wireOp",EDGE,"E16.108.4"),sQuery(id+"F0.wireOp",EDGE,"E16.109.0"),sQuery(id+"F0.wireOp",EDGE,"E16.109.1"),sQuery(id+"F0.wireOp",EDGE,"E16.109.2"),sQuery(id+"F0.wireOp",EDGE,"E16.109.3"),sQuery(id+"F0.wireOp",EDGE,"E16.109.4"),sQuery(id+"F0.wireOp",EDGE,"E16.110.0"),sQuery(id+"F0.wireOp",EDGE,"E16.110.1"),sQuery(id+"F0.wireOp",EDGE,"E16.110.2"),sQuery(id+"F0.wireOp",EDGE,"E16.110.3"),sQuery(id+"F0.wireOp",EDGE,"E16.110.4"),sQuery(id+"F0.wireOp",EDGE,"E16.111.0"),sQuery(id+"F0.wireOp",EDGE,"E16.111.1"),sQuery(id+"F0.wireOp",EDGE,"E16.111.2"),sQuery(id+"F0.wireOp",EDGE,"E16.111.3"),sQuery(id+"F0.wireOp",EDGE,"E16.111.4"),sQuery(id+"F0.wireOp",EDGE,"E16.112.0"),sQuery(id+"F0.wireOp",EDGE,"E16.112.1"),sQuery(id+"F0.wireOp",EDGE,"E16.112.2"),sQuery(id+"F0.wireOp",EDGE,"E16.112.3"),sQuery(id+"F0.wireOp",EDGE,"E16.112.4"),sQuery(id+"F0.wireOp",EDGE,"E16.113.0"),sQuery(id+"F0.wireOp",EDGE,"E16.113.1"),sQuery(id+"F0.wireOp",EDGE,"E16.113.2"),sQuery(id+"F0.wireOp",EDGE,"E16.113.3"),sQuery(id+"F0.wireOp",EDGE,"E16.113.4"),sQuery(id+"F0.wireOp",EDGE,"E16.114.0"),sQuery(id+"F0.wireOp",EDGE,"E16.114.1"),sQuery(id+"F0.wireOp",EDGE,"E16.114.2"),sQuery(id+"F0.wireOp",EDGE,"E16.114.3"),sQuery(id+"F0.wireOp",EDGE,"E16.114.4"),sQuery(id+"F0.wireOp",EDGE,"E16.115.0"),sQuery(id+"F0.wireOp",EDGE,"E16.115.1"),sQuery(id+"F0.wireOp",EDGE,"E16.115.2"),sQuery(id+"F0.wireOp",EDGE,"E16.115.3"),sQuery(id+"F0.wireOp",EDGE,"E16.115.4"),sQuery(id+"F0.wireOp",EDGE,"E16.116.0"),sQuery(id+"F0.wireOp",EDGE,"E16.116.1"),sQuery(id+"F0.wireOp",EDGE,"E16.116.2"),sQuery(id+"F0.wireOp",EDGE,"E16.116.3"),sQuery(id+"F0.wireOp",EDGE,"E16.116.4"),sQuery(id+"F0.wireOp",EDGE,"E16.117.0"),sQuery(id+"F0.wireOp",EDGE,"E16.117.1"),sQuery(id+"F0.wireOp",EDGE,"E16.117.2"),sQuery(id+"F0.wireOp",EDGE,"E16.117.3"),sQuery(id+"F0.wireOp",EDGE,"E16.117.4"),sQuery(id+"F0.wireOp",EDGE,"E16.118.0"),sQuery(id+"F0.wireOp",EDGE,"E16.118.1"),sQuery(id+"F0.wireOp",EDGE,"E16.118.2"),sQuery(id+"F0.wireOp",EDGE,"E16.118.3"),sQuery(id+"F0.wireOp",EDGE,"E16.118.4"),sQuery(id+"F0.wireOp",EDGE,"E16.119.0"),sQuery(id+"F0.wireOp",EDGE,"E16.119.1"),sQuery(id+"F0.wireOp",EDGE,"E16.119.2"),sQuery(id+"F0.wireOp",EDGE,"E16.119.3"),sQuery(id+"F0.wireOp",EDGE,"E16.119.4"),sQuery(id+"F0.wireOp",EDGE,"E16.120.0"),sQuery(id+"F0.wireOp",EDGE,"E16.120.1"),sQuery(id+"F0.wireOp",EDGE,"E16.120.2"),sQuery(id+"F0.wireOp",EDGE,"E16.120.3"),sQuery(id+"F0.wireOp",EDGE,"E16.120.4"),sQuery(id+"F0.wireOp",EDGE,"E16.121.0"),sQuery(id+"F0.wireOp",EDGE,"E16.121.1"),sQuery(id+"F0.wireOp",EDGE,"E16.121.2"),sQuery(id+"F0.wireOp",EDGE,"E16.121.3"),sQuery(id+"F0.wireOp",EDGE,"E16.121.4"),sQuery(id+"F0.wireOp",EDGE,"E16.122.0"),sQuery(id+"F0.wireOp",EDGE,"E16.122.1"),sQuery(id+"F0.wireOp",EDGE,"E16.122.2"),sQuery(id+"F0.wireOp",EDGE,"E16.122.3"),sQuery(id+"F0.wireOp",EDGE,"E16.122.4"),sQuery(id+"F0.wireOp",EDGE,"E16.123.0"),sQuery(id+"F0.wireOp",EDGE,"E16.123.1"),sQuery(id+"F0.wireOp",EDGE,"E16.123.2"),sQuery(id+"F0.wireOp",EDGE,"E16.123.3"),sQuery(id+"F0.wireOp",EDGE,"E16.123.4"),sQuery(id+"F0.wireOp",EDGE,"E16.124.0"),sQuery(id+"F0.wireOp",EDGE,"E16.124.1"),sQuery(id+"F0.wireOp",EDGE,"E16.124.2"),sQuery(id+"F0.wireOp",EDGE,"E16.124.3"),sQuery(id+"F0.wireOp",EDGE,"E16.124.4"),sQuery(id+"F0.wireOp",EDGE,"E16.125.0"),sQuery(id+"F0.wireOp",EDGE,"E16.125.1"),sQuery(id+"F0.wireOp",EDGE,"E16.125.2"),sQuery(id+"F0.wireOp",EDGE,"E16.125.3"),sQuery(id+"F0.wireOp",EDGE,"E16.125.4"),sQuery(id+"F0.wireOp",EDGE,"E16.126.0"),sQuery(id+"F0.wireOp",EDGE,"E16.126.1"),sQuery(id+"F0.wireOp",EDGE,"E16.126.2"),sQuery(id+"F0.wireOp",EDGE,"E16.126.3"),sQuery(id+"F0.wireOp",EDGE,"E16.126.4"),sQuery(id+"F0.wireOp",EDGE,"E16.127.0"),sQuery(id+"F0.wireOp",EDGE,"E16.127.1"),sQuery(id+"F0.wireOp",EDGE,"E16.127.2"),sQuery(id+"F0.wireOp",EDGE,"E16.127.3"),sQuery(id+"F0.wireOp",EDGE,"E16.127.4"),sQuery(id+"F0.wireOp",EDGE,"E16.128.0"),sQuery(id+"F0.wireOp",EDGE,"E16.128.1"),sQuery(id+"F0.wireOp",EDGE,"E16.128.2"),sQuery(id+"F0.wireOp",EDGE,"E16.128.3"),sQuery(id+"F0.wireOp",EDGE,"E16.128.4"),sQuery(id+"F0.wireOp",EDGE,"E16.129.0"),sQuery(id+"F0.wireOp",EDGE,"E16.129.1"),sQuery(id+"F0.wireOp",EDGE,"E16.129.2"),sQuery(id+"F0.wireOp",EDGE,"E16.129.3"),sQuery(id+"F0.wireOp",EDGE,"E16.129.4"),sQuery(id+"F0.wireOp",EDGE,"E16.130.0"),sQuery(id+"F0.wireOp",EDGE,"E16.130.1"),sQuery(id+"F0.wireOp",EDGE,"E16.130.2"),sQuery(id+"F0.wireOp",EDGE,"E16.130.3"),sQuery(id+"F0.wireOp",EDGE,"E16.130.4"),sQuery(id+"F0.wireOp",EDGE,"E16.131.0"),sQuery(id+"F0.wireOp",EDGE,"E16.131.1"),sQuery(id+"F0.wireOp",EDGE,"E16.131.2"),sQuery(id+"F0.wireOp",EDGE,"E16.131.3"),sQuery(id+"F0.wireOp",EDGE,"E16.131.4"),sQuery(id+"F0.wireOp",EDGE,"E16.132.0"),sQuery(id+"F0.wireOp",EDGE,"E16.132.1"),sQuery(id+"F0.wireOp",EDGE,"E16.132.2"),sQuery(id+"F0.wireOp",EDGE,"E16.132.3"),sQuery(id+"F0.wireOp",EDGE,"E16.132.4"),sQuery(id+"F0.wireOp",EDGE,"E16.133.0"),sQuery(id+"F0.wireOp",EDGE,"E16.133.1"),sQuery(id+"F0.wireOp",EDGE,"E16.133.2"),sQuery(id+"F0.wireOp",EDGE,"E16.133.3"),sQuery(id+"F0.wireOp",EDGE,"E16.133.4"),sQuery(id+"F0.wireOp",EDGE,"E16.134.0"),sQuery(id+"F0.wireOp",EDGE,"E16.134.1"),sQuery(id+"F0.wireOp",EDGE,"E16.134.2"),sQuery(id+"F0.wireOp",EDGE,"E16.134.3"),sQuery(id+"F0.wireOp",EDGE,"E16.134.4"),sQuery(id+"F0.wireOp",EDGE,"E16.135.0"),sQuery(id+"F0.wireOp",EDGE,"E16.135.1"),sQuery(id+"F0.wireOp",EDGE,"E16.135.2"),sQuery(id+"F0.wireOp",EDGE,"E16.135.3"),sQuery(id+"F0.wireOp",EDGE,"E16.135.4"),sQuery(id+"F0.wireOp",EDGE,"E16.136.0"),sQuery(id+"F0.wireOp",EDGE,"E16.136.1"),sQuery(id+"F0.wireOp",EDGE,"E16.136.2"),sQuery(id+"F0.wireOp",EDGE,"E16.136.3"),sQuery(id+"F0.wireOp",EDGE,"E16.136.4"),sQuery(id+"F0.wireOp",EDGE,"E16.137.0"),sQuery(id+"F0.wireOp",EDGE,"E16.137.1"),sQuery(id+"F0.wireOp",EDGE,"E16.137.2"),sQuery(id+"F0.wireOp",EDGE,"E16.137.3"),sQuery(id+"F0.wireOp",EDGE,"E16.137.4"),sQuery(id+"F0.wireOp",EDGE,"E16.138.0"),sQuery(id+"F0.wireOp",EDGE,"E16.138.1"),sQuery(id+"F0.wireOp",EDGE,"E16.138.2"),sQuery(id+"F0.wireOp",EDGE,"E16.138.3"),sQuery(id+"F0.wireOp",EDGE,"E16.138.4"),sQuery(id+"F0.wireOp",EDGE,"E16.139.0"),sQuery(id+"F0.wireOp",EDGE,"E16.139.1"),sQuery(id+"F0.wireOp",EDGE,"E16.139.2"),sQuery(id+"F0.wireOp",EDGE,"E16.139.3"),sQuery(id+"F0.wireOp",EDGE,"E16.139.4"),sQuery(id+"F0.wireOp",EDGE,"E16.140.0"),sQuery(id+"F0.wireOp",EDGE,"E16.140.1"),sQuery(id+"F0.wireOp",EDGE,"E16.140.2"),sQuery(id+"F0.wireOp",EDGE,"E16.140.3"),sQuery(id+"F0.wireOp",EDGE,"E16.140.4"),sQuery(id+"F0.wireOp",EDGE,"E16.141.0"),sQuery(id+"F0.wireOp",EDGE,"E16.141.1"),sQuery(id+"F0.wireOp",EDGE,"E16.141.2"),sQuery(id+"F0.wireOp",EDGE,"E16.141.3"),sQuery(id+"F0.wireOp",EDGE,"E16.141.4"),sQuery(id+"F0.wireOp",EDGE,"E16.142.0"),sQuery(id+"F0.wireOp",EDGE,"E16.142.1"),sQuery(id+"F0.wireOp",EDGE,"E16.142.2"),sQuery(id+"F0.wireOp",EDGE,"E16.142.3"),sQuery(id+"F0.wireOp",EDGE,"E16.142.4"),sQuery(id+"F0.wireOp",EDGE,"E16.143.0"),sQuery(id+"F0.wireOp",EDGE,"E16.143.1"),sQuery(id+"F0.wireOp",EDGE,"E16.143.2"),sQuery(id+"F0.wireOp",EDGE,"E16.143.3"),sQuery(id+"F0.wireOp",EDGE,"E16.143.4"),sQuery(id+"F0.wireOp",EDGE,"E16.144.0"),sQuery(id+"F0.wireOp",EDGE,"E16.144.1"),sQuery(id+"F0.wireOp",EDGE,"E16.144.2"),sQuery(id+"F0.wireOp",EDGE,"E16.144.3"),sQuery(id+"F0.wireOp",EDGE,"E16.144.4"),sQuery(id+"F0.wireOp",EDGE,"E16.145.0"),sQuery(id+"F0.wireOp",EDGE,"E16.145.1"),sQuery(id+"F0.wireOp",EDGE,"E16.145.2"),sQuery(id+"F0.wireOp",EDGE,"E16.145.3"),sQuery(id+"F0.wireOp",EDGE,"E16.145.4"),sQuery(id+"F0.wireOp",EDGE,"E16.146.0"),sQuery(id+"F0.wireOp",EDGE,"E16.146.1"),sQuery(id+"F0.wireOp",EDGE,"E16.146.2"),sQuery(id+"F0.wireOp",EDGE,"E16.146.3"),sQuery(id+"F0.wireOp",EDGE,"E16.146.4"),sQuery(id+"F0.wireOp",EDGE,"E16.147.0"),sQuery(id+"F0.wireOp",EDGE,"E16.147.1"),sQuery(id+"F0.wireOp",EDGE,"E16.147.2"),sQuery(id+"F0.wireOp",EDGE,"E16.147.3"),sQuery(id+"F0.wireOp",EDGE,"E16.147.4"),sQuery(id+"F0.wireOp",EDGE,"E16.148.0"),sQuery(id+"F0.wireOp",EDGE,"E16.148.1"),sQuery(id+"F0.wireOp",EDGE,"E16.148.2"),sQuery(id+"F0.wireOp",EDGE,"E16.148.3"),sQuery(id+"F0.wireOp",EDGE,"E16.148.4"),sQuery(id+"F0.wireOp",EDGE,"E16.149.0"),sQuery(id+"F0.wireOp",EDGE,"E16.149.1"),sQuery(id+"F0.wireOp",EDGE,"E16.149.2"),sQuery(id+"F0.wireOp",EDGE,"E16.149.3"),sQuery(id+"F0.wireOp",EDGE,"E16.149.4"),sQuery(id+"F0.wireOp",EDGE,"E16.150.0"),sQuery(id+"F0.wireOp",EDGE,"E16.150.1"),sQuery(id+"F0.wireOp",EDGE,"E16.150.2"),sQuery(id+"F0.wireOp",EDGE,"E16.150.3"),sQuery(id+"F0.wireOp",EDGE,"E16.150.4"),sQuery(id+"F0.wireOp",EDGE,"E16.151.0"),sQuery(id+"F0.wireOp",EDGE,"E16.151.1"),sQuery(id+"F0.wireOp",EDGE,"E16.151.2"),sQuery(id+"F0.wireOp",EDGE,"E16.151.3"),sQuery(id+"F0.wireOp",EDGE,"E16.151.4"),sQuery(id+"F0.wireOp",EDGE,"E16.152.0"),sQuery(id+"F0.wireOp",EDGE,"E16.152.1"),sQuery(id+"F0.wireOp",EDGE,"E16.152.2"),sQuery(id+"F0.wireOp",EDGE,"E16.152.3"),sQuery(id+"F0.wireOp",EDGE,"E16.152.4"),sQuery(id+"F0.wireOp",EDGE,"E16.153.0"),sQuery(id+"F0.wireOp",EDGE,"E16.153.1"),sQuery(id+"F0.wireOp",EDGE,"E16.153.2"),sQuery(id+"F0.wireOp",EDGE,"E16.153.3"),sQuery(id+"F0.wireOp",EDGE,"E16.153.4"),sQuery(id+"F0.wireOp",EDGE,"E16.154.0"),sQuery(id+"F0.wireOp",EDGE,"E16.154.1"),sQuery(id+"F0.wireOp",EDGE,"E16.154.2"),sQuery(id+"F0.wireOp",EDGE,"E16.154.3"),sQuery(id+"F0.wireOp",EDGE,"E16.154.4"),sQuery(id+"F0.wireOp",EDGE,"E16.155.0"),sQuery(id+"F0.wireOp",EDGE,"E16.155.1"),sQuery(id+"F0.wireOp",EDGE,"E16.155.2"),sQuery(id+"F0.wireOp",EDGE,"E16.155.3"),sQuery(id+"F0.wireOp",EDGE,"E16.155.4"),sQuery(id+"F0.wireOp",EDGE,"E16.156.0"),sQuery(id+"F0.wireOp",EDGE,"E16.156.1"),sQuery(id+"F0.wireOp",EDGE,"E16.156.2"),sQuery(id+"F0.wireOp",EDGE,"E16.156.3"),sQuery(id+"F0.wireOp",EDGE,"E16.156.4"),sQuery(id+"F0.wireOp",EDGE,"E16.157.0"),sQuery(id+"F0.wireOp",EDGE,"E16.157.1"),sQuery(id+"F0.wireOp",EDGE,"E16.157.2"),sQuery(id+"F0.wireOp",EDGE,"E16.157.3"),sQuery(id+"F0.wireOp",EDGE,"E16.157.4"),sQuery(id+"F0.wireOp",EDGE,"E16.158.0"),sQuery(id+"F0.wireOp",EDGE,"E16.158.1"),sQuery(id+"F0.wireOp",EDGE,"E16.158.2"),sQuery(id+"F0.wireOp",EDGE,"E16.158.3"),sQuery(id+"F0.wireOp",EDGE,"E16.158.4"),sQuery(id+"F0.wireOp",EDGE,"E16.159.0"),sQuery(id+"F0.wireOp",EDGE,"E16.159.1"),sQuery(id+"F0.wireOp",EDGE,"E16.159.2"),sQuery(id+"F0.wireOp",EDGE,"E16.159.3"),sQuery(id+"F0.wireOp",EDGE,"E16.159.4"),sQuery(id+"F0.wireOp",EDGE,"E16.160.0"),sQuery(id+"F0.wireOp",EDGE,"E16.160.1"),sQuery(id+"F0.wireOp",EDGE,"E16.160.2"),sQuery(id+"F0.wireOp",EDGE,"E16.160.3"),sQuery(id+"F0.wireOp",EDGE,"E16.160.4"),sQuery(id+"F0.wireOp",EDGE,"E16.161.0"),sQuery(id+"F0.wireOp",EDGE,"E16.161.1"),sQuery(id+"F0.wireOp",EDGE,"E16.161.2"),sQuery(id+"F0.wireOp",EDGE,"E16.161.3"),sQuery(id+"F0.wireOp",EDGE,"E16.161.4"),sQuery(id+"F0.wireOp",EDGE,"E16.162.0"),sQuery(id+"F0.wireOp",EDGE,"E16.162.1"),sQuery(id+"F0.wireOp",EDGE,"E16.162.2"),sQuery(id+"F0.wireOp",EDGE,"E16.162.3"),sQuery(id+"F0.wireOp",EDGE,"E16.162.4"),sQuery(id+"F0.wireOp",EDGE,"E16.163.0"),sQuery(id+"F0.wireOp",EDGE,"E16.163.1"),sQuery(id+"F0.wireOp",EDGE,"E16.163.2"),sQuery(id+"F0.wireOp",EDGE,"E16.163.3"),sQuery(id+"F0.wireOp",EDGE,"E16.163.4"),sQuery(id+"F0.wireOp",EDGE,"E16.164.0"),sQuery(id+"F0.wireOp",EDGE,"E16.164.1"),sQuery(id+"F0.wireOp",EDGE,"E16.164.2"),sQuery(id+"F0.wireOp",EDGE,"E16.164.3"),sQuery(id+"F0.wireOp",EDGE,"E16.164.4"),sQuery(id+"F0.wireOp",EDGE,"E16.165.0"),sQuery(id+"F0.wireOp",EDGE,"E16.165.1"),sQuery(id+"F0.wireOp",EDGE,"E16.165.2"),sQuery(id+"F0.wireOp",EDGE,"E16.165.3"),sQuery(id+"F0.wireOp",EDGE,"E16.165.4"),sQuery(id+"F0.wireOp",EDGE,"E16.166.0"),sQuery(id+"F0.wireOp",EDGE,"E16.166.1"),sQuery(id+"F0.wireOp",EDGE,"E16.166.2"),sQuery(id+"F0.wireOp",EDGE,"E16.166.3"),sQuery(id+"F0.wireOp",EDGE,"E16.166.4"),sQuery(id+"F0.wireOp",EDGE,"E16.167.0"),sQuery(id+"F0.wireOp",EDGE,"E16.167.1"),sQuery(id+"F0.wireOp",EDGE,"E16.167.2"),sQuery(id+"F0.wireOp",EDGE,"E16.167.3"),sQuery(id+"F0.wireOp",EDGE,"E16.167.4"),sQuery(id+"F0.wireOp",EDGE,"E16.168.0"),sQuery(id+"F0.wireOp",EDGE,"E16.168.1"),sQuery(id+"F0.wireOp",EDGE,"E16.168.2"),sQuery(id+"F0.wireOp",EDGE,"E16.168.3"),sQuery(id+"F0.wireOp",EDGE,"E16.168.4"),sQuery(id+"F0.wireOp",EDGE,"E16.169.0"),sQuery(id+"F0.wireOp",EDGE,"E16.169.1"),sQuery(id+"F0.wireOp",EDGE,"E16.169.2"),sQuery(id+"F0.wireOp",EDGE,"E16.169.3"),sQuery(id+"F0.wireOp",EDGE,"E16.169.4"),sQuery(id+"F0.wireOp",EDGE,"E16.170.0"),sQuery(id+"F0.wireOp",EDGE,"E16.170.1"),sQuery(id+"F0.wireOp",EDGE,"E16.170.2"),sQuery(id+"F0.wireOp",EDGE,"E16.170.3"),sQuery(id+"F0.wireOp",EDGE,"E16.170.4"),sQuery(id+"F0.wireOp",EDGE,"E16.171.0"),sQuery(id+"F0.wireOp",EDGE,"E16.171.1"),sQuery(id+"F0.wireOp",EDGE,"E16.171.2"),sQuery(id+"F0.wireOp",EDGE,"E16.171.3"),sQuery(id+"F0.wireOp",EDGE,"E16.171.4"),sQuery(id+"F0.wireOp",EDGE,"E16.172.0"),sQuery(id+"F0.wireOp",EDGE,"E16.172.1"),sQuery(id+"F0.wireOp",EDGE,"E16.172.2"),sQuery(id+"F0.wireOp",EDGE,"E16.172.3"),sQuery(id+"F0.wireOp",EDGE,"E16.172.4"),sQuery(id+"F0.wireOp",EDGE,"E16.173.0"),sQuery(id+"F0.wireOp",EDGE,"E16.173.1"),sQuery(id+"F0.wireOp",EDGE,"E16.173.2"),sQuery(id+"F0.wireOp",EDGE,"E16.173.3"),sQuery(id+"F0.wireOp",EDGE,"E16.173.4"),sQuery(id+"F0.wireOp",EDGE,"E16.174.0"),sQuery(id+"F0.wireOp",EDGE,"E16.174.1"),sQuery(id+"F0.wireOp",EDGE,"E16.174.2"),sQuery(id+"F0.wireOp",EDGE,"E16.174.3"),sQuery(id+"F0.wireOp",EDGE,"E16.174.4"),sQuery(id+"F0.wireOp",EDGE,"E16.175.0"),sQuery(id+"F0.wireOp",EDGE,"E16.175.1"),sQuery(id+"F0.wireOp",EDGE,"E16.175.2"),sQuery(id+"F0.wireOp",EDGE,"E16.175.3"),sQuery(id+"F0.wireOp",EDGE,"E16.175.4"),sQuery(id+"F0.wireOp",EDGE,"E16.176.0"),sQuery(id+"F0.wireOp",EDGE,"E16.176.1"),sQuery(id+"F0.wireOp",EDGE,"E16.176.2"),sQuery(id+"F0.wireOp",EDGE,"E16.176.3"),sQuery(id+"F0.wireOp",EDGE,"E16.176.4"),sQuery(id+"F0.wireOp",EDGE,"E16.177.0"),sQuery(id+"F0.wireOp",EDGE,"E16.177.1"),sQuery(id+"F0.wireOp",EDGE,"E16.177.2"),sQuery(id+"F0.wireOp",EDGE,"E16.177.3"),sQuery(id+"F0.wireOp",EDGE,"E16.177.4"),sQuery(id+"F0.wireOp",EDGE,"E16.178.0"),sQuery(id+"F0.wireOp",EDGE,"E16.178.1"),sQuery(id+"F0.wireOp",EDGE,"E16.178.2"),sQuery(id+"F0.wireOp",EDGE,"E16.178.3"),sQuery(id+"F0.wireOp",EDGE,"E16.178.4"),sQuery(id+"F0.wireOp",EDGE,"E16.179.0"),sQuery(id+"F0.wireOp",EDGE,"E16.179.1"),sQuery(id+"F0.wireOp",EDGE,"E16.179.2"),sQuery(id+"F0.wireOp",EDGE,"E16.179.3"),sQuery(id+"F0.wireOp",EDGE,"E16.179.4"),sQuery(id+"F0.wireOp",EDGE,"E16.180.0"),sQuery(id+"F0.wireOp",EDGE,"E16.180.1"),sQuery(id+"F0.wireOp",EDGE,"E16.180.2"),sQuery(id+"F0.wireOp",EDGE,"E16.180.3"),sQuery(id+"F0.wireOp",EDGE,"E16.180.4"),sQuery(id+"F0.wireOp",EDGE,"E16.181.0"),sQuery(id+"F0.wireOp",EDGE,"E16.181.1"),sQuery(id+"F0.wireOp",EDGE,"E16.181.2"),sQuery(id+"F0.wireOp",EDGE,"E16.181.3"),sQuery(id+"F0.wireOp",EDGE,"E16.181.4"),sQuery(id+"F0.wireOp",EDGE,"E16.182.0"),sQuery(id+"F0.wireOp",EDGE,"E16.182.1"),sQuery(id+"F0.wireOp",EDGE,"E16.182.2"),sQuery(id+"F0.wireOp",EDGE,"E16.182.3"),sQuery(id+"F0.wireOp",EDGE,"E16.182.4"),sQuery(id+"F0.wireOp",EDGE,"E16.183.0"),sQuery(id+"F0.wireOp",EDGE,"E16.183.1"),sQuery(id+"F0.wireOp",EDGE,"E16.183.2"),sQuery(id+"F0.wireOp",EDGE,"E16.183.3"),sQuery(id+"F0.wireOp",EDGE,"E16.183.4"),sQuery(id+"F0.wireOp",EDGE,"E16.184.0"),sQuery(id+"F0.wireOp",EDGE,"E16.184.1"),sQuery(id+"F0.wireOp",EDGE,"E16.184.2"),sQuery(id+"F0.wireOp",EDGE,"E16.184.3"),sQuery(id+"F0.wireOp",EDGE,"E16.184.4"),sQuery(id+"F0.wireOp",EDGE,"E16.185.0"),sQuery(id+"F0.wireOp",EDGE,"E16.185.1"),sQuery(id+"F0.wireOp",EDGE,"E16.185.2"),sQuery(id+"F0.wireOp",EDGE,"E16.185.3"),sQuery(id+"F0.wireOp",EDGE,"E16.185.4"),sQuery(id+"F0.wireOp",EDGE,"E16.186.0"),sQuery(id+"F0.wireOp",EDGE,"E16.186.1"),sQuery(id+"F0.wireOp",EDGE,"E16.186.2"),sQuery(id+"F0.wireOp",EDGE,"E16.186.3"),sQuery(id+"F0.wireOp",EDGE,"E16.186.4"),sQuery(id+"F0.wireOp",EDGE,"E16.187.0"),sQuery(id+"F0.wireOp",EDGE,"E16.187.1"),sQuery(id+"F0.wireOp",EDGE,"E16.187.2"),sQuery(id+"F0.wireOp",EDGE,"E16.187.3"),sQuery(id+"F0.wireOp",EDGE,"E16.187.4"),sQuery(id+"F0.wireOp",EDGE,"E16.188.0"),sQuery(id+"F0.wireOp",EDGE,"E16.188.1"),sQuery(id+"F0.wireOp",EDGE,"E16.188.2"),sQuery(id+"F0.wireOp",EDGE,"E16.188.3"),sQuery(id+"F0.wireOp",EDGE,"E16.188.4"),sQuery(id+"F0.wireOp",EDGE,"E16.189.0"),sQuery(id+"F0.wireOp",EDGE,"E16.189.1"),sQuery(id+"F0.wireOp",EDGE,"E16.189.2"),sQuery(id+"F0.wireOp",EDGE,"E16.189.3"),sQuery(id+"F0.wireOp",EDGE,"E16.189.4"),sQuery(id+"F0.wireOp",EDGE,"E16.190.0"),sQuery(id+"F0.wireOp",EDGE,"E16.190.1"),sQuery(id+"F0.wireOp",EDGE,"E16.190.2"),sQuery(id+"F0.wireOp",EDGE,"E16.190.3"),sQuery(id+"F0.wireOp",EDGE,"E16.190.4"),sQuery(id+"F0.wireOp",EDGE,"E16.191.0"),sQuery(id+"F0.wireOp",EDGE,"E16.191.1"),sQuery(id+"F0.wireOp",EDGE,"E16.191.2"),sQuery(id+"F0.wireOp",EDGE,"E16.191.3"),sQuery(id+"F0.wireOp",EDGE,"E16.191.4")])],"isStart":true});
            var sketch = newSketch(context, id + "F2", { "sketchPlane" : qUnion([Q0])});
            skCircle(sketch, "E17", {"center": v(0, 0) * mm, "radius": 95 * mm, "construction": true});
            skLineSegment(sketch, "E18", {"start": v(0, 0) * mm, "end": v(113.24, 0) * mm, "construction": true});
            skPoint(sketch, "E19", {"position": v(95, 0) * mm});
            skPoint(sketch, "E20.1.0", {"position": v(82.27, 47.5) * mm});
            skPoint(sketch, "E20.2.0", {"position": v(47.5, 82.27) * mm});
            skPoint(sketch, "E20.3.0", {"position": v(0, 95) * mm});
            skPoint(sketch, "E20.4.0", {"position": v(-47.5, 82.27) * mm});
            skPoint(sketch, "E20.5.0", {"position": v(-82.27, 47.5) * mm});
            skPoint(sketch, "E20.6.0", {"position": v(-95, 0) * mm});
            skPoint(sketch, "E20.7.0", {"position": v(-82.27, -47.5) * mm});
            skPoint(sketch, "E20.8.0", {"position": v(-47.5, -82.27) * mm});
            skPoint(sketch, "E20.9.0", {"position": v(0, -95) * mm});
            skPoint(sketch, "E20.10.0", {"position": v(47.5, -82.27) * mm});
            skPoint(sketch, "E20.11.0", {"position": v(82.27, -47.5) * mm});
            skSolve(sketch);
        }
        {
            var Q0;
            Q0=makeQuery(id+"F1.opExtrude","CAP_FACE",FACE,{"disambiguationData":[OSD([sQuery(id+"F0.wireOp",EDGE,"E0"),sQuery(id+"F0.wireOp",EDGE,"E4"),sQuery(id+"F0.wireOp",EDGE,"E5"),sQuery(id+"F0.wireOp",EDGE,"E6.filletArc"),sQuery(id+"F0.wireOp",EDGE,"E7.MirrorCS"),sQuery(id+"F0.wireOp",EDGE,"E8.MirrorCS"),sQuery(id+"F0.wireOp",EDGE,"E15"),sQuery(id+"F0.wireOp",EDGE,"E16.1.0"),sQuery(id+"F0.wireOp",EDGE,"E16.1.1"),sQuery(id+"F0.wireOp",EDGE,"E16.1.2"),sQuery(id+"F0.wireOp",EDGE,"E16.1.3"),sQuery(id+"F0.wireOp",EDGE,"E16.1.4"),sQuery(id+"F0.wireOp",EDGE,"E16.2.0"),sQuery(id+"F0.wireOp",EDGE,"E16.2.1"),sQuery(id+"F0.wireOp",EDGE,"E16.2.2"),sQuery(id+"F0.wireOp",EDGE,"E16.2.3"),sQuery(id+"F0.wireOp",EDGE,"E16.2.4"),sQuery(id+"F0.wireOp",EDGE,"E16.3.0"),sQuery(id+"F0.wireOp",EDGE,"E16.3.1"),sQuery(id+"F0.wireOp",EDGE,"E16.3.2"),sQuery(id+"F0.wireOp",EDGE,"E16.3.3"),sQuery(id+"F0.wireOp",EDGE,"E16.3.4"),sQuery(id+"F0.wireOp",EDGE,"E16.4.0"),sQuery(id+"F0.wireOp",EDGE,"E16.4.1"),sQuery(id+"F0.wireOp",EDGE,"E16.4.2"),sQuery(id+"F0.wireOp",EDGE,"E16.4.3"),sQuery(id+"F0.wireOp",EDGE,"E16.4.4"),sQuery(id+"F0.wireOp",EDGE,"E16.5.0"),sQuery(id+"F0.wireOp",EDGE,"E16.5.1"),sQuery(id+"F0.wireOp",EDGE,"E16.5.2"),sQuery(id+"F0.wireOp",EDGE,"E16.5.3"),sQuery(id+"F0.wireOp",EDGE,"E16.5.4"),sQuery(id+"F0.wireOp",EDGE,"E16.6.0"),sQuery(id+"F0.wireOp",EDGE,"E16.6.1"),sQuery(id+"F0.wireOp",EDGE,"E16.6.2"),sQuery(id+"F0.wireOp",EDGE,"E16.6.3"),sQuery(id+"F0.wireOp",EDGE,"E16.6.4"),sQuery(id+"F0.wireOp",EDGE,"E16.7.0"),sQuery(id+"F0.wireOp",EDGE,"E16.7.1"),sQuery(id+"F0.wireOp",EDGE,"E16.7.2"),sQuery(id+"F0.wireOp",EDGE,"E16.7.3"),sQuery(id+"F0.wireOp",EDGE,"E16.7.4"),sQuery(id+"F0.wireOp",EDGE,"E16.8.0"),sQuery(id+"F0.wireOp",EDGE,"E16.8.1"),sQuery(id+"F0.wireOp",EDGE,"E16.8.2"),sQuery(id+"F0.wireOp",EDGE,"E16.8.3"),sQuery(id+"F0.wireOp",EDGE,"E16.8.4"),sQuery(id+"F0.wireOp",EDGE,"E16.9.0"),sQuery(id+"F0.wireOp",EDGE,"E16.9.1"),sQuery(id+"F0.wireOp",EDGE,"E16.9.2"),sQuery(id+"F0.wireOp",EDGE,"E16.9.3"),sQuery(id+"F0.wireOp",EDGE,"E16.9.4"),sQuery(id+"F0.wireOp",EDGE,"E16.10.0"),sQuery(id+"F0.wireOp",EDGE,"E16.10.1"),sQuery(id+"F0.wireOp",EDGE,"E16.10.2"),sQuery(id+"F0.wireOp",EDGE,"E16.10.3"),sQuery(id+"F0.wireOp",EDGE,"E16.10.4"),sQuery(id+"F0.wireOp",EDGE,"E16.11.0"),sQuery(id+"F0.wireOp",EDGE,"E16.11.1"),sQuery(id+"F0.wireOp",EDGE,"E16.11.2"),sQuery(id+"F0.wireOp",EDGE,"E16.11.3"),sQuery(id+"F0.wireOp",EDGE,"E16.11.4"),sQuery(id+"F0.wireOp",EDGE,"E16.12.0"),sQuery(id+"F0.wireOp",EDGE,"E16.12.1"),sQuery(id+"F0.wireOp",EDGE,"E16.12.2"),sQuery(id+"F0.wireOp",EDGE,"E16.12.3"),sQuery(id+"F0.wireOp",EDGE,"E16.12.4"),sQuery(id+"F0.wireOp",EDGE,"E16.13.0"),sQuery(id+"F0.wireOp",EDGE,"E16.13.1"),sQuery(id+"F0.wireOp",EDGE,"E16.13.2"),sQuery(id+"F0.wireOp",EDGE,"E16.13.3"),sQuery(id+"F0.wireOp",EDGE,"E16.13.4"),sQuery(id+"F0.wireOp",EDGE,"E16.14.0"),sQuery(id+"F0.wireOp",EDGE,"E16.14.1"),sQuery(id+"F0.wireOp",EDGE,"E16.14.2"),sQuery(id+"F0.wireOp",EDGE,"E16.14.3"),sQuery(id+"F0.wireOp",EDGE,"E16.14.4"),sQuery(id+"F0.wireOp",EDGE,"E16.15.0"),sQuery(id+"F0.wireOp",EDGE,"E16.15.1"),sQuery(id+"F0.wireOp",EDGE,"E16.15.2"),sQuery(id+"F0.wireOp",EDGE,"E16.15.3"),sQuery(id+"F0.wireOp",EDGE,"E16.15.4"),sQuery(id+"F0.wireOp",EDGE,"E16.16.0"),sQuery(id+"F0.wireOp",EDGE,"E16.16.1"),sQuery(id+"F0.wireOp",EDGE,"E16.16.2"),sQuery(id+"F0.wireOp",EDGE,"E16.16.3"),sQuery(id+"F0.wireOp",EDGE,"E16.16.4"),sQuery(id+"F0.wireOp",EDGE,"E16.17.0"),sQuery(id+"F0.wireOp",EDGE,"E16.17.1"),sQuery(id+"F0.wireOp",EDGE,"E16.17.2"),sQuery(id+"F0.wireOp",EDGE,"E16.17.3"),sQuery(id+"F0.wireOp",EDGE,"E16.17.4"),sQuery(id+"F0.wireOp",EDGE,"E16.18.0"),sQuery(id+"F0.wireOp",EDGE,"E16.18.1"),sQuery(id+"F0.wireOp",EDGE,"E16.18.2"),sQuery(id+"F0.wireOp",EDGE,"E16.18.3"),sQuery(id+"F0.wireOp",EDGE,"E16.18.4"),sQuery(id+"F0.wireOp",EDGE,"E16.19.0"),sQuery(id+"F0.wireOp",EDGE,"E16.19.1"),sQuery(id+"F0.wireOp",EDGE,"E16.19.2"),sQuery(id+"F0.wireOp",EDGE,"E16.19.3"),sQuery(id+"F0.wireOp",EDGE,"E16.19.4"),sQuery(id+"F0.wireOp",EDGE,"E16.20.0"),sQuery(id+"F0.wireOp",EDGE,"E16.20.1"),sQuery(id+"F0.wireOp",EDGE,"E16.20.2"),sQuery(id+"F0.wireOp",EDGE,"E16.20.3"),sQuery(id+"F0.wireOp",EDGE,"E16.20.4"),sQuery(id+"F0.wireOp",EDGE,"E16.21.0"),sQuery(id+"F0.wireOp",EDGE,"E16.21.1"),sQuery(id+"F0.wireOp",EDGE,"E16.21.2"),sQuery(id+"F0.wireOp",EDGE,"E16.21.3"),sQuery(id+"F0.wireOp",EDGE,"E16.21.4"),sQuery(id+"F0.wireOp",EDGE,"E16.22.0"),sQuery(id+"F0.wireOp",EDGE,"E16.22.1"),sQuery(id+"F0.wireOp",EDGE,"E16.22.2"),sQuery(id+"F0.wireOp",EDGE,"E16.22.3"),sQuery(id+"F0.wireOp",EDGE,"E16.22.4"),sQuery(id+"F0.wireOp",EDGE,"E16.23.0"),sQuery(id+"F0.wireOp",EDGE,"E16.23.1"),sQuery(id+"F0.wireOp",EDGE,"E16.23.2"),sQuery(id+"F0.wireOp",EDGE,"E16.23.3"),sQuery(id+"F0.wireOp",EDGE,"E16.23.4"),sQuery(id+"F0.wireOp",EDGE,"E16.24.0"),sQuery(id+"F0.wireOp",EDGE,"E16.24.1"),sQuery(id+"F0.wireOp",EDGE,"E16.24.2"),sQuery(id+"F0.wireOp",EDGE,"E16.24.3"),sQuery(id+"F0.wireOp",EDGE,"E16.24.4"),sQuery(id+"F0.wireOp",EDGE,"E16.25.0"),sQuery(id+"F0.wireOp",EDGE,"E16.25.1"),sQuery(id+"F0.wireOp",EDGE,"E16.25.2"),sQuery(id+"F0.wireOp",EDGE,"E16.25.3"),sQuery(id+"F0.wireOp",EDGE,"E16.25.4"),sQuery(id+"F0.wireOp",EDGE,"E16.26.0"),sQuery(id+"F0.wireOp",EDGE,"E16.26.1"),sQuery(id+"F0.wireOp",EDGE,"E16.26.2"),sQuery(id+"F0.wireOp",EDGE,"E16.26.3"),sQuery(id+"F0.wireOp",EDGE,"E16.26.4"),sQuery(id+"F0.wireOp",EDGE,"E16.27.0"),sQuery(id+"F0.wireOp",EDGE,"E16.27.1"),sQuery(id+"F0.wireOp",EDGE,"E16.27.2"),sQuery(id+"F0.wireOp",EDGE,"E16.27.3"),sQuery(id+"F0.wireOp",EDGE,"E16.27.4"),sQuery(id+"F0.wireOp",EDGE,"E16.28.0"),sQuery(id+"F0.wireOp",EDGE,"E16.28.1"),sQuery(id+"F0.wireOp",EDGE,"E16.28.2"),sQuery(id+"F0.wireOp",EDGE,"E16.28.3"),sQuery(id+"F0.wireOp",EDGE,"E16.28.4"),sQuery(id+"F0.wireOp",EDGE,"E16.29.0"),sQuery(id+"F0.wireOp",EDGE,"E16.29.1"),sQuery(id+"F0.wireOp",EDGE,"E16.29.2"),sQuery(id+"F0.wireOp",EDGE,"E16.29.3"),sQuery(id+"F0.wireOp",EDGE,"E16.29.4"),sQuery(id+"F0.wireOp",EDGE,"E16.30.0"),sQuery(id+"F0.wireOp",EDGE,"E16.30.1"),sQuery(id+"F0.wireOp",EDGE,"E16.30.2"),sQuery(id+"F0.wireOp",EDGE,"E16.30.3"),sQuery(id+"F0.wireOp",EDGE,"E16.30.4"),sQuery(id+"F0.wireOp",EDGE,"E16.31.0"),sQuery(id+"F0.wireOp",EDGE,"E16.31.1"),sQuery(id+"F0.wireOp",EDGE,"E16.31.2"),sQuery(id+"F0.wireOp",EDGE,"E16.31.3"),sQuery(id+"F0.wireOp",EDGE,"E16.31.4"),sQuery(id+"F0.wireOp",EDGE,"E16.32.0"),sQuery(id+"F0.wireOp",EDGE,"E16.32.1"),sQuery(id+"F0.wireOp",EDGE,"E16.32.2"),sQuery(id+"F0.wireOp",EDGE,"E16.32.3"),sQuery(id+"F0.wireOp",EDGE,"E16.32.4"),sQuery(id+"F0.wireOp",EDGE,"E16.33.0"),sQuery(id+"F0.wireOp",EDGE,"E16.33.1"),sQuery(id+"F0.wireOp",EDGE,"E16.33.2"),sQuery(id+"F0.wireOp",EDGE,"E16.33.3"),sQuery(id+"F0.wireOp",EDGE,"E16.33.4"),sQuery(id+"F0.wireOp",EDGE,"E16.34.0"),sQuery(id+"F0.wireOp",EDGE,"E16.34.1"),sQuery(id+"F0.wireOp",EDGE,"E16.34.2"),sQuery(id+"F0.wireOp",EDGE,"E16.34.3"),sQuery(id+"F0.wireOp",EDGE,"E16.34.4"),sQuery(id+"F0.wireOp",EDGE,"E16.35.0"),sQuery(id+"F0.wireOp",EDGE,"E16.35.1"),sQuery(id+"F0.wireOp",EDGE,"E16.35.2"),sQuery(id+"F0.wireOp",EDGE,"E16.35.3"),sQuery(id+"F0.wireOp",EDGE,"E16.35.4"),sQuery(id+"F0.wireOp",EDGE,"E16.36.0"),sQuery(id+"F0.wireOp",EDGE,"E16.36.1"),sQuery(id+"F0.wireOp",EDGE,"E16.36.2"),sQuery(id+"F0.wireOp",EDGE,"E16.36.3"),sQuery(id+"F0.wireOp",EDGE,"E16.36.4"),sQuery(id+"F0.wireOp",EDGE,"E16.37.0"),sQuery(id+"F0.wireOp",EDGE,"E16.37.1"),sQuery(id+"F0.wireOp",EDGE,"E16.37.2"),sQuery(id+"F0.wireOp",EDGE,"E16.37.3"),sQuery(id+"F0.wireOp",EDGE,"E16.37.4"),sQuery(id+"F0.wireOp",EDGE,"E16.38.0"),sQuery(id+"F0.wireOp",EDGE,"E16.38.1"),sQuery(id+"F0.wireOp",EDGE,"E16.38.2"),sQuery(id+"F0.wireOp",EDGE,"E16.38.3"),sQuery(id+"F0.wireOp",EDGE,"E16.38.4"),sQuery(id+"F0.wireOp",EDGE,"E16.39.0"),sQuery(id+"F0.wireOp",EDGE,"E16.39.1"),sQuery(id+"F0.wireOp",EDGE,"E16.39.2"),sQuery(id+"F0.wireOp",EDGE,"E16.39.3"),sQuery(id+"F0.wireOp",EDGE,"E16.39.4"),sQuery(id+"F0.wireOp",EDGE,"E16.40.0"),sQuery(id+"F0.wireOp",EDGE,"E16.40.1"),sQuery(id+"F0.wireOp",EDGE,"E16.40.2"),sQuery(id+"F0.wireOp",EDGE,"E16.40.3"),sQuery(id+"F0.wireOp",EDGE,"E16.40.4"),sQuery(id+"F0.wireOp",EDGE,"E16.41.0"),sQuery(id+"F0.wireOp",EDGE,"E16.41.1"),sQuery(id+"F0.wireOp",EDGE,"E16.41.2"),sQuery(id+"F0.wireOp",EDGE,"E16.41.3"),sQuery(id+"F0.wireOp",EDGE,"E16.41.4"),sQuery(id+"F0.wireOp",EDGE,"E16.42.0"),sQuery(id+"F0.wireOp",EDGE,"E16.42.1"),sQuery(id+"F0.wireOp",EDGE,"E16.42.2"),sQuery(id+"F0.wireOp",EDGE,"E16.42.3"),sQuery(id+"F0.wireOp",EDGE,"E16.42.4"),sQuery(id+"F0.wireOp",EDGE,"E16.43.0"),sQuery(id+"F0.wireOp",EDGE,"E16.43.1"),sQuery(id+"F0.wireOp",EDGE,"E16.43.2"),sQuery(id+"F0.wireOp",EDGE,"E16.43.3"),sQuery(id+"F0.wireOp",EDGE,"E16.43.4"),sQuery(id+"F0.wireOp",EDGE,"E16.44.0"),sQuery(id+"F0.wireOp",EDGE,"E16.44.1"),sQuery(id+"F0.wireOp",EDGE,"E16.44.2"),sQuery(id+"F0.wireOp",EDGE,"E16.44.3"),sQuery(id+"F0.wireOp",EDGE,"E16.44.4"),sQuery(id+"F0.wireOp",EDGE,"E16.45.0"),sQuery(id+"F0.wireOp",EDGE,"E16.45.1"),sQuery(id+"F0.wireOp",EDGE,"E16.45.2"),sQuery(id+"F0.wireOp",EDGE,"E16.45.3"),sQuery(id+"F0.wireOp",EDGE,"E16.45.4"),sQuery(id+"F0.wireOp",EDGE,"E16.46.0"),sQuery(id+"F0.wireOp",EDGE,"E16.46.1"),sQuery(id+"F0.wireOp",EDGE,"E16.46.2"),sQuery(id+"F0.wireOp",EDGE,"E16.46.3"),sQuery(id+"F0.wireOp",EDGE,"E16.46.4"),sQuery(id+"F0.wireOp",EDGE,"E16.47.0"),sQuery(id+"F0.wireOp",EDGE,"E16.47.1"),sQuery(id+"F0.wireOp",EDGE,"E16.47.2"),sQuery(id+"F0.wireOp",EDGE,"E16.47.3"),sQuery(id+"F0.wireOp",EDGE,"E16.47.4"),sQuery(id+"F0.wireOp",EDGE,"E16.48.0"),sQuery(id+"F0.wireOp",EDGE,"E16.48.1"),sQuery(id+"F0.wireOp",EDGE,"E16.48.2"),sQuery(id+"F0.wireOp",EDGE,"E16.48.3"),sQuery(id+"F0.wireOp",EDGE,"E16.48.4"),sQuery(id+"F0.wireOp",EDGE,"E16.49.0"),sQuery(id+"F0.wireOp",EDGE,"E16.49.1"),sQuery(id+"F0.wireOp",EDGE,"E16.49.2"),sQuery(id+"F0.wireOp",EDGE,"E16.49.3"),sQuery(id+"F0.wireOp",EDGE,"E16.49.4"),sQuery(id+"F0.wireOp",EDGE,"E16.50.0"),sQuery(id+"F0.wireOp",EDGE,"E16.50.1"),sQuery(id+"F0.wireOp",EDGE,"E16.50.2"),sQuery(id+"F0.wireOp",EDGE,"E16.50.3"),sQuery(id+"F0.wireOp",EDGE,"E16.50.4"),sQuery(id+"F0.wireOp",EDGE,"E16.51.0"),sQuery(id+"F0.wireOp",EDGE,"E16.51.1"),sQuery(id+"F0.wireOp",EDGE,"E16.51.2"),sQuery(id+"F0.wireOp",EDGE,"E16.51.3"),sQuery(id+"F0.wireOp",EDGE,"E16.51.4"),sQuery(id+"F0.wireOp",EDGE,"E16.52.0"),sQuery(id+"F0.wireOp",EDGE,"E16.52.1"),sQuery(id+"F0.wireOp",EDGE,"E16.52.2"),sQuery(id+"F0.wireOp",EDGE,"E16.52.3"),sQuery(id+"F0.wireOp",EDGE,"E16.52.4"),sQuery(id+"F0.wireOp",EDGE,"E16.53.0"),sQuery(id+"F0.wireOp",EDGE,"E16.53.1"),sQuery(id+"F0.wireOp",EDGE,"E16.53.2"),sQuery(id+"F0.wireOp",EDGE,"E16.53.3"),sQuery(id+"F0.wireOp",EDGE,"E16.53.4"),sQuery(id+"F0.wireOp",EDGE,"E16.54.0"),sQuery(id+"F0.wireOp",EDGE,"E16.54.1"),sQuery(id+"F0.wireOp",EDGE,"E16.54.2"),sQuery(id+"F0.wireOp",EDGE,"E16.54.3"),sQuery(id+"F0.wireOp",EDGE,"E16.54.4"),sQuery(id+"F0.wireOp",EDGE,"E16.55.0"),sQuery(id+"F0.wireOp",EDGE,"E16.55.1"),sQuery(id+"F0.wireOp",EDGE,"E16.55.2"),sQuery(id+"F0.wireOp",EDGE,"E16.55.3"),sQuery(id+"F0.wireOp",EDGE,"E16.55.4"),sQuery(id+"F0.wireOp",EDGE,"E16.56.0"),sQuery(id+"F0.wireOp",EDGE,"E16.56.1"),sQuery(id+"F0.wireOp",EDGE,"E16.56.2"),sQuery(id+"F0.wireOp",EDGE,"E16.56.3"),sQuery(id+"F0.wireOp",EDGE,"E16.56.4"),sQuery(id+"F0.wireOp",EDGE,"E16.57.0"),sQuery(id+"F0.wireOp",EDGE,"E16.57.1"),sQuery(id+"F0.wireOp",EDGE,"E16.57.2"),sQuery(id+"F0.wireOp",EDGE,"E16.57.3"),sQuery(id+"F0.wireOp",EDGE,"E16.57.4"),sQuery(id+"F0.wireOp",EDGE,"E16.58.0"),sQuery(id+"F0.wireOp",EDGE,"E16.58.1"),sQuery(id+"F0.wireOp",EDGE,"E16.58.2"),sQuery(id+"F0.wireOp",EDGE,"E16.58.3"),sQuery(id+"F0.wireOp",EDGE,"E16.58.4"),sQuery(id+"F0.wireOp",EDGE,"E16.59.0"),sQuery(id+"F0.wireOp",EDGE,"E16.59.1"),sQuery(id+"F0.wireOp",EDGE,"E16.59.2"),sQuery(id+"F0.wireOp",EDGE,"E16.59.3"),sQuery(id+"F0.wireOp",EDGE,"E16.59.4"),sQuery(id+"F0.wireOp",EDGE,"E16.60.0"),sQuery(id+"F0.wireOp",EDGE,"E16.60.1"),sQuery(id+"F0.wireOp",EDGE,"E16.60.2"),sQuery(id+"F0.wireOp",EDGE,"E16.60.3"),sQuery(id+"F0.wireOp",EDGE,"E16.60.4"),sQuery(id+"F0.wireOp",EDGE,"E16.61.0"),sQuery(id+"F0.wireOp",EDGE,"E16.61.1"),sQuery(id+"F0.wireOp",EDGE,"E16.61.2"),sQuery(id+"F0.wireOp",EDGE,"E16.61.3"),sQuery(id+"F0.wireOp",EDGE,"E16.61.4"),sQuery(id+"F0.wireOp",EDGE,"E16.62.0"),sQuery(id+"F0.wireOp",EDGE,"E16.62.1"),sQuery(id+"F0.wireOp",EDGE,"E16.62.2"),sQuery(id+"F0.wireOp",EDGE,"E16.62.3"),sQuery(id+"F0.wireOp",EDGE,"E16.62.4"),sQuery(id+"F0.wireOp",EDGE,"E16.63.0"),sQuery(id+"F0.wireOp",EDGE,"E16.63.1"),sQuery(id+"F0.wireOp",EDGE,"E16.63.2"),sQuery(id+"F0.wireOp",EDGE,"E16.63.3"),sQuery(id+"F0.wireOp",EDGE,"E16.63.4"),sQuery(id+"F0.wireOp",EDGE,"E16.64.0"),sQuery(id+"F0.wireOp",EDGE,"E16.64.1"),sQuery(id+"F0.wireOp",EDGE,"E16.64.2"),sQuery(id+"F0.wireOp",EDGE,"E16.64.3"),sQuery(id+"F0.wireOp",EDGE,"E16.64.4"),sQuery(id+"F0.wireOp",EDGE,"E16.65.0"),sQuery(id+"F0.wireOp",EDGE,"E16.65.1"),sQuery(id+"F0.wireOp",EDGE,"E16.65.2"),sQuery(id+"F0.wireOp",EDGE,"E16.65.3"),sQuery(id+"F0.wireOp",EDGE,"E16.65.4"),sQuery(id+"F0.wireOp",EDGE,"E16.66.0"),sQuery(id+"F0.wireOp",EDGE,"E16.66.1"),sQuery(id+"F0.wireOp",EDGE,"E16.66.2"),sQuery(id+"F0.wireOp",EDGE,"E16.66.3"),sQuery(id+"F0.wireOp",EDGE,"E16.66.4"),sQuery(id+"F0.wireOp",EDGE,"E16.67.0"),sQuery(id+"F0.wireOp",EDGE,"E16.67.1"),sQuery(id+"F0.wireOp",EDGE,"E16.67.2"),sQuery(id+"F0.wireOp",EDGE,"E16.67.3"),sQuery(id+"F0.wireOp",EDGE,"E16.67.4"),sQuery(id+"F0.wireOp",EDGE,"E16.68.0"),sQuery(id+"F0.wireOp",EDGE,"E16.68.1"),sQuery(id+"F0.wireOp",EDGE,"E16.68.2"),sQuery(id+"F0.wireOp",EDGE,"E16.68.3"),sQuery(id+"F0.wireOp",EDGE,"E16.68.4"),sQuery(id+"F0.wireOp",EDGE,"E16.69.0"),sQuery(id+"F0.wireOp",EDGE,"E16.69.1"),sQuery(id+"F0.wireOp",EDGE,"E16.69.2"),sQuery(id+"F0.wireOp",EDGE,"E16.69.3"),sQuery(id+"F0.wireOp",EDGE,"E16.69.4"),sQuery(id+"F0.wireOp",EDGE,"E16.70.0"),sQuery(id+"F0.wireOp",EDGE,"E16.70.1"),sQuery(id+"F0.wireOp",EDGE,"E16.70.2"),sQuery(id+"F0.wireOp",EDGE,"E16.70.3"),sQuery(id+"F0.wireOp",EDGE,"E16.70.4"),sQuery(id+"F0.wireOp",EDGE,"E16.71.0"),sQuery(id+"F0.wireOp",EDGE,"E16.71.1"),sQuery(id+"F0.wireOp",EDGE,"E16.71.2"),sQuery(id+"F0.wireOp",EDGE,"E16.71.3"),sQuery(id+"F0.wireOp",EDGE,"E16.71.4"),sQuery(id+"F0.wireOp",EDGE,"E16.72.0"),sQuery(id+"F0.wireOp",EDGE,"E16.72.1"),sQuery(id+"F0.wireOp",EDGE,"E16.72.2"),sQuery(id+"F0.wireOp",EDGE,"E16.72.3"),sQuery(id+"F0.wireOp",EDGE,"E16.72.4"),sQuery(id+"F0.wireOp",EDGE,"E16.73.0"),sQuery(id+"F0.wireOp",EDGE,"E16.73.1"),sQuery(id+"F0.wireOp",EDGE,"E16.73.2"),sQuery(id+"F0.wireOp",EDGE,"E16.73.3"),sQuery(id+"F0.wireOp",EDGE,"E16.73.4"),sQuery(id+"F0.wireOp",EDGE,"E16.74.0"),sQuery(id+"F0.wireOp",EDGE,"E16.74.1"),sQuery(id+"F0.wireOp",EDGE,"E16.74.2"),sQuery(id+"F0.wireOp",EDGE,"E16.74.3"),sQuery(id+"F0.wireOp",EDGE,"E16.74.4"),sQuery(id+"F0.wireOp",EDGE,"E16.75.0"),sQuery(id+"F0.wireOp",EDGE,"E16.75.1"),sQuery(id+"F0.wireOp",EDGE,"E16.75.2"),sQuery(id+"F0.wireOp",EDGE,"E16.75.3"),sQuery(id+"F0.wireOp",EDGE,"E16.75.4"),sQuery(id+"F0.wireOp",EDGE,"E16.76.0"),sQuery(id+"F0.wireOp",EDGE,"E16.76.1"),sQuery(id+"F0.wireOp",EDGE,"E16.76.2"),sQuery(id+"F0.wireOp",EDGE,"E16.76.3"),sQuery(id+"F0.wireOp",EDGE,"E16.76.4"),sQuery(id+"F0.wireOp",EDGE,"E16.77.0"),sQuery(id+"F0.wireOp",EDGE,"E16.77.1"),sQuery(id+"F0.wireOp",EDGE,"E16.77.2"),sQuery(id+"F0.wireOp",EDGE,"E16.77.3"),sQuery(id+"F0.wireOp",EDGE,"E16.77.4"),sQuery(id+"F0.wireOp",EDGE,"E16.78.0"),sQuery(id+"F0.wireOp",EDGE,"E16.78.1"),sQuery(id+"F0.wireOp",EDGE,"E16.78.2"),sQuery(id+"F0.wireOp",EDGE,"E16.78.3"),sQuery(id+"F0.wireOp",EDGE,"E16.78.4"),sQuery(id+"F0.wireOp",EDGE,"E16.79.0"),sQuery(id+"F0.wireOp",EDGE,"E16.79.1"),sQuery(id+"F0.wireOp",EDGE,"E16.79.2"),sQuery(id+"F0.wireOp",EDGE,"E16.79.3"),sQuery(id+"F0.wireOp",EDGE,"E16.79.4"),sQuery(id+"F0.wireOp",EDGE,"E16.80.0"),sQuery(id+"F0.wireOp",EDGE,"E16.80.1"),sQuery(id+"F0.wireOp",EDGE,"E16.80.2"),sQuery(id+"F0.wireOp",EDGE,"E16.80.3"),sQuery(id+"F0.wireOp",EDGE,"E16.80.4"),sQuery(id+"F0.wireOp",EDGE,"E16.81.0"),sQuery(id+"F0.wireOp",EDGE,"E16.81.1"),sQuery(id+"F0.wireOp",EDGE,"E16.81.2"),sQuery(id+"F0.wireOp",EDGE,"E16.81.3"),sQuery(id+"F0.wireOp",EDGE,"E16.81.4"),sQuery(id+"F0.wireOp",EDGE,"E16.82.0"),sQuery(id+"F0.wireOp",EDGE,"E16.82.1"),sQuery(id+"F0.wireOp",EDGE,"E16.82.2"),sQuery(id+"F0.wireOp",EDGE,"E16.82.3"),sQuery(id+"F0.wireOp",EDGE,"E16.82.4"),sQuery(id+"F0.wireOp",EDGE,"E16.83.0"),sQuery(id+"F0.wireOp",EDGE,"E16.83.1"),sQuery(id+"F0.wireOp",EDGE,"E16.83.2"),sQuery(id+"F0.wireOp",EDGE,"E16.83.3"),sQuery(id+"F0.wireOp",EDGE,"E16.83.4"),sQuery(id+"F0.wireOp",EDGE,"E16.84.0"),sQuery(id+"F0.wireOp",EDGE,"E16.84.1"),sQuery(id+"F0.wireOp",EDGE,"E16.84.2"),sQuery(id+"F0.wireOp",EDGE,"E16.84.3"),sQuery(id+"F0.wireOp",EDGE,"E16.84.4"),sQuery(id+"F0.wireOp",EDGE,"E16.85.0"),sQuery(id+"F0.wireOp",EDGE,"E16.85.1"),sQuery(id+"F0.wireOp",EDGE,"E16.85.2"),sQuery(id+"F0.wireOp",EDGE,"E16.85.3"),sQuery(id+"F0.wireOp",EDGE,"E16.85.4"),sQuery(id+"F0.wireOp",EDGE,"E16.86.0"),sQuery(id+"F0.wireOp",EDGE,"E16.86.1"),sQuery(id+"F0.wireOp",EDGE,"E16.86.2"),sQuery(id+"F0.wireOp",EDGE,"E16.86.3"),sQuery(id+"F0.wireOp",EDGE,"E16.86.4"),sQuery(id+"F0.wireOp",EDGE,"E16.87.0"),sQuery(id+"F0.wireOp",EDGE,"E16.87.1"),sQuery(id+"F0.wireOp",EDGE,"E16.87.2"),sQuery(id+"F0.wireOp",EDGE,"E16.87.3"),sQuery(id+"F0.wireOp",EDGE,"E16.87.4"),sQuery(id+"F0.wireOp",EDGE,"E16.88.0"),sQuery(id+"F0.wireOp",EDGE,"E16.88.1"),sQuery(id+"F0.wireOp",EDGE,"E16.88.2"),sQuery(id+"F0.wireOp",EDGE,"E16.88.3"),sQuery(id+"F0.wireOp",EDGE,"E16.88.4"),sQuery(id+"F0.wireOp",EDGE,"E16.89.0"),sQuery(id+"F0.wireOp",EDGE,"E16.89.1"),sQuery(id+"F0.wireOp",EDGE,"E16.89.2"),sQuery(id+"F0.wireOp",EDGE,"E16.89.3"),sQuery(id+"F0.wireOp",EDGE,"E16.89.4"),sQuery(id+"F0.wireOp",EDGE,"E16.90.0"),sQuery(id+"F0.wireOp",EDGE,"E16.90.1"),sQuery(id+"F0.wireOp",EDGE,"E16.90.2"),sQuery(id+"F0.wireOp",EDGE,"E16.90.3"),sQuery(id+"F0.wireOp",EDGE,"E16.90.4"),sQuery(id+"F0.wireOp",EDGE,"E16.91.0"),sQuery(id+"F0.wireOp",EDGE,"E16.91.1"),sQuery(id+"F0.wireOp",EDGE,"E16.91.2"),sQuery(id+"F0.wireOp",EDGE,"E16.91.3"),sQuery(id+"F0.wireOp",EDGE,"E16.91.4"),sQuery(id+"F0.wireOp",EDGE,"E16.92.0"),sQuery(id+"F0.wireOp",EDGE,"E16.92.1"),sQuery(id+"F0.wireOp",EDGE,"E16.92.2"),sQuery(id+"F0.wireOp",EDGE,"E16.92.3"),sQuery(id+"F0.wireOp",EDGE,"E16.92.4"),sQuery(id+"F0.wireOp",EDGE,"E16.93.0"),sQuery(id+"F0.wireOp",EDGE,"E16.93.1"),sQuery(id+"F0.wireOp",EDGE,"E16.93.2"),sQuery(id+"F0.wireOp",EDGE,"E16.93.3"),sQuery(id+"F0.wireOp",EDGE,"E16.93.4"),sQuery(id+"F0.wireOp",EDGE,"E16.94.0"),sQuery(id+"F0.wireOp",EDGE,"E16.94.1"),sQuery(id+"F0.wireOp",EDGE,"E16.94.2"),sQuery(id+"F0.wireOp",EDGE,"E16.94.3"),sQuery(id+"F0.wireOp",EDGE,"E16.94.4"),sQuery(id+"F0.wireOp",EDGE,"E16.95.0"),sQuery(id+"F0.wireOp",EDGE,"E16.95.1"),sQuery(id+"F0.wireOp",EDGE,"E16.95.2"),sQuery(id+"F0.wireOp",EDGE,"E16.95.3"),sQuery(id+"F0.wireOp",EDGE,"E16.95.4"),sQuery(id+"F0.wireOp",EDGE,"E16.96.0"),sQuery(id+"F0.wireOp",EDGE,"E16.96.1"),sQuery(id+"F0.wireOp",EDGE,"E16.96.2"),sQuery(id+"F0.wireOp",EDGE,"E16.96.3"),sQuery(id+"F0.wireOp",EDGE,"E16.96.4"),sQuery(id+"F0.wireOp",EDGE,"E16.97.0"),sQuery(id+"F0.wireOp",EDGE,"E16.97.1"),sQuery(id+"F0.wireOp",EDGE,"E16.97.2"),sQuery(id+"F0.wireOp",EDGE,"E16.97.3"),sQuery(id+"F0.wireOp",EDGE,"E16.97.4"),sQuery(id+"F0.wireOp",EDGE,"E16.98.0"),sQuery(id+"F0.wireOp",EDGE,"E16.98.1"),sQuery(id+"F0.wireOp",EDGE,"E16.98.2"),sQuery(id+"F0.wireOp",EDGE,"E16.98.3"),sQuery(id+"F0.wireOp",EDGE,"E16.98.4"),sQuery(id+"F0.wireOp",EDGE,"E16.99.0"),sQuery(id+"F0.wireOp",EDGE,"E16.99.1"),sQuery(id+"F0.wireOp",EDGE,"E16.99.2"),sQuery(id+"F0.wireOp",EDGE,"E16.99.3"),sQuery(id+"F0.wireOp",EDGE,"E16.99.4"),sQuery(id+"F0.wireOp",EDGE,"E16.100.0"),sQuery(id+"F0.wireOp",EDGE,"E16.100.1"),sQuery(id+"F0.wireOp",EDGE,"E16.100.2"),sQuery(id+"F0.wireOp",EDGE,"E16.100.3"),sQuery(id+"F0.wireOp",EDGE,"E16.100.4"),sQuery(id+"F0.wireOp",EDGE,"E16.101.0"),sQuery(id+"F0.wireOp",EDGE,"E16.101.1"),sQuery(id+"F0.wireOp",EDGE,"E16.101.2"),sQuery(id+"F0.wireOp",EDGE,"E16.101.3"),sQuery(id+"F0.wireOp",EDGE,"E16.101.4"),sQuery(id+"F0.wireOp",EDGE,"E16.102.0"),sQuery(id+"F0.wireOp",EDGE,"E16.102.1"),sQuery(id+"F0.wireOp",EDGE,"E16.102.2"),sQuery(id+"F0.wireOp",EDGE,"E16.102.3"),sQuery(id+"F0.wireOp",EDGE,"E16.102.4"),sQuery(id+"F0.wireOp",EDGE,"E16.103.0"),sQuery(id+"F0.wireOp",EDGE,"E16.103.1"),sQuery(id+"F0.wireOp",EDGE,"E16.103.2"),sQuery(id+"F0.wireOp",EDGE,"E16.103.3"),sQuery(id+"F0.wireOp",EDGE,"E16.103.4"),sQuery(id+"F0.wireOp",EDGE,"E16.104.0"),sQuery(id+"F0.wireOp",EDGE,"E16.104.1"),sQuery(id+"F0.wireOp",EDGE,"E16.104.2"),sQuery(id+"F0.wireOp",EDGE,"E16.104.3"),sQuery(id+"F0.wireOp",EDGE,"E16.104.4"),sQuery(id+"F0.wireOp",EDGE,"E16.105.0"),sQuery(id+"F0.wireOp",EDGE,"E16.105.1"),sQuery(id+"F0.wireOp",EDGE,"E16.105.2"),sQuery(id+"F0.wireOp",EDGE,"E16.105.3"),sQuery(id+"F0.wireOp",EDGE,"E16.105.4"),sQuery(id+"F0.wireOp",EDGE,"E16.106.0"),sQuery(id+"F0.wireOp",EDGE,"E16.106.1"),sQuery(id+"F0.wireOp",EDGE,"E16.106.2"),sQuery(id+"F0.wireOp",EDGE,"E16.106.3"),sQuery(id+"F0.wireOp",EDGE,"E16.106.4"),sQuery(id+"F0.wireOp",EDGE,"E16.107.0"),sQuery(id+"F0.wireOp",EDGE,"E16.107.1"),sQuery(id+"F0.wireOp",EDGE,"E16.107.2"),sQuery(id+"F0.wireOp",EDGE,"E16.107.3"),sQuery(id+"F0.wireOp",EDGE,"E16.107.4"),sQuery(id+"F0.wireOp",EDGE,"E16.108.0"),sQuery(id+"F0.wireOp",EDGE,"E16.108.1"),sQuery(id+"F0.wireOp",EDGE,"E16.108.2"),sQuery(id+"F0.wireOp",EDGE,"E16.108.3"),sQuery(id+"F0.wireOp",EDGE,"E16.108.4"),sQuery(id+"F0.wireOp",EDGE,"E16.109.0"),sQuery(id+"F0.wireOp",EDGE,"E16.109.1"),sQuery(id+"F0.wireOp",EDGE,"E16.109.2"),sQuery(id+"F0.wireOp",EDGE,"E16.109.3"),sQuery(id+"F0.wireOp",EDGE,"E16.109.4"),sQuery(id+"F0.wireOp",EDGE,"E16.110.0"),sQuery(id+"F0.wireOp",EDGE,"E16.110.1"),sQuery(id+"F0.wireOp",EDGE,"E16.110.2"),sQuery(id+"F0.wireOp",EDGE,"E16.110.3"),sQuery(id+"F0.wireOp",EDGE,"E16.110.4"),sQuery(id+"F0.wireOp",EDGE,"E16.111.0"),sQuery(id+"F0.wireOp",EDGE,"E16.111.1"),sQuery(id+"F0.wireOp",EDGE,"E16.111.2"),sQuery(id+"F0.wireOp",EDGE,"E16.111.3"),sQuery(id+"F0.wireOp",EDGE,"E16.111.4"),sQuery(id+"F0.wireOp",EDGE,"E16.112.0"),sQuery(id+"F0.wireOp",EDGE,"E16.112.1"),sQuery(id+"F0.wireOp",EDGE,"E16.112.2"),sQuery(id+"F0.wireOp",EDGE,"E16.112.3"),sQuery(id+"F0.wireOp",EDGE,"E16.112.4"),sQuery(id+"F0.wireOp",EDGE,"E16.113.0"),sQuery(id+"F0.wireOp",EDGE,"E16.113.1"),sQuery(id+"F0.wireOp",EDGE,"E16.113.2"),sQuery(id+"F0.wireOp",EDGE,"E16.113.3"),sQuery(id+"F0.wireOp",EDGE,"E16.113.4"),sQuery(id+"F0.wireOp",EDGE,"E16.114.0"),sQuery(id+"F0.wireOp",EDGE,"E16.114.1"),sQuery(id+"F0.wireOp",EDGE,"E16.114.2"),sQuery(id+"F0.wireOp",EDGE,"E16.114.3"),sQuery(id+"F0.wireOp",EDGE,"E16.114.4"),sQuery(id+"F0.wireOp",EDGE,"E16.115.0"),sQuery(id+"F0.wireOp",EDGE,"E16.115.1"),sQuery(id+"F0.wireOp",EDGE,"E16.115.2"),sQuery(id+"F0.wireOp",EDGE,"E16.115.3"),sQuery(id+"F0.wireOp",EDGE,"E16.115.4"),sQuery(id+"F0.wireOp",EDGE,"E16.116.0"),sQuery(id+"F0.wireOp",EDGE,"E16.116.1"),sQuery(id+"F0.wireOp",EDGE,"E16.116.2"),sQuery(id+"F0.wireOp",EDGE,"E16.116.3"),sQuery(id+"F0.wireOp",EDGE,"E16.116.4"),sQuery(id+"F0.wireOp",EDGE,"E16.117.0"),sQuery(id+"F0.wireOp",EDGE,"E16.117.1"),sQuery(id+"F0.wireOp",EDGE,"E16.117.2"),sQuery(id+"F0.wireOp",EDGE,"E16.117.3"),sQuery(id+"F0.wireOp",EDGE,"E16.117.4"),sQuery(id+"F0.wireOp",EDGE,"E16.118.0"),sQuery(id+"F0.wireOp",EDGE,"E16.118.1"),sQuery(id+"F0.wireOp",EDGE,"E16.118.2"),sQuery(id+"F0.wireOp",EDGE,"E16.118.3"),sQuery(id+"F0.wireOp",EDGE,"E16.118.4"),sQuery(id+"F0.wireOp",EDGE,"E16.119.0"),sQuery(id+"F0.wireOp",EDGE,"E16.119.1"),sQuery(id+"F0.wireOp",EDGE,"E16.119.2"),sQuery(id+"F0.wireOp",EDGE,"E16.119.3"),sQuery(id+"F0.wireOp",EDGE,"E16.119.4"),sQuery(id+"F0.wireOp",EDGE,"E16.120.0"),sQuery(id+"F0.wireOp",EDGE,"E16.120.1"),sQuery(id+"F0.wireOp",EDGE,"E16.120.2"),sQuery(id+"F0.wireOp",EDGE,"E16.120.3"),sQuery(id+"F0.wireOp",EDGE,"E16.120.4"),sQuery(id+"F0.wireOp",EDGE,"E16.121.0"),sQuery(id+"F0.wireOp",EDGE,"E16.121.1"),sQuery(id+"F0.wireOp",EDGE,"E16.121.2"),sQuery(id+"F0.wireOp",EDGE,"E16.121.3"),sQuery(id+"F0.wireOp",EDGE,"E16.121.4"),sQuery(id+"F0.wireOp",EDGE,"E16.122.0"),sQuery(id+"F0.wireOp",EDGE,"E16.122.1"),sQuery(id+"F0.wireOp",EDGE,"E16.122.2"),sQuery(id+"F0.wireOp",EDGE,"E16.122.3"),sQuery(id+"F0.wireOp",EDGE,"E16.122.4"),sQuery(id+"F0.wireOp",EDGE,"E16.123.0"),sQuery(id+"F0.wireOp",EDGE,"E16.123.1"),sQuery(id+"F0.wireOp",EDGE,"E16.123.2"),sQuery(id+"F0.wireOp",EDGE,"E16.123.3"),sQuery(id+"F0.wireOp",EDGE,"E16.123.4"),sQuery(id+"F0.wireOp",EDGE,"E16.124.0"),sQuery(id+"F0.wireOp",EDGE,"E16.124.1"),sQuery(id+"F0.wireOp",EDGE,"E16.124.2"),sQuery(id+"F0.wireOp",EDGE,"E16.124.3"),sQuery(id+"F0.wireOp",EDGE,"E16.124.4"),sQuery(id+"F0.wireOp",EDGE,"E16.125.0"),sQuery(id+"F0.wireOp",EDGE,"E16.125.1"),sQuery(id+"F0.wireOp",EDGE,"E16.125.2"),sQuery(id+"F0.wireOp",EDGE,"E16.125.3"),sQuery(id+"F0.wireOp",EDGE,"E16.125.4"),sQuery(id+"F0.wireOp",EDGE,"E16.126.0"),sQuery(id+"F0.wireOp",EDGE,"E16.126.1"),sQuery(id+"F0.wireOp",EDGE,"E16.126.2"),sQuery(id+"F0.wireOp",EDGE,"E16.126.3"),sQuery(id+"F0.wireOp",EDGE,"E16.126.4"),sQuery(id+"F0.wireOp",EDGE,"E16.127.0"),sQuery(id+"F0.wireOp",EDGE,"E16.127.1"),sQuery(id+"F0.wireOp",EDGE,"E16.127.2"),sQuery(id+"F0.wireOp",EDGE,"E16.127.3"),sQuery(id+"F0.wireOp",EDGE,"E16.127.4"),sQuery(id+"F0.wireOp",EDGE,"E16.128.0"),sQuery(id+"F0.wireOp",EDGE,"E16.128.1"),sQuery(id+"F0.wireOp",EDGE,"E16.128.2"),sQuery(id+"F0.wireOp",EDGE,"E16.128.3"),sQuery(id+"F0.wireOp",EDGE,"E16.128.4"),sQuery(id+"F0.wireOp",EDGE,"E16.129.0"),sQuery(id+"F0.wireOp",EDGE,"E16.129.1"),sQuery(id+"F0.wireOp",EDGE,"E16.129.2"),sQuery(id+"F0.wireOp",EDGE,"E16.129.3"),sQuery(id+"F0.wireOp",EDGE,"E16.129.4"),sQuery(id+"F0.wireOp",EDGE,"E16.130.0"),sQuery(id+"F0.wireOp",EDGE,"E16.130.1"),sQuery(id+"F0.wireOp",EDGE,"E16.130.2"),sQuery(id+"F0.wireOp",EDGE,"E16.130.3"),sQuery(id+"F0.wireOp",EDGE,"E16.130.4"),sQuery(id+"F0.wireOp",EDGE,"E16.131.0"),sQuery(id+"F0.wireOp",EDGE,"E16.131.1"),sQuery(id+"F0.wireOp",EDGE,"E16.131.2"),sQuery(id+"F0.wireOp",EDGE,"E16.131.3"),sQuery(id+"F0.wireOp",EDGE,"E16.131.4"),sQuery(id+"F0.wireOp",EDGE,"E16.132.0"),sQuery(id+"F0.wireOp",EDGE,"E16.132.1"),sQuery(id+"F0.wireOp",EDGE,"E16.132.2"),sQuery(id+"F0.wireOp",EDGE,"E16.132.3"),sQuery(id+"F0.wireOp",EDGE,"E16.132.4"),sQuery(id+"F0.wireOp",EDGE,"E16.133.0"),sQuery(id+"F0.wireOp",EDGE,"E16.133.1"),sQuery(id+"F0.wireOp",EDGE,"E16.133.2"),sQuery(id+"F0.wireOp",EDGE,"E16.133.3"),sQuery(id+"F0.wireOp",EDGE,"E16.133.4"),sQuery(id+"F0.wireOp",EDGE,"E16.134.0"),sQuery(id+"F0.wireOp",EDGE,"E16.134.1"),sQuery(id+"F0.wireOp",EDGE,"E16.134.2"),sQuery(id+"F0.wireOp",EDGE,"E16.134.3"),sQuery(id+"F0.wireOp",EDGE,"E16.134.4"),sQuery(id+"F0.wireOp",EDGE,"E16.135.0"),sQuery(id+"F0.wireOp",EDGE,"E16.135.1"),sQuery(id+"F0.wireOp",EDGE,"E16.135.2"),sQuery(id+"F0.wireOp",EDGE,"E16.135.3"),sQuery(id+"F0.wireOp",EDGE,"E16.135.4"),sQuery(id+"F0.wireOp",EDGE,"E16.136.0"),sQuery(id+"F0.wireOp",EDGE,"E16.136.1"),sQuery(id+"F0.wireOp",EDGE,"E16.136.2"),sQuery(id+"F0.wireOp",EDGE,"E16.136.3"),sQuery(id+"F0.wireOp",EDGE,"E16.136.4"),sQuery(id+"F0.wireOp",EDGE,"E16.137.0"),sQuery(id+"F0.wireOp",EDGE,"E16.137.1"),sQuery(id+"F0.wireOp",EDGE,"E16.137.2"),sQuery(id+"F0.wireOp",EDGE,"E16.137.3"),sQuery(id+"F0.wireOp",EDGE,"E16.137.4"),sQuery(id+"F0.wireOp",EDGE,"E16.138.0"),sQuery(id+"F0.wireOp",EDGE,"E16.138.1"),sQuery(id+"F0.wireOp",EDGE,"E16.138.2"),sQuery(id+"F0.wireOp",EDGE,"E16.138.3"),sQuery(id+"F0.wireOp",EDGE,"E16.138.4"),sQuery(id+"F0.wireOp",EDGE,"E16.139.0"),sQuery(id+"F0.wireOp",EDGE,"E16.139.1"),sQuery(id+"F0.wireOp",EDGE,"E16.139.2"),sQuery(id+"F0.wireOp",EDGE,"E16.139.3"),sQuery(id+"F0.wireOp",EDGE,"E16.139.4"),sQuery(id+"F0.wireOp",EDGE,"E16.140.0"),sQuery(id+"F0.wireOp",EDGE,"E16.140.1"),sQuery(id+"F0.wireOp",EDGE,"E16.140.2"),sQuery(id+"F0.wireOp",EDGE,"E16.140.3"),sQuery(id+"F0.wireOp",EDGE,"E16.140.4"),sQuery(id+"F0.wireOp",EDGE,"E16.141.0"),sQuery(id+"F0.wireOp",EDGE,"E16.141.1"),sQuery(id+"F0.wireOp",EDGE,"E16.141.2"),sQuery(id+"F0.wireOp",EDGE,"E16.141.3"),sQuery(id+"F0.wireOp",EDGE,"E16.141.4"),sQuery(id+"F0.wireOp",EDGE,"E16.142.0"),sQuery(id+"F0.wireOp",EDGE,"E16.142.1"),sQuery(id+"F0.wireOp",EDGE,"E16.142.2"),sQuery(id+"F0.wireOp",EDGE,"E16.142.3"),sQuery(id+"F0.wireOp",EDGE,"E16.142.4"),sQuery(id+"F0.wireOp",EDGE,"E16.143.0"),sQuery(id+"F0.wireOp",EDGE,"E16.143.1"),sQuery(id+"F0.wireOp",EDGE,"E16.143.2"),sQuery(id+"F0.wireOp",EDGE,"E16.143.3"),sQuery(id+"F0.wireOp",EDGE,"E16.143.4"),sQuery(id+"F0.wireOp",EDGE,"E16.144.0"),sQuery(id+"F0.wireOp",EDGE,"E16.144.1"),sQuery(id+"F0.wireOp",EDGE,"E16.144.2"),sQuery(id+"F0.wireOp",EDGE,"E16.144.3"),sQuery(id+"F0.wireOp",EDGE,"E16.144.4"),sQuery(id+"F0.wireOp",EDGE,"E16.145.0"),sQuery(id+"F0.wireOp",EDGE,"E16.145.1"),sQuery(id+"F0.wireOp",EDGE,"E16.145.2"),sQuery(id+"F0.wireOp",EDGE,"E16.145.3"),sQuery(id+"F0.wireOp",EDGE,"E16.145.4"),sQuery(id+"F0.wireOp",EDGE,"E16.146.0"),sQuery(id+"F0.wireOp",EDGE,"E16.146.1"),sQuery(id+"F0.wireOp",EDGE,"E16.146.2"),sQuery(id+"F0.wireOp",EDGE,"E16.146.3"),sQuery(id+"F0.wireOp",EDGE,"E16.146.4"),sQuery(id+"F0.wireOp",EDGE,"E16.147.0"),sQuery(id+"F0.wireOp",EDGE,"E16.147.1"),sQuery(id+"F0.wireOp",EDGE,"E16.147.2"),sQuery(id+"F0.wireOp",EDGE,"E16.147.3"),sQuery(id+"F0.wireOp",EDGE,"E16.147.4"),sQuery(id+"F0.wireOp",EDGE,"E16.148.0"),sQuery(id+"F0.wireOp",EDGE,"E16.148.1"),sQuery(id+"F0.wireOp",EDGE,"E16.148.2"),sQuery(id+"F0.wireOp",EDGE,"E16.148.3"),sQuery(id+"F0.wireOp",EDGE,"E16.148.4"),sQuery(id+"F0.wireOp",EDGE,"E16.149.0"),sQuery(id+"F0.wireOp",EDGE,"E16.149.1"),sQuery(id+"F0.wireOp",EDGE,"E16.149.2"),sQuery(id+"F0.wireOp",EDGE,"E16.149.3"),sQuery(id+"F0.wireOp",EDGE,"E16.149.4"),sQuery(id+"F0.wireOp",EDGE,"E16.150.0"),sQuery(id+"F0.wireOp",EDGE,"E16.150.1"),sQuery(id+"F0.wireOp",EDGE,"E16.150.2"),sQuery(id+"F0.wireOp",EDGE,"E16.150.3"),sQuery(id+"F0.wireOp",EDGE,"E16.150.4"),sQuery(id+"F0.wireOp",EDGE,"E16.151.0"),sQuery(id+"F0.wireOp",EDGE,"E16.151.1"),sQuery(id+"F0.wireOp",EDGE,"E16.151.2"),sQuery(id+"F0.wireOp",EDGE,"E16.151.3"),sQuery(id+"F0.wireOp",EDGE,"E16.151.4"),sQuery(id+"F0.wireOp",EDGE,"E16.152.0"),sQuery(id+"F0.wireOp",EDGE,"E16.152.1"),sQuery(id+"F0.wireOp",EDGE,"E16.152.2"),sQuery(id+"F0.wireOp",EDGE,"E16.152.3"),sQuery(id+"F0.wireOp",EDGE,"E16.152.4"),sQuery(id+"F0.wireOp",EDGE,"E16.153.0"),sQuery(id+"F0.wireOp",EDGE,"E16.153.1"),sQuery(id+"F0.wireOp",EDGE,"E16.153.2"),sQuery(id+"F0.wireOp",EDGE,"E16.153.3"),sQuery(id+"F0.wireOp",EDGE,"E16.153.4"),sQuery(id+"F0.wireOp",EDGE,"E16.154.0"),sQuery(id+"F0.wireOp",EDGE,"E16.154.1"),sQuery(id+"F0.wireOp",EDGE,"E16.154.2"),sQuery(id+"F0.wireOp",EDGE,"E16.154.3"),sQuery(id+"F0.wireOp",EDGE,"E16.154.4"),sQuery(id+"F0.wireOp",EDGE,"E16.155.0"),sQuery(id+"F0.wireOp",EDGE,"E16.155.1"),sQuery(id+"F0.wireOp",EDGE,"E16.155.2"),sQuery(id+"F0.wireOp",EDGE,"E16.155.3"),sQuery(id+"F0.wireOp",EDGE,"E16.155.4"),sQuery(id+"F0.wireOp",EDGE,"E16.156.0"),sQuery(id+"F0.wireOp",EDGE,"E16.156.1"),sQuery(id+"F0.wireOp",EDGE,"E16.156.2"),sQuery(id+"F0.wireOp",EDGE,"E16.156.3"),sQuery(id+"F0.wireOp",EDGE,"E16.156.4"),sQuery(id+"F0.wireOp",EDGE,"E16.157.0"),sQuery(id+"F0.wireOp",EDGE,"E16.157.1"),sQuery(id+"F0.wireOp",EDGE,"E16.157.2"),sQuery(id+"F0.wireOp",EDGE,"E16.157.3"),sQuery(id+"F0.wireOp",EDGE,"E16.157.4"),sQuery(id+"F0.wireOp",EDGE,"E16.158.0"),sQuery(id+"F0.wireOp",EDGE,"E16.158.1"),sQuery(id+"F0.wireOp",EDGE,"E16.158.2"),sQuery(id+"F0.wireOp",EDGE,"E16.158.3"),sQuery(id+"F0.wireOp",EDGE,"E16.158.4"),sQuery(id+"F0.wireOp",EDGE,"E16.159.0"),sQuery(id+"F0.wireOp",EDGE,"E16.159.1"),sQuery(id+"F0.wireOp",EDGE,"E16.159.2"),sQuery(id+"F0.wireOp",EDGE,"E16.159.3"),sQuery(id+"F0.wireOp",EDGE,"E16.159.4"),sQuery(id+"F0.wireOp",EDGE,"E16.160.0"),sQuery(id+"F0.wireOp",EDGE,"E16.160.1"),sQuery(id+"F0.wireOp",EDGE,"E16.160.2"),sQuery(id+"F0.wireOp",EDGE,"E16.160.3"),sQuery(id+"F0.wireOp",EDGE,"E16.160.4"),sQuery(id+"F0.wireOp",EDGE,"E16.161.0"),sQuery(id+"F0.wireOp",EDGE,"E16.161.1"),sQuery(id+"F0.wireOp",EDGE,"E16.161.2"),sQuery(id+"F0.wireOp",EDGE,"E16.161.3"),sQuery(id+"F0.wireOp",EDGE,"E16.161.4"),sQuery(id+"F0.wireOp",EDGE,"E16.162.0"),sQuery(id+"F0.wireOp",EDGE,"E16.162.1"),sQuery(id+"F0.wireOp",EDGE,"E16.162.2"),sQuery(id+"F0.wireOp",EDGE,"E16.162.3"),sQuery(id+"F0.wireOp",EDGE,"E16.162.4"),sQuery(id+"F0.wireOp",EDGE,"E16.163.0"),sQuery(id+"F0.wireOp",EDGE,"E16.163.1"),sQuery(id+"F0.wireOp",EDGE,"E16.163.2"),sQuery(id+"F0.wireOp",EDGE,"E16.163.3"),sQuery(id+"F0.wireOp",EDGE,"E16.163.4"),sQuery(id+"F0.wireOp",EDGE,"E16.164.0"),sQuery(id+"F0.wireOp",EDGE,"E16.164.1"),sQuery(id+"F0.wireOp",EDGE,"E16.164.2"),sQuery(id+"F0.wireOp",EDGE,"E16.164.3"),sQuery(id+"F0.wireOp",EDGE,"E16.164.4"),sQuery(id+"F0.wireOp",EDGE,"E16.165.0"),sQuery(id+"F0.wireOp",EDGE,"E16.165.1"),sQuery(id+"F0.wireOp",EDGE,"E16.165.2"),sQuery(id+"F0.wireOp",EDGE,"E16.165.3"),sQuery(id+"F0.wireOp",EDGE,"E16.165.4"),sQuery(id+"F0.wireOp",EDGE,"E16.166.0"),sQuery(id+"F0.wireOp",EDGE,"E16.166.1"),sQuery(id+"F0.wireOp",EDGE,"E16.166.2"),sQuery(id+"F0.wireOp",EDGE,"E16.166.3"),sQuery(id+"F0.wireOp",EDGE,"E16.166.4"),sQuery(id+"F0.wireOp",EDGE,"E16.167.0"),sQuery(id+"F0.wireOp",EDGE,"E16.167.1"),sQuery(id+"F0.wireOp",EDGE,"E16.167.2"),sQuery(id+"F0.wireOp",EDGE,"E16.167.3"),sQuery(id+"F0.wireOp",EDGE,"E16.167.4"),sQuery(id+"F0.wireOp",EDGE,"E16.168.0"),sQuery(id+"F0.wireOp",EDGE,"E16.168.1"),sQuery(id+"F0.wireOp",EDGE,"E16.168.2"),sQuery(id+"F0.wireOp",EDGE,"E16.168.3"),sQuery(id+"F0.wireOp",EDGE,"E16.168.4"),sQuery(id+"F0.wireOp",EDGE,"E16.169.0"),sQuery(id+"F0.wireOp",EDGE,"E16.169.1"),sQuery(id+"F0.wireOp",EDGE,"E16.169.2"),sQuery(id+"F0.wireOp",EDGE,"E16.169.3"),sQuery(id+"F0.wireOp",EDGE,"E16.169.4"),sQuery(id+"F0.wireOp",EDGE,"E16.170.0"),sQuery(id+"F0.wireOp",EDGE,"E16.170.1"),sQuery(id+"F0.wireOp",EDGE,"E16.170.2"),sQuery(id+"F0.wireOp",EDGE,"E16.170.3"),sQuery(id+"F0.wireOp",EDGE,"E16.170.4"),sQuery(id+"F0.wireOp",EDGE,"E16.171.0"),sQuery(id+"F0.wireOp",EDGE,"E16.171.1"),sQuery(id+"F0.wireOp",EDGE,"E16.171.2"),sQuery(id+"F0.wireOp",EDGE,"E16.171.3"),sQuery(id+"F0.wireOp",EDGE,"E16.171.4"),sQuery(id+"F0.wireOp",EDGE,"E16.172.0"),sQuery(id+"F0.wireOp",EDGE,"E16.172.1"),sQuery(id+"F0.wireOp",EDGE,"E16.172.2"),sQuery(id+"F0.wireOp",EDGE,"E16.172.3"),sQuery(id+"F0.wireOp",EDGE,"E16.172.4"),sQuery(id+"F0.wireOp",EDGE,"E16.173.0"),sQuery(id+"F0.wireOp",EDGE,"E16.173.1"),sQuery(id+"F0.wireOp",EDGE,"E16.173.2"),sQuery(id+"F0.wireOp",EDGE,"E16.173.3"),sQuery(id+"F0.wireOp",EDGE,"E16.173.4"),sQuery(id+"F0.wireOp",EDGE,"E16.174.0"),sQuery(id+"F0.wireOp",EDGE,"E16.174.1"),sQuery(id+"F0.wireOp",EDGE,"E16.174.2"),sQuery(id+"F0.wireOp",EDGE,"E16.174.3"),sQuery(id+"F0.wireOp",EDGE,"E16.174.4"),sQuery(id+"F0.wireOp",EDGE,"E16.175.0"),sQuery(id+"F0.wireOp",EDGE,"E16.175.1"),sQuery(id+"F0.wireOp",EDGE,"E16.175.2"),sQuery(id+"F0.wireOp",EDGE,"E16.175.3"),sQuery(id+"F0.wireOp",EDGE,"E16.175.4"),sQuery(id+"F0.wireOp",EDGE,"E16.176.0"),sQuery(id+"F0.wireOp",EDGE,"E16.176.1"),sQuery(id+"F0.wireOp",EDGE,"E16.176.2"),sQuery(id+"F0.wireOp",EDGE,"E16.176.3"),sQuery(id+"F0.wireOp",EDGE,"E16.176.4"),sQuery(id+"F0.wireOp",EDGE,"E16.177.0"),sQuery(id+"F0.wireOp",EDGE,"E16.177.1"),sQuery(id+"F0.wireOp",EDGE,"E16.177.2"),sQuery(id+"F0.wireOp",EDGE,"E16.177.3"),sQuery(id+"F0.wireOp",EDGE,"E16.177.4"),sQuery(id+"F0.wireOp",EDGE,"E16.178.0"),sQuery(id+"F0.wireOp",EDGE,"E16.178.1"),sQuery(id+"F0.wireOp",EDGE,"E16.178.2"),sQuery(id+"F0.wireOp",EDGE,"E16.178.3"),sQuery(id+"F0.wireOp",EDGE,"E16.178.4"),sQuery(id+"F0.wireOp",EDGE,"E16.179.0"),sQuery(id+"F0.wireOp",EDGE,"E16.179.1"),sQuery(id+"F0.wireOp",EDGE,"E16.179.2"),sQuery(id+"F0.wireOp",EDGE,"E16.179.3"),sQuery(id+"F0.wireOp",EDGE,"E16.179.4"),sQuery(id+"F0.wireOp",EDGE,"E16.180.0"),sQuery(id+"F0.wireOp",EDGE,"E16.180.1"),sQuery(id+"F0.wireOp",EDGE,"E16.180.2"),sQuery(id+"F0.wireOp",EDGE,"E16.180.3"),sQuery(id+"F0.wireOp",EDGE,"E16.180.4"),sQuery(id+"F0.wireOp",EDGE,"E16.181.0"),sQuery(id+"F0.wireOp",EDGE,"E16.181.1"),sQuery(id+"F0.wireOp",EDGE,"E16.181.2"),sQuery(id+"F0.wireOp",EDGE,"E16.181.3"),sQuery(id+"F0.wireOp",EDGE,"E16.181.4"),sQuery(id+"F0.wireOp",EDGE,"E16.182.0"),sQuery(id+"F0.wireOp",EDGE,"E16.182.1"),sQuery(id+"F0.wireOp",EDGE,"E16.182.2"),sQuery(id+"F0.wireOp",EDGE,"E16.182.3"),sQuery(id+"F0.wireOp",EDGE,"E16.182.4"),sQuery(id+"F0.wireOp",EDGE,"E16.183.0"),sQuery(id+"F0.wireOp",EDGE,"E16.183.1"),sQuery(id+"F0.wireOp",EDGE,"E16.183.2"),sQuery(id+"F0.wireOp",EDGE,"E16.183.3"),sQuery(id+"F0.wireOp",EDGE,"E16.183.4"),sQuery(id+"F0.wireOp",EDGE,"E16.184.0"),sQuery(id+"F0.wireOp",EDGE,"E16.184.1"),sQuery(id+"F0.wireOp",EDGE,"E16.184.2"),sQuery(id+"F0.wireOp",EDGE,"E16.184.3"),sQuery(id+"F0.wireOp",EDGE,"E16.184.4"),sQuery(id+"F0.wireOp",EDGE,"E16.185.0"),sQuery(id+"F0.wireOp",EDGE,"E16.185.1"),sQuery(id+"F0.wireOp",EDGE,"E16.185.2"),sQuery(id+"F0.wireOp",EDGE,"E16.185.3"),sQuery(id+"F0.wireOp",EDGE,"E16.185.4"),sQuery(id+"F0.wireOp",EDGE,"E16.186.0"),sQuery(id+"F0.wireOp",EDGE,"E16.186.1"),sQuery(id+"F0.wireOp",EDGE,"E16.186.2"),sQuery(id+"F0.wireOp",EDGE,"E16.186.3"),sQuery(id+"F0.wireOp",EDGE,"E16.186.4"),sQuery(id+"F0.wireOp",EDGE,"E16.187.0"),sQuery(id+"F0.wireOp",EDGE,"E16.187.1"),sQuery(id+"F0.wireOp",EDGE,"E16.187.2"),sQuery(id+"F0.wireOp",EDGE,"E16.187.3"),sQuery(id+"F0.wireOp",EDGE,"E16.187.4"),sQuery(id+"F0.wireOp",EDGE,"E16.188.0"),sQuery(id+"F0.wireOp",EDGE,"E16.188.1"),sQuery(id+"F0.wireOp",EDGE,"E16.188.2"),sQuery(id+"F0.wireOp",EDGE,"E16.188.3"),sQuery(id+"F0.wireOp",EDGE,"E16.188.4"),sQuery(id+"F0.wireOp",EDGE,"E16.189.0"),sQuery(id+"F0.wireOp",EDGE,"E16.189.1"),sQuery(id+"F0.wireOp",EDGE,"E16.189.2"),sQuery(id+"F0.wireOp",EDGE,"E16.189.3"),sQuery(id+"F0.wireOp",EDGE,"E16.189.4"),sQuery(id+"F0.wireOp",EDGE,"E16.190.0"),sQuery(id+"F0.wireOp",EDGE,"E16.190.1"),sQuery(id+"F0.wireOp",EDGE,"E16.190.2"),sQuery(id+"F0.wireOp",EDGE,"E16.190.3"),sQuery(id+"F0.wireOp",EDGE,"E16.190.4"),sQuery(id+"F0.wireOp",EDGE,"E16.191.0"),sQuery(id+"F0.wireOp",EDGE,"E16.191.1"),sQuery(id+"F0.wireOp",EDGE,"E16.191.2"),sQuery(id+"F0.wireOp",EDGE,"E16.191.3"),sQuery(id+"F0.wireOp",EDGE,"E16.191.4")])],"isStart":false});
            var sketch = newSketch(context, id + "F3", { "sketchPlane" : qUnion([Q0])});
            skArc(sketch, "E21.0", {"start": v(-89.73, 7) * mm, "mid": v(-90, 0) * mm, "end": v(-89.73, -7) * mm});
            skLineSegment(sketch, "E22", {"start": v(-28.77, 0) * mm, "end": v(-133.54, 0.01) * mm, "construction": true});
            skArc(sketch, "E23", {"start": v(-89.73, -7) * mm, "mid": v(-83, 0) * mm, "end": v(-89.73, 7) * mm});
            skSolve(sketch);
        }
        {
            var Q0;
            Q0 = qSketchRegion(id + "F3", true);
            extrude(context, id + "F4", {"entities" : qUnion([Q0]), "operationType" : NewBodyOperationType.ADD, "oppositeDirection" : true, "depth" : 20 * mm, "offsetDistance" : 25 * mm});
        }
        {
            var Q0;
            Q0=makeQuery(id+"F2.imprint","IMPRINT",FACE,{"disambiguationData":[TD([[makeQuery(id+"F2.imprint","IMPRINT",EDGE,{"derivedFrom":makeQuery(id+"F1.opExtrude","CAP_EDGE",EDGE,{"disambiguationData":[OSD([sQuery(id+"F0.wireOp",EDGE,"E0")])],"isStart":true})}),1.0]])]});
            var sketch = newSketch(context, id + "F5", { "sketchPlane" : qUnion([Q0])});
            skPoint(sketch, "E24.0", {"position": v(81.2, 38.8) * mm});
            skCircle(sketch, "E25", {"center": v(0, 0) * mm, "radius": 90 * mm, "construction": true});
            skPoint(sketch, "E26", {"position": v(90, 0) * mm});
            skSolve(sketch);
        }
        {
            var Q0;
            Q0=sQuery(id+"F5.wireOp",VERTEX,"E26");
            var Q1;
            Q1=makeQuery(id+"F1.opExtrude","SWEPT_BODY",BODY,{"disambiguationData":[OSD([sQuery(id+"F0.wireOp",EDGE,"E0"),sQuery(id+"F0.wireOp",EDGE,"E4"),sQuery(id+"F0.wireOp",EDGE,"E5"),sQuery(id+"F0.wireOp",EDGE,"E6.filletArc"),sQuery(id+"F0.wireOp",EDGE,"E7.MirrorCS"),sQuery(id+"F0.wireOp",EDGE,"E8.MirrorCS"),sQuery(id+"F0.wireOp",EDGE,"E15"),sQuery(id+"F0.wireOp",EDGE,"E16.1.0"),sQuery(id+"F0.wireOp",EDGE,"E16.1.1"),sQuery(id+"F0.wireOp",EDGE,"E16.1.2"),sQuery(id+"F0.wireOp",EDGE,"E16.1.3"),sQuery(id+"F0.wireOp",EDGE,"E16.1.4"),sQuery(id+"F0.wireOp",EDGE,"E16.2.0"),sQuery(id+"F0.wireOp",EDGE,"E16.2.1"),sQuery(id+"F0.wireOp",EDGE,"E16.2.2"),sQuery(id+"F0.wireOp",EDGE,"E16.2.3"),sQuery(id+"F0.wireOp",EDGE,"E16.2.4"),sQuery(id+"F0.wireOp",EDGE,"E16.3.0"),sQuery(id+"F0.wireOp",EDGE,"E16.3.1"),sQuery(id+"F0.wireOp",EDGE,"E16.3.2"),sQuery(id+"F0.wireOp",EDGE,"E16.3.3"),sQuery(id+"F0.wireOp",EDGE,"E16.3.4"),sQuery(id+"F0.wireOp",EDGE,"E16.4.0"),sQuery(id+"F0.wireOp",EDGE,"E16.4.1"),sQuery(id+"F0.wireOp",EDGE,"E16.4.2"),sQuery(id+"F0.wireOp",EDGE,"E16.4.3"),sQuery(id+"F0.wireOp",EDGE,"E16.4.4"),sQuery(id+"F0.wireOp",EDGE,"E16.5.0"),sQuery(id+"F0.wireOp",EDGE,"E16.5.1"),sQuery(id+"F0.wireOp",EDGE,"E16.5.2"),sQuery(id+"F0.wireOp",EDGE,"E16.5.3"),sQuery(id+"F0.wireOp",EDGE,"E16.5.4"),sQuery(id+"F0.wireOp",EDGE,"E16.6.0"),sQuery(id+"F0.wireOp",EDGE,"E16.6.1"),sQuery(id+"F0.wireOp",EDGE,"E16.6.2"),sQuery(id+"F0.wireOp",EDGE,"E16.6.3"),sQuery(id+"F0.wireOp",EDGE,"E16.6.4"),sQuery(id+"F0.wireOp",EDGE,"E16.7.0"),sQuery(id+"F0.wireOp",EDGE,"E16.7.1"),sQuery(id+"F0.wireOp",EDGE,"E16.7.2"),sQuery(id+"F0.wireOp",EDGE,"E16.7.3"),sQuery(id+"F0.wireOp",EDGE,"E16.7.4"),sQuery(id+"F0.wireOp",EDGE,"E16.8.0"),sQuery(id+"F0.wireOp",EDGE,"E16.8.1"),sQuery(id+"F0.wireOp",EDGE,"E16.8.2"),sQuery(id+"F0.wireOp",EDGE,"E16.8.3"),sQuery(id+"F0.wireOp",EDGE,"E16.8.4"),sQuery(id+"F0.wireOp",EDGE,"E16.9.0"),sQuery(id+"F0.wireOp",EDGE,"E16.9.1"),sQuery(id+"F0.wireOp",EDGE,"E16.9.2"),sQuery(id+"F0.wireOp",EDGE,"E16.9.3"),sQuery(id+"F0.wireOp",EDGE,"E16.9.4"),sQuery(id+"F0.wireOp",EDGE,"E16.10.0"),sQuery(id+"F0.wireOp",EDGE,"E16.10.1"),sQuery(id+"F0.wireOp",EDGE,"E16.10.2"),sQuery(id+"F0.wireOp",EDGE,"E16.10.3"),sQuery(id+"F0.wireOp",EDGE,"E16.10.4"),sQuery(id+"F0.wireOp",EDGE,"E16.11.0"),sQuery(id+"F0.wireOp",EDGE,"E16.11.1"),sQuery(id+"F0.wireOp",EDGE,"E16.11.2"),sQuery(id+"F0.wireOp",EDGE,"E16.11.3"),sQuery(id+"F0.wireOp",EDGE,"E16.11.4"),sQuery(id+"F0.wireOp",EDGE,"E16.12.0"),sQuery(id+"F0.wireOp",EDGE,"E16.12.1"),sQuery(id+"F0.wireOp",EDGE,"E16.12.2"),sQuery(id+"F0.wireOp",EDGE,"E16.12.3"),sQuery(id+"F0.wireOp",EDGE,"E16.12.4"),sQuery(id+"F0.wireOp",EDGE,"E16.13.0"),sQuery(id+"F0.wireOp",EDGE,"E16.13.1"),sQuery(id+"F0.wireOp",EDGE,"E16.13.2"),sQuery(id+"F0.wireOp",EDGE,"E16.13.3"),sQuery(id+"F0.wireOp",EDGE,"E16.13.4"),sQuery(id+"F0.wireOp",EDGE,"E16.14.0"),sQuery(id+"F0.wireOp",EDGE,"E16.14.1"),sQuery(id+"F0.wireOp",EDGE,"E16.14.2"),sQuery(id+"F0.wireOp",EDGE,"E16.14.3"),sQuery(id+"F0.wireOp",EDGE,"E16.14.4"),sQuery(id+"F0.wireOp",EDGE,"E16.15.0"),sQuery(id+"F0.wireOp",EDGE,"E16.15.1"),sQuery(id+"F0.wireOp",EDGE,"E16.15.2"),sQuery(id+"F0.wireOp",EDGE,"E16.15.3"),sQuery(id+"F0.wireOp",EDGE,"E16.15.4"),sQuery(id+"F0.wireOp",EDGE,"E16.16.0"),sQuery(id+"F0.wireOp",EDGE,"E16.16.1"),sQuery(id+"F0.wireOp",EDGE,"E16.16.2"),sQuery(id+"F0.wireOp",EDGE,"E16.16.3"),sQuery(id+"F0.wireOp",EDGE,"E16.16.4"),sQuery(id+"F0.wireOp",EDGE,"E16.17.0"),sQuery(id+"F0.wireOp",EDGE,"E16.17.1"),sQuery(id+"F0.wireOp",EDGE,"E16.17.2"),sQuery(id+"F0.wireOp",EDGE,"E16.17.3"),sQuery(id+"F0.wireOp",EDGE,"E16.17.4"),sQuery(id+"F0.wireOp",EDGE,"E16.18.0"),sQuery(id+"F0.wireOp",EDGE,"E16.18.1"),sQuery(id+"F0.wireOp",EDGE,"E16.18.2"),sQuery(id+"F0.wireOp",EDGE,"E16.18.3"),sQuery(id+"F0.wireOp",EDGE,"E16.18.4"),sQuery(id+"F0.wireOp",EDGE,"E16.19.0"),sQuery(id+"F0.wireOp",EDGE,"E16.19.1"),sQuery(id+"F0.wireOp",EDGE,"E16.19.2"),sQuery(id+"F0.wireOp",EDGE,"E16.19.3"),sQuery(id+"F0.wireOp",EDGE,"E16.19.4"),sQuery(id+"F0.wireOp",EDGE,"E16.20.0"),sQuery(id+"F0.wireOp",EDGE,"E16.20.1"),sQuery(id+"F0.wireOp",EDGE,"E16.20.2"),sQuery(id+"F0.wireOp",EDGE,"E16.20.3"),sQuery(id+"F0.wireOp",EDGE,"E16.20.4"),sQuery(id+"F0.wireOp",EDGE,"E16.21.0"),sQuery(id+"F0.wireOp",EDGE,"E16.21.1"),sQuery(id+"F0.wireOp",EDGE,"E16.21.2"),sQuery(id+"F0.wireOp",EDGE,"E16.21.3"),sQuery(id+"F0.wireOp",EDGE,"E16.21.4"),sQuery(id+"F0.wireOp",EDGE,"E16.22.0"),sQuery(id+"F0.wireOp",EDGE,"E16.22.1"),sQuery(id+"F0.wireOp",EDGE,"E16.22.2"),sQuery(id+"F0.wireOp",EDGE,"E16.22.3"),sQuery(id+"F0.wireOp",EDGE,"E16.22.4"),sQuery(id+"F0.wireOp",EDGE,"E16.23.0"),sQuery(id+"F0.wireOp",EDGE,"E16.23.1"),sQuery(id+"F0.wireOp",EDGE,"E16.23.2"),sQuery(id+"F0.wireOp",EDGE,"E16.23.3"),sQuery(id+"F0.wireOp",EDGE,"E16.23.4"),sQuery(id+"F0.wireOp",EDGE,"E16.24.0"),sQuery(id+"F0.wireOp",EDGE,"E16.24.1"),sQuery(id+"F0.wireOp",EDGE,"E16.24.2"),sQuery(id+"F0.wireOp",EDGE,"E16.24.3"),sQuery(id+"F0.wireOp",EDGE,"E16.24.4"),sQuery(id+"F0.wireOp",EDGE,"E16.25.0"),sQuery(id+"F0.wireOp",EDGE,"E16.25.1"),sQuery(id+"F0.wireOp",EDGE,"E16.25.2"),sQuery(id+"F0.wireOp",EDGE,"E16.25.3"),sQuery(id+"F0.wireOp",EDGE,"E16.25.4"),sQuery(id+"F0.wireOp",EDGE,"E16.26.0"),sQuery(id+"F0.wireOp",EDGE,"E16.26.1"),sQuery(id+"F0.wireOp",EDGE,"E16.26.2"),sQuery(id+"F0.wireOp",EDGE,"E16.26.3"),sQuery(id+"F0.wireOp",EDGE,"E16.26.4"),sQuery(id+"F0.wireOp",EDGE,"E16.27.0"),sQuery(id+"F0.wireOp",EDGE,"E16.27.1"),sQuery(id+"F0.wireOp",EDGE,"E16.27.2"),sQuery(id+"F0.wireOp",EDGE,"E16.27.3"),sQuery(id+"F0.wireOp",EDGE,"E16.27.4"),sQuery(id+"F0.wireOp",EDGE,"E16.28.0"),sQuery(id+"F0.wireOp",EDGE,"E16.28.1"),sQuery(id+"F0.wireOp",EDGE,"E16.28.2"),sQuery(id+"F0.wireOp",EDGE,"E16.28.3"),sQuery(id+"F0.wireOp",EDGE,"E16.28.4"),sQuery(id+"F0.wireOp",EDGE,"E16.29.0"),sQuery(id+"F0.wireOp",EDGE,"E16.29.1"),sQuery(id+"F0.wireOp",EDGE,"E16.29.2"),sQuery(id+"F0.wireOp",EDGE,"E16.29.3"),sQuery(id+"F0.wireOp",EDGE,"E16.29.4"),sQuery(id+"F0.wireOp",EDGE,"E16.30.0"),sQuery(id+"F0.wireOp",EDGE,"E16.30.1"),sQuery(id+"F0.wireOp",EDGE,"E16.30.2"),sQuery(id+"F0.wireOp",EDGE,"E16.30.3"),sQuery(id+"F0.wireOp",EDGE,"E16.30.4"),sQuery(id+"F0.wireOp",EDGE,"E16.31.0"),sQuery(id+"F0.wireOp",EDGE,"E16.31.1"),sQuery(id+"F0.wireOp",EDGE,"E16.31.2"),sQuery(id+"F0.wireOp",EDGE,"E16.31.3"),sQuery(id+"F0.wireOp",EDGE,"E16.31.4"),sQuery(id+"F0.wireOp",EDGE,"E16.32.0"),sQuery(id+"F0.wireOp",EDGE,"E16.32.1"),sQuery(id+"F0.wireOp",EDGE,"E16.32.2"),sQuery(id+"F0.wireOp",EDGE,"E16.32.3"),sQuery(id+"F0.wireOp",EDGE,"E16.32.4"),sQuery(id+"F0.wireOp",EDGE,"E16.33.0"),sQuery(id+"F0.wireOp",EDGE,"E16.33.1"),sQuery(id+"F0.wireOp",EDGE,"E16.33.2"),sQuery(id+"F0.wireOp",EDGE,"E16.33.3"),sQuery(id+"F0.wireOp",EDGE,"E16.33.4"),sQuery(id+"F0.wireOp",EDGE,"E16.34.0"),sQuery(id+"F0.wireOp",EDGE,"E16.34.1"),sQuery(id+"F0.wireOp",EDGE,"E16.34.2"),sQuery(id+"F0.wireOp",EDGE,"E16.34.3"),sQuery(id+"F0.wireOp",EDGE,"E16.34.4"),sQuery(id+"F0.wireOp",EDGE,"E16.35.0"),sQuery(id+"F0.wireOp",EDGE,"E16.35.1"),sQuery(id+"F0.wireOp",EDGE,"E16.35.2"),sQuery(id+"F0.wireOp",EDGE,"E16.35.3"),sQuery(id+"F0.wireOp",EDGE,"E16.35.4"),sQuery(id+"F0.wireOp",EDGE,"E16.36.0"),sQuery(id+"F0.wireOp",EDGE,"E16.36.1"),sQuery(id+"F0.wireOp",EDGE,"E16.36.2"),sQuery(id+"F0.wireOp",EDGE,"E16.36.3"),sQuery(id+"F0.wireOp",EDGE,"E16.36.4"),sQuery(id+"F0.wireOp",EDGE,"E16.37.0"),sQuery(id+"F0.wireOp",EDGE,"E16.37.1"),sQuery(id+"F0.wireOp",EDGE,"E16.37.2"),sQuery(id+"F0.wireOp",EDGE,"E16.37.3"),sQuery(id+"F0.wireOp",EDGE,"E16.37.4"),sQuery(id+"F0.wireOp",EDGE,"E16.38.0"),sQuery(id+"F0.wireOp",EDGE,"E16.38.1"),sQuery(id+"F0.wireOp",EDGE,"E16.38.2"),sQuery(id+"F0.wireOp",EDGE,"E16.38.3"),sQuery(id+"F0.wireOp",EDGE,"E16.38.4"),sQuery(id+"F0.wireOp",EDGE,"E16.39.0"),sQuery(id+"F0.wireOp",EDGE,"E16.39.1"),sQuery(id+"F0.wireOp",EDGE,"E16.39.2"),sQuery(id+"F0.wireOp",EDGE,"E16.39.3"),sQuery(id+"F0.wireOp",EDGE,"E16.39.4"),sQuery(id+"F0.wireOp",EDGE,"E16.40.0"),sQuery(id+"F0.wireOp",EDGE,"E16.40.1"),sQuery(id+"F0.wireOp",EDGE,"E16.40.2"),sQuery(id+"F0.wireOp",EDGE,"E16.40.3"),sQuery(id+"F0.wireOp",EDGE,"E16.40.4"),sQuery(id+"F0.wireOp",EDGE,"E16.41.0"),sQuery(id+"F0.wireOp",EDGE,"E16.41.1"),sQuery(id+"F0.wireOp",EDGE,"E16.41.2"),sQuery(id+"F0.wireOp",EDGE,"E16.41.3"),sQuery(id+"F0.wireOp",EDGE,"E16.41.4"),sQuery(id+"F0.wireOp",EDGE,"E16.42.0"),sQuery(id+"F0.wireOp",EDGE,"E16.42.1"),sQuery(id+"F0.wireOp",EDGE,"E16.42.2"),sQuery(id+"F0.wireOp",EDGE,"E16.42.3"),sQuery(id+"F0.wireOp",EDGE,"E16.42.4"),sQuery(id+"F0.wireOp",EDGE,"E16.43.0"),sQuery(id+"F0.wireOp",EDGE,"E16.43.1"),sQuery(id+"F0.wireOp",EDGE,"E16.43.2"),sQuery(id+"F0.wireOp",EDGE,"E16.43.3"),sQuery(id+"F0.wireOp",EDGE,"E16.43.4"),sQuery(id+"F0.wireOp",EDGE,"E16.44.0"),sQuery(id+"F0.wireOp",EDGE,"E16.44.1"),sQuery(id+"F0.wireOp",EDGE,"E16.44.2"),sQuery(id+"F0.wireOp",EDGE,"E16.44.3"),sQuery(id+"F0.wireOp",EDGE,"E16.44.4"),sQuery(id+"F0.wireOp",EDGE,"E16.45.0"),sQuery(id+"F0.wireOp",EDGE,"E16.45.1"),sQuery(id+"F0.wireOp",EDGE,"E16.45.2"),sQuery(id+"F0.wireOp",EDGE,"E16.45.3"),sQuery(id+"F0.wireOp",EDGE,"E16.45.4"),sQuery(id+"F0.wireOp",EDGE,"E16.46.0"),sQuery(id+"F0.wireOp",EDGE,"E16.46.1"),sQuery(id+"F0.wireOp",EDGE,"E16.46.2"),sQuery(id+"F0.wireOp",EDGE,"E16.46.3"),sQuery(id+"F0.wireOp",EDGE,"E16.46.4"),sQuery(id+"F0.wireOp",EDGE,"E16.47.0"),sQuery(id+"F0.wireOp",EDGE,"E16.47.1"),sQuery(id+"F0.wireOp",EDGE,"E16.47.2"),sQuery(id+"F0.wireOp",EDGE,"E16.47.3"),sQuery(id+"F0.wireOp",EDGE,"E16.47.4"),sQuery(id+"F0.wireOp",EDGE,"E16.48.0"),sQuery(id+"F0.wireOp",EDGE,"E16.48.1"),sQuery(id+"F0.wireOp",EDGE,"E16.48.2"),sQuery(id+"F0.wireOp",EDGE,"E16.48.3"),sQuery(id+"F0.wireOp",EDGE,"E16.48.4"),sQuery(id+"F0.wireOp",EDGE,"E16.49.0"),sQuery(id+"F0.wireOp",EDGE,"E16.49.1"),sQuery(id+"F0.wireOp",EDGE,"E16.49.2"),sQuery(id+"F0.wireOp",EDGE,"E16.49.3"),sQuery(id+"F0.wireOp",EDGE,"E16.49.4"),sQuery(id+"F0.wireOp",EDGE,"E16.50.0"),sQuery(id+"F0.wireOp",EDGE,"E16.50.1"),sQuery(id+"F0.wireOp",EDGE,"E16.50.2"),sQuery(id+"F0.wireOp",EDGE,"E16.50.3"),sQuery(id+"F0.wireOp",EDGE,"E16.50.4"),sQuery(id+"F0.wireOp",EDGE,"E16.51.0"),sQuery(id+"F0.wireOp",EDGE,"E16.51.1"),sQuery(id+"F0.wireOp",EDGE,"E16.51.2"),sQuery(id+"F0.wireOp",EDGE,"E16.51.3"),sQuery(id+"F0.wireOp",EDGE,"E16.51.4"),sQuery(id+"F0.wireOp",EDGE,"E16.52.0"),sQuery(id+"F0.wireOp",EDGE,"E16.52.1"),sQuery(id+"F0.wireOp",EDGE,"E16.52.2"),sQuery(id+"F0.wireOp",EDGE,"E16.52.3"),sQuery(id+"F0.wireOp",EDGE,"E16.52.4"),sQuery(id+"F0.wireOp",EDGE,"E16.53.0"),sQuery(id+"F0.wireOp",EDGE,"E16.53.1"),sQuery(id+"F0.wireOp",EDGE,"E16.53.2"),sQuery(id+"F0.wireOp",EDGE,"E16.53.3"),sQuery(id+"F0.wireOp",EDGE,"E16.53.4"),sQuery(id+"F0.wireOp",EDGE,"E16.54.0"),sQuery(id+"F0.wireOp",EDGE,"E16.54.1"),sQuery(id+"F0.wireOp",EDGE,"E16.54.2"),sQuery(id+"F0.wireOp",EDGE,"E16.54.3"),sQuery(id+"F0.wireOp",EDGE,"E16.54.4"),sQuery(id+"F0.wireOp",EDGE,"E16.55.0"),sQuery(id+"F0.wireOp",EDGE,"E16.55.1"),sQuery(id+"F0.wireOp",EDGE,"E16.55.2"),sQuery(id+"F0.wireOp",EDGE,"E16.55.3"),sQuery(id+"F0.wireOp",EDGE,"E16.55.4"),sQuery(id+"F0.wireOp",EDGE,"E16.56.0"),sQuery(id+"F0.wireOp",EDGE,"E16.56.1"),sQuery(id+"F0.wireOp",EDGE,"E16.56.2"),sQuery(id+"F0.wireOp",EDGE,"E16.56.3"),sQuery(id+"F0.wireOp",EDGE,"E16.56.4"),sQuery(id+"F0.wireOp",EDGE,"E16.57.0"),sQuery(id+"F0.wireOp",EDGE,"E16.57.1"),sQuery(id+"F0.wireOp",EDGE,"E16.57.2"),sQuery(id+"F0.wireOp",EDGE,"E16.57.3"),sQuery(id+"F0.wireOp",EDGE,"E16.57.4"),sQuery(id+"F0.wireOp",EDGE,"E16.58.0"),sQuery(id+"F0.wireOp",EDGE,"E16.58.1"),sQuery(id+"F0.wireOp",EDGE,"E16.58.2"),sQuery(id+"F0.wireOp",EDGE,"E16.58.3"),sQuery(id+"F0.wireOp",EDGE,"E16.58.4"),sQuery(id+"F0.wireOp",EDGE,"E16.59.0"),sQuery(id+"F0.wireOp",EDGE,"E16.59.1"),sQuery(id+"F0.wireOp",EDGE,"E16.59.2"),sQuery(id+"F0.wireOp",EDGE,"E16.59.3"),sQuery(id+"F0.wireOp",EDGE,"E16.59.4"),sQuery(id+"F0.wireOp",EDGE,"E16.60.0"),sQuery(id+"F0.wireOp",EDGE,"E16.60.1"),sQuery(id+"F0.wireOp",EDGE,"E16.60.2"),sQuery(id+"F0.wireOp",EDGE,"E16.60.3"),sQuery(id+"F0.wireOp",EDGE,"E16.60.4"),sQuery(id+"F0.wireOp",EDGE,"E16.61.0"),sQuery(id+"F0.wireOp",EDGE,"E16.61.1"),sQuery(id+"F0.wireOp",EDGE,"E16.61.2"),sQuery(id+"F0.wireOp",EDGE,"E16.61.3"),sQuery(id+"F0.wireOp",EDGE,"E16.61.4"),sQuery(id+"F0.wireOp",EDGE,"E16.62.0"),sQuery(id+"F0.wireOp",EDGE,"E16.62.1"),sQuery(id+"F0.wireOp",EDGE,"E16.62.2"),sQuery(id+"F0.wireOp",EDGE,"E16.62.3"),sQuery(id+"F0.wireOp",EDGE,"E16.62.4"),sQuery(id+"F0.wireOp",EDGE,"E16.63.0"),sQuery(id+"F0.wireOp",EDGE,"E16.63.1"),sQuery(id+"F0.wireOp",EDGE,"E16.63.2"),sQuery(id+"F0.wireOp",EDGE,"E16.63.3"),sQuery(id+"F0.wireOp",EDGE,"E16.63.4"),sQuery(id+"F0.wireOp",EDGE,"E16.64.0"),sQuery(id+"F0.wireOp",EDGE,"E16.64.1"),sQuery(id+"F0.wireOp",EDGE,"E16.64.2"),sQuery(id+"F0.wireOp",EDGE,"E16.64.3"),sQuery(id+"F0.wireOp",EDGE,"E16.64.4"),sQuery(id+"F0.wireOp",EDGE,"E16.65.0"),sQuery(id+"F0.wireOp",EDGE,"E16.65.1"),sQuery(id+"F0.wireOp",EDGE,"E16.65.2"),sQuery(id+"F0.wireOp",EDGE,"E16.65.3"),sQuery(id+"F0.wireOp",EDGE,"E16.65.4"),sQuery(id+"F0.wireOp",EDGE,"E16.66.0"),sQuery(id+"F0.wireOp",EDGE,"E16.66.1"),sQuery(id+"F0.wireOp",EDGE,"E16.66.2"),sQuery(id+"F0.wireOp",EDGE,"E16.66.3"),sQuery(id+"F0.wireOp",EDGE,"E16.66.4"),sQuery(id+"F0.wireOp",EDGE,"E16.67.0"),sQuery(id+"F0.wireOp",EDGE,"E16.67.1"),sQuery(id+"F0.wireOp",EDGE,"E16.67.2"),sQuery(id+"F0.wireOp",EDGE,"E16.67.3"),sQuery(id+"F0.wireOp",EDGE,"E16.67.4"),sQuery(id+"F0.wireOp",EDGE,"E16.68.0"),sQuery(id+"F0.wireOp",EDGE,"E16.68.1"),sQuery(id+"F0.wireOp",EDGE,"E16.68.2"),sQuery(id+"F0.wireOp",EDGE,"E16.68.3"),sQuery(id+"F0.wireOp",EDGE,"E16.68.4"),sQuery(id+"F0.wireOp",EDGE,"E16.69.0"),sQuery(id+"F0.wireOp",EDGE,"E16.69.1"),sQuery(id+"F0.wireOp",EDGE,"E16.69.2"),sQuery(id+"F0.wireOp",EDGE,"E16.69.3"),sQuery(id+"F0.wireOp",EDGE,"E16.69.4"),sQuery(id+"F0.wireOp",EDGE,"E16.70.0"),sQuery(id+"F0.wireOp",EDGE,"E16.70.1"),sQuery(id+"F0.wireOp",EDGE,"E16.70.2"),sQuery(id+"F0.wireOp",EDGE,"E16.70.3"),sQuery(id+"F0.wireOp",EDGE,"E16.70.4"),sQuery(id+"F0.wireOp",EDGE,"E16.71.0"),sQuery(id+"F0.wireOp",EDGE,"E16.71.1"),sQuery(id+"F0.wireOp",EDGE,"E16.71.2"),sQuery(id+"F0.wireOp",EDGE,"E16.71.3"),sQuery(id+"F0.wireOp",EDGE,"E16.71.4"),sQuery(id+"F0.wireOp",EDGE,"E16.72.0"),sQuery(id+"F0.wireOp",EDGE,"E16.72.1"),sQuery(id+"F0.wireOp",EDGE,"E16.72.2"),sQuery(id+"F0.wireOp",EDGE,"E16.72.3"),sQuery(id+"F0.wireOp",EDGE,"E16.72.4"),sQuery(id+"F0.wireOp",EDGE,"E16.73.0"),sQuery(id+"F0.wireOp",EDGE,"E16.73.1"),sQuery(id+"F0.wireOp",EDGE,"E16.73.2"),sQuery(id+"F0.wireOp",EDGE,"E16.73.3"),sQuery(id+"F0.wireOp",EDGE,"E16.73.4"),sQuery(id+"F0.wireOp",EDGE,"E16.74.0"),sQuery(id+"F0.wireOp",EDGE,"E16.74.1"),sQuery(id+"F0.wireOp",EDGE,"E16.74.2"),sQuery(id+"F0.wireOp",EDGE,"E16.74.3"),sQuery(id+"F0.wireOp",EDGE,"E16.74.4"),sQuery(id+"F0.wireOp",EDGE,"E16.75.0"),sQuery(id+"F0.wireOp",EDGE,"E16.75.1"),sQuery(id+"F0.wireOp",EDGE,"E16.75.2"),sQuery(id+"F0.wireOp",EDGE,"E16.75.3"),sQuery(id+"F0.wireOp",EDGE,"E16.75.4"),sQuery(id+"F0.wireOp",EDGE,"E16.76.0"),sQuery(id+"F0.wireOp",EDGE,"E16.76.1"),sQuery(id+"F0.wireOp",EDGE,"E16.76.2"),sQuery(id+"F0.wireOp",EDGE,"E16.76.3"),sQuery(id+"F0.wireOp",EDGE,"E16.76.4"),sQuery(id+"F0.wireOp",EDGE,"E16.77.0"),sQuery(id+"F0.wireOp",EDGE,"E16.77.1"),sQuery(id+"F0.wireOp",EDGE,"E16.77.2"),sQuery(id+"F0.wireOp",EDGE,"E16.77.3"),sQuery(id+"F0.wireOp",EDGE,"E16.77.4"),sQuery(id+"F0.wireOp",EDGE,"E16.78.0"),sQuery(id+"F0.wireOp",EDGE,"E16.78.1"),sQuery(id+"F0.wireOp",EDGE,"E16.78.2"),sQuery(id+"F0.wireOp",EDGE,"E16.78.3"),sQuery(id+"F0.wireOp",EDGE,"E16.78.4"),sQuery(id+"F0.wireOp",EDGE,"E16.79.0"),sQuery(id+"F0.wireOp",EDGE,"E16.79.1"),sQuery(id+"F0.wireOp",EDGE,"E16.79.2"),sQuery(id+"F0.wireOp",EDGE,"E16.79.3"),sQuery(id+"F0.wireOp",EDGE,"E16.79.4"),sQuery(id+"F0.wireOp",EDGE,"E16.80.0"),sQuery(id+"F0.wireOp",EDGE,"E16.80.1"),sQuery(id+"F0.wireOp",EDGE,"E16.80.2"),sQuery(id+"F0.wireOp",EDGE,"E16.80.3"),sQuery(id+"F0.wireOp",EDGE,"E16.80.4"),sQuery(id+"F0.wireOp",EDGE,"E16.81.0"),sQuery(id+"F0.wireOp",EDGE,"E16.81.1"),sQuery(id+"F0.wireOp",EDGE,"E16.81.2"),sQuery(id+"F0.wireOp",EDGE,"E16.81.3"),sQuery(id+"F0.wireOp",EDGE,"E16.81.4"),sQuery(id+"F0.wireOp",EDGE,"E16.82.0"),sQuery(id+"F0.wireOp",EDGE,"E16.82.1"),sQuery(id+"F0.wireOp",EDGE,"E16.82.2"),sQuery(id+"F0.wireOp",EDGE,"E16.82.3"),sQuery(id+"F0.wireOp",EDGE,"E16.82.4"),sQuery(id+"F0.wireOp",EDGE,"E16.83.0"),sQuery(id+"F0.wireOp",EDGE,"E16.83.1"),sQuery(id+"F0.wireOp",EDGE,"E16.83.2"),sQuery(id+"F0.wireOp",EDGE,"E16.83.3"),sQuery(id+"F0.wireOp",EDGE,"E16.83.4"),sQuery(id+"F0.wireOp",EDGE,"E16.84.0"),sQuery(id+"F0.wireOp",EDGE,"E16.84.1"),sQuery(id+"F0.wireOp",EDGE,"E16.84.2"),sQuery(id+"F0.wireOp",EDGE,"E16.84.3"),sQuery(id+"F0.wireOp",EDGE,"E16.84.4"),sQuery(id+"F0.wireOp",EDGE,"E16.85.0"),sQuery(id+"F0.wireOp",EDGE,"E16.85.1"),sQuery(id+"F0.wireOp",EDGE,"E16.85.2"),sQuery(id+"F0.wireOp",EDGE,"E16.85.3"),sQuery(id+"F0.wireOp",EDGE,"E16.85.4"),sQuery(id+"F0.wireOp",EDGE,"E16.86.0"),sQuery(id+"F0.wireOp",EDGE,"E16.86.1"),sQuery(id+"F0.wireOp",EDGE,"E16.86.2"),sQuery(id+"F0.wireOp",EDGE,"E16.86.3"),sQuery(id+"F0.wireOp",EDGE,"E16.86.4"),sQuery(id+"F0.wireOp",EDGE,"E16.87.0"),sQuery(id+"F0.wireOp",EDGE,"E16.87.1"),sQuery(id+"F0.wireOp",EDGE,"E16.87.2"),sQuery(id+"F0.wireOp",EDGE,"E16.87.3"),sQuery(id+"F0.wireOp",EDGE,"E16.87.4"),sQuery(id+"F0.wireOp",EDGE,"E16.88.0"),sQuery(id+"F0.wireOp",EDGE,"E16.88.1"),sQuery(id+"F0.wireOp",EDGE,"E16.88.2"),sQuery(id+"F0.wireOp",EDGE,"E16.88.3"),sQuery(id+"F0.wireOp",EDGE,"E16.88.4"),sQuery(id+"F0.wireOp",EDGE,"E16.89.0"),sQuery(id+"F0.wireOp",EDGE,"E16.89.1"),sQuery(id+"F0.wireOp",EDGE,"E16.89.2"),sQuery(id+"F0.wireOp",EDGE,"E16.89.3"),sQuery(id+"F0.wireOp",EDGE,"E16.89.4"),sQuery(id+"F0.wireOp",EDGE,"E16.90.0"),sQuery(id+"F0.wireOp",EDGE,"E16.90.1"),sQuery(id+"F0.wireOp",EDGE,"E16.90.2"),sQuery(id+"F0.wireOp",EDGE,"E16.90.3"),sQuery(id+"F0.wireOp",EDGE,"E16.90.4"),sQuery(id+"F0.wireOp",EDGE,"E16.91.0"),sQuery(id+"F0.wireOp",EDGE,"E16.91.1"),sQuery(id+"F0.wireOp",EDGE,"E16.91.2"),sQuery(id+"F0.wireOp",EDGE,"E16.91.3"),sQuery(id+"F0.wireOp",EDGE,"E16.91.4"),sQuery(id+"F0.wireOp",EDGE,"E16.92.0"),sQuery(id+"F0.wireOp",EDGE,"E16.92.1"),sQuery(id+"F0.wireOp",EDGE,"E16.92.2"),sQuery(id+"F0.wireOp",EDGE,"E16.92.3"),sQuery(id+"F0.wireOp",EDGE,"E16.92.4"),sQuery(id+"F0.wireOp",EDGE,"E16.93.0"),sQuery(id+"F0.wireOp",EDGE,"E16.93.1"),sQuery(id+"F0.wireOp",EDGE,"E16.93.2"),sQuery(id+"F0.wireOp",EDGE,"E16.93.3"),sQuery(id+"F0.wireOp",EDGE,"E16.93.4"),sQuery(id+"F0.wireOp",EDGE,"E16.94.0"),sQuery(id+"F0.wireOp",EDGE,"E16.94.1"),sQuery(id+"F0.wireOp",EDGE,"E16.94.2"),sQuery(id+"F0.wireOp",EDGE,"E16.94.3"),sQuery(id+"F0.wireOp",EDGE,"E16.94.4"),sQuery(id+"F0.wireOp",EDGE,"E16.95.0"),sQuery(id+"F0.wireOp",EDGE,"E16.95.1"),sQuery(id+"F0.wireOp",EDGE,"E16.95.2"),sQuery(id+"F0.wireOp",EDGE,"E16.95.3"),sQuery(id+"F0.wireOp",EDGE,"E16.95.4"),sQuery(id+"F0.wireOp",EDGE,"E16.96.0"),sQuery(id+"F0.wireOp",EDGE,"E16.96.1"),sQuery(id+"F0.wireOp",EDGE,"E16.96.2"),sQuery(id+"F0.wireOp",EDGE,"E16.96.3"),sQuery(id+"F0.wireOp",EDGE,"E16.96.4"),sQuery(id+"F0.wireOp",EDGE,"E16.97.0"),sQuery(id+"F0.wireOp",EDGE,"E16.97.1"),sQuery(id+"F0.wireOp",EDGE,"E16.97.2"),sQuery(id+"F0.wireOp",EDGE,"E16.97.3"),sQuery(id+"F0.wireOp",EDGE,"E16.97.4"),sQuery(id+"F0.wireOp",EDGE,"E16.98.0"),sQuery(id+"F0.wireOp",EDGE,"E16.98.1"),sQuery(id+"F0.wireOp",EDGE,"E16.98.2"),sQuery(id+"F0.wireOp",EDGE,"E16.98.3"),sQuery(id+"F0.wireOp",EDGE,"E16.98.4"),sQuery(id+"F0.wireOp",EDGE,"E16.99.0"),sQuery(id+"F0.wireOp",EDGE,"E16.99.1"),sQuery(id+"F0.wireOp",EDGE,"E16.99.2"),sQuery(id+"F0.wireOp",EDGE,"E16.99.3"),sQuery(id+"F0.wireOp",EDGE,"E16.99.4"),sQuery(id+"F0.wireOp",EDGE,"E16.100.0"),sQuery(id+"F0.wireOp",EDGE,"E16.100.1"),sQuery(id+"F0.wireOp",EDGE,"E16.100.2"),sQuery(id+"F0.wireOp",EDGE,"E16.100.3"),sQuery(id+"F0.wireOp",EDGE,"E16.100.4"),sQuery(id+"F0.wireOp",EDGE,"E16.101.0"),sQuery(id+"F0.wireOp",EDGE,"E16.101.1"),sQuery(id+"F0.wireOp",EDGE,"E16.101.2"),sQuery(id+"F0.wireOp",EDGE,"E16.101.3"),sQuery(id+"F0.wireOp",EDGE,"E16.101.4"),sQuery(id+"F0.wireOp",EDGE,"E16.102.0"),sQuery(id+"F0.wireOp",EDGE,"E16.102.1"),sQuery(id+"F0.wireOp",EDGE,"E16.102.2"),sQuery(id+"F0.wireOp",EDGE,"E16.102.3"),sQuery(id+"F0.wireOp",EDGE,"E16.102.4"),sQuery(id+"F0.wireOp",EDGE,"E16.103.0"),sQuery(id+"F0.wireOp",EDGE,"E16.103.1"),sQuery(id+"F0.wireOp",EDGE,"E16.103.2"),sQuery(id+"F0.wireOp",EDGE,"E16.103.3"),sQuery(id+"F0.wireOp",EDGE,"E16.103.4"),sQuery(id+"F0.wireOp",EDGE,"E16.104.0"),sQuery(id+"F0.wireOp",EDGE,"E16.104.1"),sQuery(id+"F0.wireOp",EDGE,"E16.104.2"),sQuery(id+"F0.wireOp",EDGE,"E16.104.3"),sQuery(id+"F0.wireOp",EDGE,"E16.104.4"),sQuery(id+"F0.wireOp",EDGE,"E16.105.0"),sQuery(id+"F0.wireOp",EDGE,"E16.105.1"),sQuery(id+"F0.wireOp",EDGE,"E16.105.2"),sQuery(id+"F0.wireOp",EDGE,"E16.105.3"),sQuery(id+"F0.wireOp",EDGE,"E16.105.4"),sQuery(id+"F0.wireOp",EDGE,"E16.106.0"),sQuery(id+"F0.wireOp",EDGE,"E16.106.1"),sQuery(id+"F0.wireOp",EDGE,"E16.106.2"),sQuery(id+"F0.wireOp",EDGE,"E16.106.3"),sQuery(id+"F0.wireOp",EDGE,"E16.106.4"),sQuery(id+"F0.wireOp",EDGE,"E16.107.0"),sQuery(id+"F0.wireOp",EDGE,"E16.107.1"),sQuery(id+"F0.wireOp",EDGE,"E16.107.2"),sQuery(id+"F0.wireOp",EDGE,"E16.107.3"),sQuery(id+"F0.wireOp",EDGE,"E16.107.4"),sQuery(id+"F0.wireOp",EDGE,"E16.108.0"),sQuery(id+"F0.wireOp",EDGE,"E16.108.1"),sQuery(id+"F0.wireOp",EDGE,"E16.108.2"),sQuery(id+"F0.wireOp",EDGE,"E16.108.3"),sQuery(id+"F0.wireOp",EDGE,"E16.108.4"),sQuery(id+"F0.wireOp",EDGE,"E16.109.0"),sQuery(id+"F0.wireOp",EDGE,"E16.109.1"),sQuery(id+"F0.wireOp",EDGE,"E16.109.2"),sQuery(id+"F0.wireOp",EDGE,"E16.109.3"),sQuery(id+"F0.wireOp",EDGE,"E16.109.4"),sQuery(id+"F0.wireOp",EDGE,"E16.110.0"),sQuery(id+"F0.wireOp",EDGE,"E16.110.1"),sQuery(id+"F0.wireOp",EDGE,"E16.110.2"),sQuery(id+"F0.wireOp",EDGE,"E16.110.3"),sQuery(id+"F0.wireOp",EDGE,"E16.110.4"),sQuery(id+"F0.wireOp",EDGE,"E16.111.0"),sQuery(id+"F0.wireOp",EDGE,"E16.111.1"),sQuery(id+"F0.wireOp",EDGE,"E16.111.2"),sQuery(id+"F0.wireOp",EDGE,"E16.111.3"),sQuery(id+"F0.wireOp",EDGE,"E16.111.4"),sQuery(id+"F0.wireOp",EDGE,"E16.112.0"),sQuery(id+"F0.wireOp",EDGE,"E16.112.1"),sQuery(id+"F0.wireOp",EDGE,"E16.112.2"),sQuery(id+"F0.wireOp",EDGE,"E16.112.3"),sQuery(id+"F0.wireOp",EDGE,"E16.112.4"),sQuery(id+"F0.wireOp",EDGE,"E16.113.0"),sQuery(id+"F0.wireOp",EDGE,"E16.113.1"),sQuery(id+"F0.wireOp",EDGE,"E16.113.2"),sQuery(id+"F0.wireOp",EDGE,"E16.113.3"),sQuery(id+"F0.wireOp",EDGE,"E16.113.4"),sQuery(id+"F0.wireOp",EDGE,"E16.114.0"),sQuery(id+"F0.wireOp",EDGE,"E16.114.1"),sQuery(id+"F0.wireOp",EDGE,"E16.114.2"),sQuery(id+"F0.wireOp",EDGE,"E16.114.3"),sQuery(id+"F0.wireOp",EDGE,"E16.114.4"),sQuery(id+"F0.wireOp",EDGE,"E16.115.0"),sQuery(id+"F0.wireOp",EDGE,"E16.115.1"),sQuery(id+"F0.wireOp",EDGE,"E16.115.2"),sQuery(id+"F0.wireOp",EDGE,"E16.115.3"),sQuery(id+"F0.wireOp",EDGE,"E16.115.4"),sQuery(id+"F0.wireOp",EDGE,"E16.116.0"),sQuery(id+"F0.wireOp",EDGE,"E16.116.1"),sQuery(id+"F0.wireOp",EDGE,"E16.116.2"),sQuery(id+"F0.wireOp",EDGE,"E16.116.3"),sQuery(id+"F0.wireOp",EDGE,"E16.116.4"),sQuery(id+"F0.wireOp",EDGE,"E16.117.0"),sQuery(id+"F0.wireOp",EDGE,"E16.117.1"),sQuery(id+"F0.wireOp",EDGE,"E16.117.2"),sQuery(id+"F0.wireOp",EDGE,"E16.117.3"),sQuery(id+"F0.wireOp",EDGE,"E16.117.4"),sQuery(id+"F0.wireOp",EDGE,"E16.118.0"),sQuery(id+"F0.wireOp",EDGE,"E16.118.1"),sQuery(id+"F0.wireOp",EDGE,"E16.118.2"),sQuery(id+"F0.wireOp",EDGE,"E16.118.3"),sQuery(id+"F0.wireOp",EDGE,"E16.118.4"),sQuery(id+"F0.wireOp",EDGE,"E16.119.0"),sQuery(id+"F0.wireOp",EDGE,"E16.119.1"),sQuery(id+"F0.wireOp",EDGE,"E16.119.2"),sQuery(id+"F0.wireOp",EDGE,"E16.119.3"),sQuery(id+"F0.wireOp",EDGE,"E16.119.4"),sQuery(id+"F0.wireOp",EDGE,"E16.120.0"),sQuery(id+"F0.wireOp",EDGE,"E16.120.1"),sQuery(id+"F0.wireOp",EDGE,"E16.120.2"),sQuery(id+"F0.wireOp",EDGE,"E16.120.3"),sQuery(id+"F0.wireOp",EDGE,"E16.120.4"),sQuery(id+"F0.wireOp",EDGE,"E16.121.0"),sQuery(id+"F0.wireOp",EDGE,"E16.121.1"),sQuery(id+"F0.wireOp",EDGE,"E16.121.2"),sQuery(id+"F0.wireOp",EDGE,"E16.121.3"),sQuery(id+"F0.wireOp",EDGE,"E16.121.4"),sQuery(id+"F0.wireOp",EDGE,"E16.122.0"),sQuery(id+"F0.wireOp",EDGE,"E16.122.1"),sQuery(id+"F0.wireOp",EDGE,"E16.122.2"),sQuery(id+"F0.wireOp",EDGE,"E16.122.3"),sQuery(id+"F0.wireOp",EDGE,"E16.122.4"),sQuery(id+"F0.wireOp",EDGE,"E16.123.0"),sQuery(id+"F0.wireOp",EDGE,"E16.123.1"),sQuery(id+"F0.wireOp",EDGE,"E16.123.2"),sQuery(id+"F0.wireOp",EDGE,"E16.123.3"),sQuery(id+"F0.wireOp",EDGE,"E16.123.4"),sQuery(id+"F0.wireOp",EDGE,"E16.124.0"),sQuery(id+"F0.wireOp",EDGE,"E16.124.1"),sQuery(id+"F0.wireOp",EDGE,"E16.124.2"),sQuery(id+"F0.wireOp",EDGE,"E16.124.3"),sQuery(id+"F0.wireOp",EDGE,"E16.124.4"),sQuery(id+"F0.wireOp",EDGE,"E16.125.0"),sQuery(id+"F0.wireOp",EDGE,"E16.125.1"),sQuery(id+"F0.wireOp",EDGE,"E16.125.2"),sQuery(id+"F0.wireOp",EDGE,"E16.125.3"),sQuery(id+"F0.wireOp",EDGE,"E16.125.4"),sQuery(id+"F0.wireOp",EDGE,"E16.126.0"),sQuery(id+"F0.wireOp",EDGE,"E16.126.1"),sQuery(id+"F0.wireOp",EDGE,"E16.126.2"),sQuery(id+"F0.wireOp",EDGE,"E16.126.3"),sQuery(id+"F0.wireOp",EDGE,"E16.126.4"),sQuery(id+"F0.wireOp",EDGE,"E16.127.0"),sQuery(id+"F0.wireOp",EDGE,"E16.127.1"),sQuery(id+"F0.wireOp",EDGE,"E16.127.2"),sQuery(id+"F0.wireOp",EDGE,"E16.127.3"),sQuery(id+"F0.wireOp",EDGE,"E16.127.4"),sQuery(id+"F0.wireOp",EDGE,"E16.128.0"),sQuery(id+"F0.wireOp",EDGE,"E16.128.1"),sQuery(id+"F0.wireOp",EDGE,"E16.128.2"),sQuery(id+"F0.wireOp",EDGE,"E16.128.3"),sQuery(id+"F0.wireOp",EDGE,"E16.128.4"),sQuery(id+"F0.wireOp",EDGE,"E16.129.0"),sQuery(id+"F0.wireOp",EDGE,"E16.129.1"),sQuery(id+"F0.wireOp",EDGE,"E16.129.2"),sQuery(id+"F0.wireOp",EDGE,"E16.129.3"),sQuery(id+"F0.wireOp",EDGE,"E16.129.4"),sQuery(id+"F0.wireOp",EDGE,"E16.130.0"),sQuery(id+"F0.wireOp",EDGE,"E16.130.1"),sQuery(id+"F0.wireOp",EDGE,"E16.130.2"),sQuery(id+"F0.wireOp",EDGE,"E16.130.3"),sQuery(id+"F0.wireOp",EDGE,"E16.130.4"),sQuery(id+"F0.wireOp",EDGE,"E16.131.0"),sQuery(id+"F0.wireOp",EDGE,"E16.131.1"),sQuery(id+"F0.wireOp",EDGE,"E16.131.2"),sQuery(id+"F0.wireOp",EDGE,"E16.131.3"),sQuery(id+"F0.wireOp",EDGE,"E16.131.4"),sQuery(id+"F0.wireOp",EDGE,"E16.132.0"),sQuery(id+"F0.wireOp",EDGE,"E16.132.1"),sQuery(id+"F0.wireOp",EDGE,"E16.132.2"),sQuery(id+"F0.wireOp",EDGE,"E16.132.3"),sQuery(id+"F0.wireOp",EDGE,"E16.132.4"),sQuery(id+"F0.wireOp",EDGE,"E16.133.0"),sQuery(id+"F0.wireOp",EDGE,"E16.133.1"),sQuery(id+"F0.wireOp",EDGE,"E16.133.2"),sQuery(id+"F0.wireOp",EDGE,"E16.133.3"),sQuery(id+"F0.wireOp",EDGE,"E16.133.4"),sQuery(id+"F0.wireOp",EDGE,"E16.134.0"),sQuery(id+"F0.wireOp",EDGE,"E16.134.1"),sQuery(id+"F0.wireOp",EDGE,"E16.134.2"),sQuery(id+"F0.wireOp",EDGE,"E16.134.3"),sQuery(id+"F0.wireOp",EDGE,"E16.134.4"),sQuery(id+"F0.wireOp",EDGE,"E16.135.0"),sQuery(id+"F0.wireOp",EDGE,"E16.135.1"),sQuery(id+"F0.wireOp",EDGE,"E16.135.2"),sQuery(id+"F0.wireOp",EDGE,"E16.135.3"),sQuery(id+"F0.wireOp",EDGE,"E16.135.4"),sQuery(id+"F0.wireOp",EDGE,"E16.136.0"),sQuery(id+"F0.wireOp",EDGE,"E16.136.1"),sQuery(id+"F0.wireOp",EDGE,"E16.136.2"),sQuery(id+"F0.wireOp",EDGE,"E16.136.3"),sQuery(id+"F0.wireOp",EDGE,"E16.136.4"),sQuery(id+"F0.wireOp",EDGE,"E16.137.0"),sQuery(id+"F0.wireOp",EDGE,"E16.137.1"),sQuery(id+"F0.wireOp",EDGE,"E16.137.2"),sQuery(id+"F0.wireOp",EDGE,"E16.137.3"),sQuery(id+"F0.wireOp",EDGE,"E16.137.4"),sQuery(id+"F0.wireOp",EDGE,"E16.138.0"),sQuery(id+"F0.wireOp",EDGE,"E16.138.1"),sQuery(id+"F0.wireOp",EDGE,"E16.138.2"),sQuery(id+"F0.wireOp",EDGE,"E16.138.3"),sQuery(id+"F0.wireOp",EDGE,"E16.138.4"),sQuery(id+"F0.wireOp",EDGE,"E16.139.0"),sQuery(id+"F0.wireOp",EDGE,"E16.139.1"),sQuery(id+"F0.wireOp",EDGE,"E16.139.2"),sQuery(id+"F0.wireOp",EDGE,"E16.139.3"),sQuery(id+"F0.wireOp",EDGE,"E16.139.4"),sQuery(id+"F0.wireOp",EDGE,"E16.140.0"),sQuery(id+"F0.wireOp",EDGE,"E16.140.1"),sQuery(id+"F0.wireOp",EDGE,"E16.140.2"),sQuery(id+"F0.wireOp",EDGE,"E16.140.3"),sQuery(id+"F0.wireOp",EDGE,"E16.140.4"),sQuery(id+"F0.wireOp",EDGE,"E16.141.0"),sQuery(id+"F0.wireOp",EDGE,"E16.141.1"),sQuery(id+"F0.wireOp",EDGE,"E16.141.2"),sQuery(id+"F0.wireOp",EDGE,"E16.141.3"),sQuery(id+"F0.wireOp",EDGE,"E16.141.4"),sQuery(id+"F0.wireOp",EDGE,"E16.142.0"),sQuery(id+"F0.wireOp",EDGE,"E16.142.1"),sQuery(id+"F0.wireOp",EDGE,"E16.142.2"),sQuery(id+"F0.wireOp",EDGE,"E16.142.3"),sQuery(id+"F0.wireOp",EDGE,"E16.142.4"),sQuery(id+"F0.wireOp",EDGE,"E16.143.0"),sQuery(id+"F0.wireOp",EDGE,"E16.143.1"),sQuery(id+"F0.wireOp",EDGE,"E16.143.2"),sQuery(id+"F0.wireOp",EDGE,"E16.143.3"),sQuery(id+"F0.wireOp",EDGE,"E16.143.4"),sQuery(id+"F0.wireOp",EDGE,"E16.144.0"),sQuery(id+"F0.wireOp",EDGE,"E16.144.1"),sQuery(id+"F0.wireOp",EDGE,"E16.144.2"),sQuery(id+"F0.wireOp",EDGE,"E16.144.3"),sQuery(id+"F0.wireOp",EDGE,"E16.144.4"),sQuery(id+"F0.wireOp",EDGE,"E16.145.0"),sQuery(id+"F0.wireOp",EDGE,"E16.145.1"),sQuery(id+"F0.wireOp",EDGE,"E16.145.2"),sQuery(id+"F0.wireOp",EDGE,"E16.145.3"),sQuery(id+"F0.wireOp",EDGE,"E16.145.4"),sQuery(id+"F0.wireOp",EDGE,"E16.146.0"),sQuery(id+"F0.wireOp",EDGE,"E16.146.1"),sQuery(id+"F0.wireOp",EDGE,"E16.146.2"),sQuery(id+"F0.wireOp",EDGE,"E16.146.3"),sQuery(id+"F0.wireOp",EDGE,"E16.146.4"),sQuery(id+"F0.wireOp",EDGE,"E16.147.0"),sQuery(id+"F0.wireOp",EDGE,"E16.147.1"),sQuery(id+"F0.wireOp",EDGE,"E16.147.2"),sQuery(id+"F0.wireOp",EDGE,"E16.147.3"),sQuery(id+"F0.wireOp",EDGE,"E16.147.4"),sQuery(id+"F0.wireOp",EDGE,"E16.148.0"),sQuery(id+"F0.wireOp",EDGE,"E16.148.1"),sQuery(id+"F0.wireOp",EDGE,"E16.148.2"),sQuery(id+"F0.wireOp",EDGE,"E16.148.3"),sQuery(id+"F0.wireOp",EDGE,"E16.148.4"),sQuery(id+"F0.wireOp",EDGE,"E16.149.0"),sQuery(id+"F0.wireOp",EDGE,"E16.149.1"),sQuery(id+"F0.wireOp",EDGE,"E16.149.2"),sQuery(id+"F0.wireOp",EDGE,"E16.149.3"),sQuery(id+"F0.wireOp",EDGE,"E16.149.4"),sQuery(id+"F0.wireOp",EDGE,"E16.150.0"),sQuery(id+"F0.wireOp",EDGE,"E16.150.1"),sQuery(id+"F0.wireOp",EDGE,"E16.150.2"),sQuery(id+"F0.wireOp",EDGE,"E16.150.3"),sQuery(id+"F0.wireOp",EDGE,"E16.150.4"),sQuery(id+"F0.wireOp",EDGE,"E16.151.0"),sQuery(id+"F0.wireOp",EDGE,"E16.151.1"),sQuery(id+"F0.wireOp",EDGE,"E16.151.2"),sQuery(id+"F0.wireOp",EDGE,"E16.151.3"),sQuery(id+"F0.wireOp",EDGE,"E16.151.4"),sQuery(id+"F0.wireOp",EDGE,"E16.152.0"),sQuery(id+"F0.wireOp",EDGE,"E16.152.1"),sQuery(id+"F0.wireOp",EDGE,"E16.152.2"),sQuery(id+"F0.wireOp",EDGE,"E16.152.3"),sQuery(id+"F0.wireOp",EDGE,"E16.152.4"),sQuery(id+"F0.wireOp",EDGE,"E16.153.0"),sQuery(id+"F0.wireOp",EDGE,"E16.153.1"),sQuery(id+"F0.wireOp",EDGE,"E16.153.2"),sQuery(id+"F0.wireOp",EDGE,"E16.153.3"),sQuery(id+"F0.wireOp",EDGE,"E16.153.4"),sQuery(id+"F0.wireOp",EDGE,"E16.154.0"),sQuery(id+"F0.wireOp",EDGE,"E16.154.1"),sQuery(id+"F0.wireOp",EDGE,"E16.154.2"),sQuery(id+"F0.wireOp",EDGE,"E16.154.3"),sQuery(id+"F0.wireOp",EDGE,"E16.154.4"),sQuery(id+"F0.wireOp",EDGE,"E16.155.0"),sQuery(id+"F0.wireOp",EDGE,"E16.155.1"),sQuery(id+"F0.wireOp",EDGE,"E16.155.2"),sQuery(id+"F0.wireOp",EDGE,"E16.155.3"),sQuery(id+"F0.wireOp",EDGE,"E16.155.4"),sQuery(id+"F0.wireOp",EDGE,"E16.156.0"),sQuery(id+"F0.wireOp",EDGE,"E16.156.1"),sQuery(id+"F0.wireOp",EDGE,"E16.156.2"),sQuery(id+"F0.wireOp",EDGE,"E16.156.3"),sQuery(id+"F0.wireOp",EDGE,"E16.156.4"),sQuery(id+"F0.wireOp",EDGE,"E16.157.0"),sQuery(id+"F0.wireOp",EDGE,"E16.157.1"),sQuery(id+"F0.wireOp",EDGE,"E16.157.2"),sQuery(id+"F0.wireOp",EDGE,"E16.157.3"),sQuery(id+"F0.wireOp",EDGE,"E16.157.4"),sQuery(id+"F0.wireOp",EDGE,"E16.158.0"),sQuery(id+"F0.wireOp",EDGE,"E16.158.1"),sQuery(id+"F0.wireOp",EDGE,"E16.158.2"),sQuery(id+"F0.wireOp",EDGE,"E16.158.3"),sQuery(id+"F0.wireOp",EDGE,"E16.158.4"),sQuery(id+"F0.wireOp",EDGE,"E16.159.0"),sQuery(id+"F0.wireOp",EDGE,"E16.159.1"),sQuery(id+"F0.wireOp",EDGE,"E16.159.2"),sQuery(id+"F0.wireOp",EDGE,"E16.159.3"),sQuery(id+"F0.wireOp",EDGE,"E16.159.4"),sQuery(id+"F0.wireOp",EDGE,"E16.160.0"),sQuery(id+"F0.wireOp",EDGE,"E16.160.1"),sQuery(id+"F0.wireOp",EDGE,"E16.160.2"),sQuery(id+"F0.wireOp",EDGE,"E16.160.3"),sQuery(id+"F0.wireOp",EDGE,"E16.160.4"),sQuery(id+"F0.wireOp",EDGE,"E16.161.0"),sQuery(id+"F0.wireOp",EDGE,"E16.161.1"),sQuery(id+"F0.wireOp",EDGE,"E16.161.2"),sQuery(id+"F0.wireOp",EDGE,"E16.161.3"),sQuery(id+"F0.wireOp",EDGE,"E16.161.4"),sQuery(id+"F0.wireOp",EDGE,"E16.162.0"),sQuery(id+"F0.wireOp",EDGE,"E16.162.1"),sQuery(id+"F0.wireOp",EDGE,"E16.162.2"),sQuery(id+"F0.wireOp",EDGE,"E16.162.3"),sQuery(id+"F0.wireOp",EDGE,"E16.162.4"),sQuery(id+"F0.wireOp",EDGE,"E16.163.0"),sQuery(id+"F0.wireOp",EDGE,"E16.163.1"),sQuery(id+"F0.wireOp",EDGE,"E16.163.2"),sQuery(id+"F0.wireOp",EDGE,"E16.163.3"),sQuery(id+"F0.wireOp",EDGE,"E16.163.4"),sQuery(id+"F0.wireOp",EDGE,"E16.164.0"),sQuery(id+"F0.wireOp",EDGE,"E16.164.1"),sQuery(id+"F0.wireOp",EDGE,"E16.164.2"),sQuery(id+"F0.wireOp",EDGE,"E16.164.3"),sQuery(id+"F0.wireOp",EDGE,"E16.164.4"),sQuery(id+"F0.wireOp",EDGE,"E16.165.0"),sQuery(id+"F0.wireOp",EDGE,"E16.165.1"),sQuery(id+"F0.wireOp",EDGE,"E16.165.2"),sQuery(id+"F0.wireOp",EDGE,"E16.165.3"),sQuery(id+"F0.wireOp",EDGE,"E16.165.4"),sQuery(id+"F0.wireOp",EDGE,"E16.166.0"),sQuery(id+"F0.wireOp",EDGE,"E16.166.1"),sQuery(id+"F0.wireOp",EDGE,"E16.166.2"),sQuery(id+"F0.wireOp",EDGE,"E16.166.3"),sQuery(id+"F0.wireOp",EDGE,"E16.166.4"),sQuery(id+"F0.wireOp",EDGE,"E16.167.0"),sQuery(id+"F0.wireOp",EDGE,"E16.167.1"),sQuery(id+"F0.wireOp",EDGE,"E16.167.2"),sQuery(id+"F0.wireOp",EDGE,"E16.167.3"),sQuery(id+"F0.wireOp",EDGE,"E16.167.4"),sQuery(id+"F0.wireOp",EDGE,"E16.168.0"),sQuery(id+"F0.wireOp",EDGE,"E16.168.1"),sQuery(id+"F0.wireOp",EDGE,"E16.168.2"),sQuery(id+"F0.wireOp",EDGE,"E16.168.3"),sQuery(id+"F0.wireOp",EDGE,"E16.168.4"),sQuery(id+"F0.wireOp",EDGE,"E16.169.0"),sQuery(id+"F0.wireOp",EDGE,"E16.169.1"),sQuery(id+"F0.wireOp",EDGE,"E16.169.2"),sQuery(id+"F0.wireOp",EDGE,"E16.169.3"),sQuery(id+"F0.wireOp",EDGE,"E16.169.4"),sQuery(id+"F0.wireOp",EDGE,"E16.170.0"),sQuery(id+"F0.wireOp",EDGE,"E16.170.1"),sQuery(id+"F0.wireOp",EDGE,"E16.170.2"),sQuery(id+"F0.wireOp",EDGE,"E16.170.3"),sQuery(id+"F0.wireOp",EDGE,"E16.170.4"),sQuery(id+"F0.wireOp",EDGE,"E16.171.0"),sQuery(id+"F0.wireOp",EDGE,"E16.171.1"),sQuery(id+"F0.wireOp",EDGE,"E16.171.2"),sQuery(id+"F0.wireOp",EDGE,"E16.171.3"),sQuery(id+"F0.wireOp",EDGE,"E16.171.4"),sQuery(id+"F0.wireOp",EDGE,"E16.172.0"),sQuery(id+"F0.wireOp",EDGE,"E16.172.1"),sQuery(id+"F0.wireOp",EDGE,"E16.172.2"),sQuery(id+"F0.wireOp",EDGE,"E16.172.3"),sQuery(id+"F0.wireOp",EDGE,"E16.172.4"),sQuery(id+"F0.wireOp",EDGE,"E16.173.0"),sQuery(id+"F0.wireOp",EDGE,"E16.173.1"),sQuery(id+"F0.wireOp",EDGE,"E16.173.2"),sQuery(id+"F0.wireOp",EDGE,"E16.173.3"),sQuery(id+"F0.wireOp",EDGE,"E16.173.4"),sQuery(id+"F0.wireOp",EDGE,"E16.174.0"),sQuery(id+"F0.wireOp",EDGE,"E16.174.1"),sQuery(id+"F0.wireOp",EDGE,"E16.174.2"),sQuery(id+"F0.wireOp",EDGE,"E16.174.3"),sQuery(id+"F0.wireOp",EDGE,"E16.174.4"),sQuery(id+"F0.wireOp",EDGE,"E16.175.0"),sQuery(id+"F0.wireOp",EDGE,"E16.175.1"),sQuery(id+"F0.wireOp",EDGE,"E16.175.2"),sQuery(id+"F0.wireOp",EDGE,"E16.175.3"),sQuery(id+"F0.wireOp",EDGE,"E16.175.4"),sQuery(id+"F0.wireOp",EDGE,"E16.176.0"),sQuery(id+"F0.wireOp",EDGE,"E16.176.1"),sQuery(id+"F0.wireOp",EDGE,"E16.176.2"),sQuery(id+"F0.wireOp",EDGE,"E16.176.3"),sQuery(id+"F0.wireOp",EDGE,"E16.176.4"),sQuery(id+"F0.wireOp",EDGE,"E16.177.0"),sQuery(id+"F0.wireOp",EDGE,"E16.177.1"),sQuery(id+"F0.wireOp",EDGE,"E16.177.2"),sQuery(id+"F0.wireOp",EDGE,"E16.177.3"),sQuery(id+"F0.wireOp",EDGE,"E16.177.4"),sQuery(id+"F0.wireOp",EDGE,"E16.178.0"),sQuery(id+"F0.wireOp",EDGE,"E16.178.1"),sQuery(id+"F0.wireOp",EDGE,"E16.178.2"),sQuery(id+"F0.wireOp",EDGE,"E16.178.3"),sQuery(id+"F0.wireOp",EDGE,"E16.178.4"),sQuery(id+"F0.wireOp",EDGE,"E16.179.0"),sQuery(id+"F0.wireOp",EDGE,"E16.179.1"),sQuery(id+"F0.wireOp",EDGE,"E16.179.2"),sQuery(id+"F0.wireOp",EDGE,"E16.179.3"),sQuery(id+"F0.wireOp",EDGE,"E16.179.4"),sQuery(id+"F0.wireOp",EDGE,"E16.180.0"),sQuery(id+"F0.wireOp",EDGE,"E16.180.1"),sQuery(id+"F0.wireOp",EDGE,"E16.180.2"),sQuery(id+"F0.wireOp",EDGE,"E16.180.3"),sQuery(id+"F0.wireOp",EDGE,"E16.180.4"),sQuery(id+"F0.wireOp",EDGE,"E16.181.0"),sQuery(id+"F0.wireOp",EDGE,"E16.181.1"),sQuery(id+"F0.wireOp",EDGE,"E16.181.2"),sQuery(id+"F0.wireOp",EDGE,"E16.181.3"),sQuery(id+"F0.wireOp",EDGE,"E16.181.4"),sQuery(id+"F0.wireOp",EDGE,"E16.182.0"),sQuery(id+"F0.wireOp",EDGE,"E16.182.1"),sQuery(id+"F0.wireOp",EDGE,"E16.182.2"),sQuery(id+"F0.wireOp",EDGE,"E16.182.3"),sQuery(id+"F0.wireOp",EDGE,"E16.182.4"),sQuery(id+"F0.wireOp",EDGE,"E16.183.0"),sQuery(id+"F0.wireOp",EDGE,"E16.183.1"),sQuery(id+"F0.wireOp",EDGE,"E16.183.2"),sQuery(id+"F0.wireOp",EDGE,"E16.183.3"),sQuery(id+"F0.wireOp",EDGE,"E16.183.4"),sQuery(id+"F0.wireOp",EDGE,"E16.184.0"),sQuery(id+"F0.wireOp",EDGE,"E16.184.1"),sQuery(id+"F0.wireOp",EDGE,"E16.184.2"),sQuery(id+"F0.wireOp",EDGE,"E16.184.3"),sQuery(id+"F0.wireOp",EDGE,"E16.184.4"),sQuery(id+"F0.wireOp",EDGE,"E16.185.0"),sQuery(id+"F0.wireOp",EDGE,"E16.185.1"),sQuery(id+"F0.wireOp",EDGE,"E16.185.2"),sQuery(id+"F0.wireOp",EDGE,"E16.185.3"),sQuery(id+"F0.wireOp",EDGE,"E16.185.4"),sQuery(id+"F0.wireOp",EDGE,"E16.186.0"),sQuery(id+"F0.wireOp",EDGE,"E16.186.1"),sQuery(id+"F0.wireOp",EDGE,"E16.186.2"),sQuery(id+"F0.wireOp",EDGE,"E16.186.3"),sQuery(id+"F0.wireOp",EDGE,"E16.186.4"),sQuery(id+"F0.wireOp",EDGE,"E16.187.0"),sQuery(id+"F0.wireOp",EDGE,"E16.187.1"),sQuery(id+"F0.wireOp",EDGE,"E16.187.2"),sQuery(id+"F0.wireOp",EDGE,"E16.187.3"),sQuery(id+"F0.wireOp",EDGE,"E16.187.4"),sQuery(id+"F0.wireOp",EDGE,"E16.188.0"),sQuery(id+"F0.wireOp",EDGE,"E16.188.1"),sQuery(id+"F0.wireOp",EDGE,"E16.188.2"),sQuery(id+"F0.wireOp",EDGE,"E16.188.3"),sQuery(id+"F0.wireOp",EDGE,"E16.188.4"),sQuery(id+"F0.wireOp",EDGE,"E16.189.0"),sQuery(id+"F0.wireOp",EDGE,"E16.189.1"),sQuery(id+"F0.wireOp",EDGE,"E16.189.2"),sQuery(id+"F0.wireOp",EDGE,"E16.189.3"),sQuery(id+"F0.wireOp",EDGE,"E16.189.4"),sQuery(id+"F0.wireOp",EDGE,"E16.190.0"),sQuery(id+"F0.wireOp",EDGE,"E16.190.1"),sQuery(id+"F0.wireOp",EDGE,"E16.190.2"),sQuery(id+"F0.wireOp",EDGE,"E16.190.3"),sQuery(id+"F0.wireOp",EDGE,"E16.190.4"),sQuery(id+"F0.wireOp",EDGE,"E16.191.0"),sQuery(id+"F0.wireOp",EDGE,"E16.191.1"),sQuery(id+"F0.wireOp",EDGE,"E16.191.2"),sQuery(id+"F0.wireOp",EDGE,"E16.191.3"),sQuery(id+"F0.wireOp",EDGE,"E16.191.4")])]});
            hole(context, id + "F6", {"style" : HoleStyle.C_SINK, "endStyle" : HoleEndStyle.THROUGH, "standardTappedOrClearance" : lookupTablePath({ "fit" : "Normal", "standard" : "ISO", "size" : "M4", "type" : "Clearance" }), "standardBlindInLast" : lookupTablePath({ "fit" : "Standard", "standard" : "ISO", "size" : "M4", "type" : "Clearance" }), "holeDiameter" : 4.4 * mm, "cSinkDiameter" : 8.96 * mm, "cSinkAngle" : 90 * degree, "majorDiameter" : 5 * mm, "isTappedThrough" : true, "tappedDepth" : 12 * mm, "tapClearance" : 3, "startFromSketch" : true, "locations" : qUnion([Q0]), "scope" : qUnion([Q1])});
        }
        {
            var Q0;
            Q0=makeQuery(id+"FnGEPf5ERnqVvQ3_1.1.F4.boolean.opBoolean","SPLIT",EDGE,{"disambiguationData":[OD(1.0)],"derivedFrom":makeQuery(id+"F1.opExtrude","CAP_EDGE",EDGE,{"disambiguationData":[OSD([sQuery(id+"F0.wireOp",EDGE,"E0")])],"isStart":true})});
            var Q1;
            Q1=makeQuery(id+"FnGEPf5ERnqVvQ3_1.1.F4.opExtrude","CAP_EDGE",EDGE,{"disambiguationData":[OSD([sQuery(id+"F3.wireOp",EDGE,"E23")])],"isStart":false});
            var Q2;
            {var subQ0=sQuery(id+"F3.wireOp",EDGE,"E23");var subQ2=sQuery(id+"F0.wireOp",EDGE,"E0");Q2=makeQuery(id+"FnGEPf5ERnqVvQ3_1.2.F4.boolean.opBoolean","SPLIT",EDGE,{"disambiguationData":[TD([makeQuery(id+"FnGEPf5ERnqVvQ3_1.1.F4.opExtrude","SWEPT_FACE",FACE,{"disambiguationData":[OSD([subQ0])]})])],"derivedFrom":makeQuery(id+"FnGEPf5ERnqVvQ3_1.1.F4.boolean.opBoolean","SPLIT",EDGE,{"disambiguationData":[OD(0.0)],"derivedFrom":makeQuery(id+"F1.opExtrude","CAP_EDGE",EDGE,{"disambiguationData":[OSD([subQ2])],"isStart":true})})});}
            var Q3;
            Q3=makeQuery(id+"FnGEPf5ERnqVvQ3_1.2.F4.opExtrude","CAP_EDGE",EDGE,{"disambiguationData":[OSD([sQuery(id+"F3.wireOp",EDGE,"E23")])],"isStart":false});
            var Q4;
            {var subQ0=sQuery(id+"F3.wireOp",EDGE,"E23");var subQ4=sQuery(id+"F0.wireOp",EDGE,"E0");var subQ8=makeQuery(id+"FnGEPf5ERnqVvQ3_1.2.F4.opExtrude","SWEPT_FACE",FACE,{"disambiguationData":[OSD([subQ0])]});Q4=makeQuery(id+"FnGEPf5ERnqVvQ3_1.3.F4.boolean.opBoolean","SPLIT",EDGE,{"disambiguationData":[TD([subQ8])],"derivedFrom":makeQuery(id+"FnGEPf5ERnqVvQ3_1.2.F4.boolean.opBoolean","SPLIT",EDGE,{"disambiguationData":[TD([makeQuery(id+"F4.opExtrude","SWEPT_FACE",FACE,{"disambiguationData":[OSD([subQ0])]})])],"derivedFrom":makeQuery(id+"FnGEPf5ERnqVvQ3_1.1.F4.boolean.opBoolean","SPLIT",EDGE,{"disambiguationData":[OD(0.0)],"derivedFrom":makeQuery(id+"F1.opExtrude","CAP_EDGE",EDGE,{"disambiguationData":[OSD([subQ4])],"isStart":true})})})});}
            var Q5;
            Q5=makeQuery(id+"FnGEPf5ERnqVvQ3_1.3.F4.opExtrude","CAP_EDGE",EDGE,{"disambiguationData":[OSD([sQuery(id+"F3.wireOp",EDGE,"E23")])],"isStart":false});
            var Q6;
            {var subQ0=sQuery(id+"F3.wireOp",EDGE,"E23");var subQ4=sQuery(id+"F0.wireOp",EDGE,"E0");var subQ9=makeQuery(id+"FnGEPf5ERnqVvQ3_1.3.F4.opExtrude","SWEPT_FACE",FACE,{"disambiguationData":[OSD([subQ0])]});var subQ10=makeQuery(id+"F4.opExtrude","SWEPT_FACE",FACE,{"disambiguationData":[OSD([subQ0])]});Q6=makeQuery(id+"FnGEPf5ERnqVvQ3_1.4.F4.boolean.opBoolean","SPLIT",EDGE,{"disambiguationData":[TD([subQ9])],"derivedFrom":makeQuery(id+"FnGEPf5ERnqVvQ3_1.3.F4.boolean.opBoolean","SPLIT",EDGE,{"disambiguationData":[TD([subQ10])],"derivedFrom":makeQuery(id+"FnGEPf5ERnqVvQ3_1.2.F4.boolean.opBoolean","SPLIT",EDGE,{"disambiguationData":[TD([subQ10])],"derivedFrom":makeQuery(id+"FnGEPf5ERnqVvQ3_1.1.F4.boolean.opBoolean","SPLIT",EDGE,{"disambiguationData":[OD(0.0)],"derivedFrom":makeQuery(id+"F1.opExtrude","CAP_EDGE",EDGE,{"disambiguationData":[OSD([subQ4])],"isStart":true})})})})});}
            var Q7;
            Q7=makeQuery(id+"FnGEPf5ERnqVvQ3_1.4.F4.opExtrude","CAP_EDGE",EDGE,{"disambiguationData":[OSD([sQuery(id+"F3.wireOp",EDGE,"E23")])],"isStart":false});
            var Q8;
            {var subQ0=sQuery(id+"F3.wireOp",EDGE,"E23");var subQ4=sQuery(id+"F0.wireOp",EDGE,"E0");var subQ6=makeQuery(id+"FnGEPf5ERnqVvQ3_1.4.F4.opExtrude","SWEPT_FACE",FACE,{"disambiguationData":[OSD([subQ0])]});var subQ11=makeQuery(id+"F4.opExtrude","SWEPT_FACE",FACE,{"disambiguationData":[OSD([subQ0])]});Q8=makeQuery(id+"FnGEPf5ERnqVvQ3_1.5.F4.boolean.opBoolean","SPLIT",EDGE,{"disambiguationData":[TD([subQ6])],"derivedFrom":makeQuery(id+"FnGEPf5ERnqVvQ3_1.4.F4.boolean.opBoolean","SPLIT",EDGE,{"disambiguationData":[TD([subQ11])],"derivedFrom":makeQuery(id+"FnGEPf5ERnqVvQ3_1.3.F4.boolean.opBoolean","SPLIT",EDGE,{"disambiguationData":[TD([subQ11])],"derivedFrom":makeQuery(id+"FnGEPf5ERnqVvQ3_1.2.F4.boolean.opBoolean","SPLIT",EDGE,{"disambiguationData":[TD([subQ11])],"derivedFrom":makeQuery(id+"FnGEPf5ERnqVvQ3_1.1.F4.boolean.opBoolean","SPLIT",EDGE,{"disambiguationData":[OD(0.0)],"derivedFrom":makeQuery(id+"F1.opExtrude","CAP_EDGE",EDGE,{"disambiguationData":[OSD([subQ4])],"isStart":true})})})})})});}
            var Q9;
            Q9=makeQuery(id+"FnGEPf5ERnqVvQ3_1.5.F4.opExtrude","CAP_EDGE",EDGE,{"disambiguationData":[OSD([sQuery(id+"F3.wireOp",EDGE,"E23")])],"isStart":false});
            var Q10;
            {var subQ0=sQuery(id+"F3.wireOp",EDGE,"E23");var subQ6=sQuery(id+"F0.wireOp",EDGE,"E0");var subQ10=makeQuery(id+"FnGEPf5ERnqVvQ3_1.5.F4.opExtrude","SWEPT_FACE",FACE,{"disambiguationData":[OSD([subQ0])]});var subQ12=makeQuery(id+"F4.opExtrude","SWEPT_FACE",FACE,{"disambiguationData":[OSD([subQ0])]});Q10=makeQuery(id+"FnGEPf5ERnqVvQ3_1.6.F4.boolean.opBoolean","SPLIT",EDGE,{"disambiguationData":[TD([subQ10])],"derivedFrom":makeQuery(id+"FnGEPf5ERnqVvQ3_1.5.F4.boolean.opBoolean","SPLIT",EDGE,{"disambiguationData":[TD([subQ12])],"derivedFrom":makeQuery(id+"FnGEPf5ERnqVvQ3_1.4.F4.boolean.opBoolean","SPLIT",EDGE,{"disambiguationData":[TD([subQ12])],"derivedFrom":makeQuery(id+"FnGEPf5ERnqVvQ3_1.3.F4.boolean.opBoolean","SPLIT",EDGE,{"disambiguationData":[TD([subQ12])],"derivedFrom":makeQuery(id+"FnGEPf5ERnqVvQ3_1.2.F4.boolean.opBoolean","SPLIT",EDGE,{"disambiguationData":[TD([subQ12])],"derivedFrom":makeQuery(id+"FnGEPf5ERnqVvQ3_1.1.F4.boolean.opBoolean","SPLIT",EDGE,{"disambiguationData":[OD(0.0)],"derivedFrom":makeQuery(id+"F1.opExtrude","CAP_EDGE",EDGE,{"disambiguationData":[OSD([subQ6])],"isStart":true})})})})})})});}
            var Q11;
            Q11=makeQuery(id+"FnGEPf5ERnqVvQ3_1.6.F4.opExtrude","CAP_EDGE",EDGE,{"disambiguationData":[OSD([sQuery(id+"F3.wireOp",EDGE,"E23")])],"isStart":false});
            var Q12;
            {var subQ0=sQuery(id+"F3.wireOp",EDGE,"E23");var subQ6=makeQuery(id+"FnGEPf5ERnqVvQ3_1.6.F4.opExtrude","SWEPT_FACE",FACE,{"disambiguationData":[OSD([subQ0])]});var subQ8=sQuery(id+"F0.wireOp",EDGE,"E0");var subQ13=makeQuery(id+"F4.opExtrude","SWEPT_FACE",FACE,{"disambiguationData":[OSD([subQ0])]});Q12=makeQuery(id+"FnGEPf5ERnqVvQ3_1.7.F4.boolean.opBoolean","SPLIT",EDGE,{"disambiguationData":[TD([subQ6])],"derivedFrom":makeQuery(id+"FnGEPf5ERnqVvQ3_1.6.F4.boolean.opBoolean","SPLIT",EDGE,{"disambiguationData":[TD([subQ13])],"derivedFrom":makeQuery(id+"FnGEPf5ERnqVvQ3_1.5.F4.boolean.opBoolean","SPLIT",EDGE,{"disambiguationData":[TD([subQ13])],"derivedFrom":makeQuery(id+"FnGEPf5ERnqVvQ3_1.4.F4.boolean.opBoolean","SPLIT",EDGE,{"disambiguationData":[TD([subQ13])],"derivedFrom":makeQuery(id+"FnGEPf5ERnqVvQ3_1.3.F4.boolean.opBoolean","SPLIT",EDGE,{"disambiguationData":[TD([subQ13])],"derivedFrom":makeQuery(id+"FnGEPf5ERnqVvQ3_1.2.F4.boolean.opBoolean","SPLIT",EDGE,{"disambiguationData":[TD([subQ13])],"derivedFrom":makeQuery(id+"FnGEPf5ERnqVvQ3_1.1.F4.boolean.opBoolean","SPLIT",EDGE,{"disambiguationData":[OD(0.0)],"derivedFrom":makeQuery(id+"F1.opExtrude","CAP_EDGE",EDGE,{"disambiguationData":[OSD([subQ8])],"isStart":true})})})})})})})});}
            var Q13;
            {var subQ0=sQuery(id+"F3.wireOp",EDGE,"E23");var subQ8=sQuery(id+"F0.wireOp",EDGE,"E0");var subQ13=makeQuery(id+"FnGEPf5ERnqVvQ3_1.7.F4.opExtrude","SWEPT_FACE",FACE,{"disambiguationData":[OSD([subQ0])]});var subQ14=makeQuery(id+"F4.opExtrude","SWEPT_FACE",FACE,{"disambiguationData":[OSD([subQ0])]});Q13=makeQuery(id+"FnGEPf5ERnqVvQ3_1.8.F4.boolean.opBoolean","SPLIT",EDGE,{"disambiguationData":[TD([subQ13])],"derivedFrom":makeQuery(id+"FnGEPf5ERnqVvQ3_1.7.F4.boolean.opBoolean","SPLIT",EDGE,{"disambiguationData":[TD([subQ14])],"derivedFrom":makeQuery(id+"FnGEPf5ERnqVvQ3_1.6.F4.boolean.opBoolean","SPLIT",EDGE,{"disambiguationData":[TD([subQ14])],"derivedFrom":makeQuery(id+"FnGEPf5ERnqVvQ3_1.5.F4.boolean.opBoolean","SPLIT",EDGE,{"disambiguationData":[TD([subQ14])],"derivedFrom":makeQuery(id+"FnGEPf5ERnqVvQ3_1.4.F4.boolean.opBoolean","SPLIT",EDGE,{"disambiguationData":[TD([subQ14])],"derivedFrom":makeQuery(id+"FnGEPf5ERnqVvQ3_1.3.F4.boolean.opBoolean","SPLIT",EDGE,{"disambiguationData":[TD([subQ14])],"derivedFrom":makeQuery(id+"FnGEPf5ERnqVvQ3_1.2.F4.boolean.opBoolean","SPLIT",EDGE,{"disambiguationData":[TD([subQ14])],"derivedFrom":makeQuery(id+"FnGEPf5ERnqVvQ3_1.1.F4.boolean.opBoolean","SPLIT",EDGE,{"disambiguationData":[OD(0.0)],"derivedFrom":makeQuery(id+"F1.opExtrude","CAP_EDGE",EDGE,{"disambiguationData":[OSD([subQ8])],"isStart":true})})})})})})})})});}
            var Q14;
            Q14=makeQuery(id+"FnGEPf5ERnqVvQ3_1.7.F4.opExtrude","CAP_EDGE",EDGE,{"disambiguationData":[OSD([sQuery(id+"F3.wireOp",EDGE,"E23")])],"isStart":false});
            var Q15;
            Q15=makeQuery(id+"FnGEPf5ERnqVvQ3_1.8.F4.opExtrude","CAP_EDGE",EDGE,{"disambiguationData":[OSD([sQuery(id+"F3.wireOp",EDGE,"E23")])],"isStart":false});
            var Q16;
            {var subQ0=sQuery(id+"F3.wireOp",EDGE,"E23");var subQ8=sQuery(id+"F0.wireOp",EDGE,"E0");var subQ14=makeQuery(id+"FnGEPf5ERnqVvQ3_1.8.F4.opExtrude","SWEPT_FACE",FACE,{"disambiguationData":[OSD([subQ0])]});var subQ15=makeQuery(id+"F4.opExtrude","SWEPT_FACE",FACE,{"disambiguationData":[OSD([subQ0])]});Q16=makeQuery(id+"FnGEPf5ERnqVvQ3_1.9.F4.boolean.opBoolean","SPLIT",EDGE,{"disambiguationData":[TD([subQ14])],"derivedFrom":makeQuery(id+"FnGEPf5ERnqVvQ3_1.8.F4.boolean.opBoolean","SPLIT",EDGE,{"disambiguationData":[TD([subQ15])],"derivedFrom":makeQuery(id+"FnGEPf5ERnqVvQ3_1.7.F4.boolean.opBoolean","SPLIT",EDGE,{"disambiguationData":[TD([subQ15])],"derivedFrom":makeQuery(id+"FnGEPf5ERnqVvQ3_1.6.F4.boolean.opBoolean","SPLIT",EDGE,{"disambiguationData":[TD([subQ15])],"derivedFrom":makeQuery(id+"FnGEPf5ERnqVvQ3_1.5.F4.boolean.opBoolean","SPLIT",EDGE,{"disambiguationData":[TD([subQ15])],"derivedFrom":makeQuery(id+"FnGEPf5ERnqVvQ3_1.4.F4.boolean.opBoolean","SPLIT",EDGE,{"disambiguationData":[TD([subQ15])],"derivedFrom":makeQuery(id+"FnGEPf5ERnqVvQ3_1.3.F4.boolean.opBoolean","SPLIT",EDGE,{"disambiguationData":[TD([subQ15])],"derivedFrom":makeQuery(id+"FnGEPf5ERnqVvQ3_1.2.F4.boolean.opBoolean","SPLIT",EDGE,{"disambiguationData":[TD([subQ15])],"derivedFrom":makeQuery(id+"FnGEPf5ERnqVvQ3_1.1.F4.boolean.opBoolean","SPLIT",EDGE,{"disambiguationData":[OD(0.0)],"derivedFrom":makeQuery(id+"F1.opExtrude","CAP_EDGE",EDGE,{"disambiguationData":[OSD([subQ8])],"isStart":true})})})})})})})})})});}
            var Q17;
            Q17=makeQuery(id+"FnGEPf5ERnqVvQ3_1.9.F4.opExtrude","CAP_EDGE",EDGE,{"disambiguationData":[OSD([sQuery(id+"F3.wireOp",EDGE,"E23")])],"isStart":false});
            var Q18;
            {var subQ0=sQuery(id+"F3.wireOp",EDGE,"E23");var subQ8=sQuery(id+"F0.wireOp",EDGE,"E0");var subQ15=makeQuery(id+"FnGEPf5ERnqVvQ3_1.9.F4.opExtrude","SWEPT_FACE",FACE,{"disambiguationData":[OSD([subQ0])]});var subQ16=makeQuery(id+"F4.opExtrude","SWEPT_FACE",FACE,{"disambiguationData":[OSD([subQ0])]});Q18=makeQuery(id+"FnGEPf5ERnqVvQ3_1.10.F4.boolean.opBoolean","SPLIT",EDGE,{"disambiguationData":[TD([subQ15])],"derivedFrom":makeQuery(id+"FnGEPf5ERnqVvQ3_1.9.F4.boolean.opBoolean","SPLIT",EDGE,{"disambiguationData":[TD([subQ16])],"derivedFrom":makeQuery(id+"FnGEPf5ERnqVvQ3_1.8.F4.boolean.opBoolean","SPLIT",EDGE,{"disambiguationData":[TD([subQ16])],"derivedFrom":makeQuery(id+"FnGEPf5ERnqVvQ3_1.7.F4.boolean.opBoolean","SPLIT",EDGE,{"disambiguationData":[TD([subQ16])],"derivedFrom":makeQuery(id+"FnGEPf5ERnqVvQ3_1.6.F4.boolean.opBoolean","SPLIT",EDGE,{"disambiguationData":[TD([subQ16])],"derivedFrom":makeQuery(id+"FnGEPf5ERnqVvQ3_1.5.F4.boolean.opBoolean","SPLIT",EDGE,{"disambiguationData":[TD([subQ16])],"derivedFrom":makeQuery(id+"FnGEPf5ERnqVvQ3_1.4.F4.boolean.opBoolean","SPLIT",EDGE,{"disambiguationData":[TD([subQ16])],"derivedFrom":makeQuery(id+"FnGEPf5ERnqVvQ3_1.3.F4.boolean.opBoolean","SPLIT",EDGE,{"disambiguationData":[TD([subQ16])],"derivedFrom":makeQuery(id+"FnGEPf5ERnqVvQ3_1.2.F4.boolean.opBoolean","SPLIT",EDGE,{"disambiguationData":[TD([subQ16])],"derivedFrom":makeQuery(id+"FnGEPf5ERnqVvQ3_1.1.F4.boolean.opBoolean","SPLIT",EDGE,{"disambiguationData":[OD(0.0)],"derivedFrom":makeQuery(id+"F1.opExtrude","CAP_EDGE",EDGE,{"disambiguationData":[OSD([subQ8])],"isStart":true})})})})})})})})})})});}
            var Q19;
            Q19=makeQuery(id+"FnGEPf5ERnqVvQ3_1.10.F4.opExtrude","CAP_EDGE",EDGE,{"disambiguationData":[OSD([sQuery(id+"F3.wireOp",EDGE,"E23")])],"isStart":false});
            var Q20;
            {var subQ0=sQuery(id+"F3.wireOp",EDGE,"E23");var subQ8=sQuery(id+"F0.wireOp",EDGE,"E0");var subQ16=makeQuery(id+"FnGEPf5ERnqVvQ3_1.10.F4.opExtrude","SWEPT_FACE",FACE,{"disambiguationData":[OSD([subQ0])]});var subQ17=makeQuery(id+"F4.opExtrude","SWEPT_FACE",FACE,{"disambiguationData":[OSD([subQ0])]});Q20=makeQuery(id+"FnGEPf5ERnqVvQ3_1.11.F4.boolean.opBoolean","SPLIT",EDGE,{"disambiguationData":[TD([subQ16])],"derivedFrom":makeQuery(id+"FnGEPf5ERnqVvQ3_1.10.F4.boolean.opBoolean","SPLIT",EDGE,{"disambiguationData":[TD([subQ17])],"derivedFrom":makeQuery(id+"FnGEPf5ERnqVvQ3_1.9.F4.boolean.opBoolean","SPLIT",EDGE,{"disambiguationData":[TD([subQ17])],"derivedFrom":makeQuery(id+"FnGEPf5ERnqVvQ3_1.8.F4.boolean.opBoolean","SPLIT",EDGE,{"disambiguationData":[TD([subQ17])],"derivedFrom":makeQuery(id+"FnGEPf5ERnqVvQ3_1.7.F4.boolean.opBoolean","SPLIT",EDGE,{"disambiguationData":[TD([subQ17])],"derivedFrom":makeQuery(id+"FnGEPf5ERnqVvQ3_1.6.F4.boolean.opBoolean","SPLIT",EDGE,{"disambiguationData":[TD([subQ17])],"derivedFrom":makeQuery(id+"FnGEPf5ERnqVvQ3_1.5.F4.boolean.opBoolean","SPLIT",EDGE,{"disambiguationData":[TD([subQ17])],"derivedFrom":makeQuery(id+"FnGEPf5ERnqVvQ3_1.4.F4.boolean.opBoolean","SPLIT",EDGE,{"disambiguationData":[TD([subQ17])],"derivedFrom":makeQuery(id+"FnGEPf5ERnqVvQ3_1.3.F4.boolean.opBoolean","SPLIT",EDGE,{"disambiguationData":[TD([subQ17])],"derivedFrom":makeQuery(id+"FnGEPf5ERnqVvQ3_1.2.F4.boolean.opBoolean","SPLIT",EDGE,{"disambiguationData":[TD([subQ17])],"derivedFrom":makeQuery(id+"FnGEPf5ERnqVvQ3_1.1.F4.boolean.opBoolean","SPLIT",EDGE,{"disambiguationData":[OD(0.0)],"derivedFrom":makeQuery(id+"F1.opExtrude","CAP_EDGE",EDGE,{"disambiguationData":[OSD([subQ8])],"isStart":true})})})})})})})})})})})});}
            var Q21;
            Q21=makeQuery(id+"FnGEPf5ERnqVvQ3_1.11.F4.opExtrude","CAP_EDGE",EDGE,{"disambiguationData":[OSD([sQuery(id+"F3.wireOp",EDGE,"E23")])],"isStart":false});
            var Q22;
            {var subQ0=sQuery(id+"F3.wireOp",EDGE,"E23");var subQ8=sQuery(id+"F0.wireOp",EDGE,"E0");var subQ12=makeQuery(id+"F4.opExtrude","SWEPT_FACE",FACE,{"disambiguationData":[OSD([subQ0])]});Q22=makeQuery(id+"FnGEPf5ERnqVvQ3_1.11.F4.boolean.opBoolean","SPLIT",EDGE,{"disambiguationData":[TD([subQ12])],"derivedFrom":makeQuery(id+"FnGEPf5ERnqVvQ3_1.10.F4.boolean.opBoolean","SPLIT",EDGE,{"disambiguationData":[TD([subQ12])],"derivedFrom":makeQuery(id+"FnGEPf5ERnqVvQ3_1.9.F4.boolean.opBoolean","SPLIT",EDGE,{"disambiguationData":[TD([subQ12])],"derivedFrom":makeQuery(id+"FnGEPf5ERnqVvQ3_1.8.F4.boolean.opBoolean","SPLIT",EDGE,{"disambiguationData":[TD([subQ12])],"derivedFrom":makeQuery(id+"FnGEPf5ERnqVvQ3_1.7.F4.boolean.opBoolean","SPLIT",EDGE,{"disambiguationData":[TD([subQ12])],"derivedFrom":makeQuery(id+"FnGEPf5ERnqVvQ3_1.6.F4.boolean.opBoolean","SPLIT",EDGE,{"disambiguationData":[TD([subQ12])],"derivedFrom":makeQuery(id+"FnGEPf5ERnqVvQ3_1.5.F4.boolean.opBoolean","SPLIT",EDGE,{"disambiguationData":[TD([subQ12])],"derivedFrom":makeQuery(id+"FnGEPf5ERnqVvQ3_1.4.F4.boolean.opBoolean","SPLIT",EDGE,{"disambiguationData":[TD([subQ12])],"derivedFrom":makeQuery(id+"FnGEPf5ERnqVvQ3_1.3.F4.boolean.opBoolean","SPLIT",EDGE,{"disambiguationData":[TD([subQ12])],"derivedFrom":makeQuery(id+"FnGEPf5ERnqVvQ3_1.2.F4.boolean.opBoolean","SPLIT",EDGE,{"disambiguationData":[TD([subQ12])],"derivedFrom":makeQuery(id+"FnGEPf5ERnqVvQ3_1.1.F4.boolean.opBoolean","SPLIT",EDGE,{"disambiguationData":[OD(0.0)],"derivedFrom":makeQuery(id+"F1.opExtrude","CAP_EDGE",EDGE,{"disambiguationData":[OSD([subQ8])],"isStart":true})})})})})})})})})})})});}
            var Q23;
            Q23=makeQuery(id+"F4.opExtrude","CAP_EDGE",EDGE,{"disambiguationData":[OSD([sQuery(id+"F3.wireOp",EDGE,"E23")])],"isStart":false});
            chamfer(context, id + "F7", {"entities" : qUnion([Q0, Q1, Q2, Q3, Q4, Q5, Q6, Q7, Q8, Q9, Q10, Q11, Q12, Q13, Q14, Q15, Q16, Q17, Q18, Q19, Q20, Q21, Q22, Q23]), "width" : 1 * mm, "tangentPropagation" : true});
        }
    });
